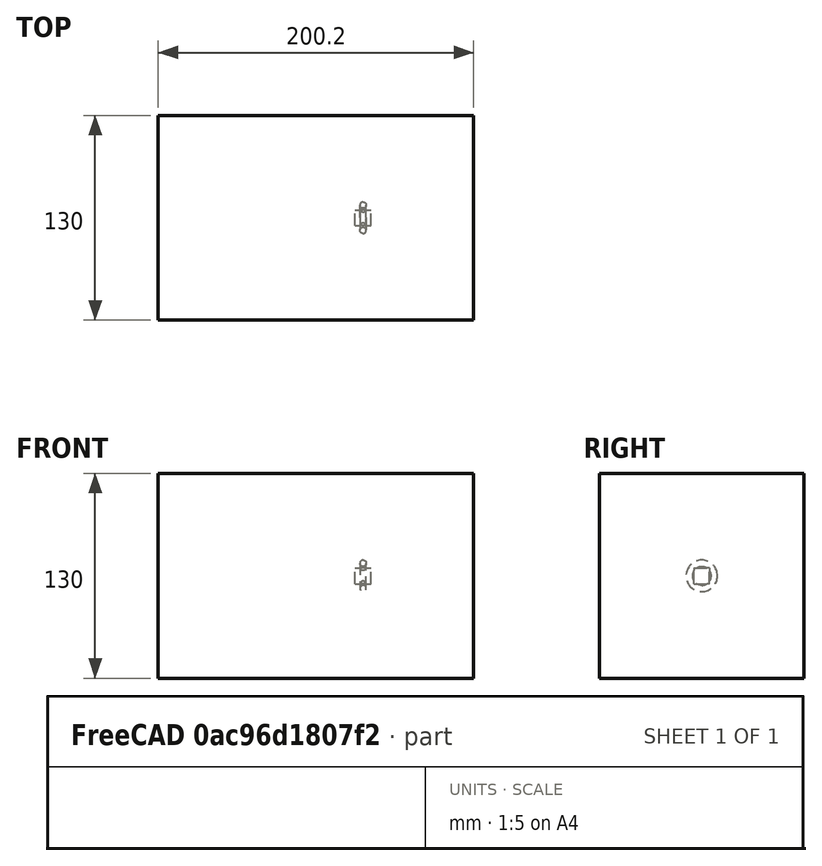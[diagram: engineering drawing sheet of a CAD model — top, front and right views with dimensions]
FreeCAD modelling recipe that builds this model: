
FCSTD DOCUMENT  (FreeCAD 1.0R39109 (Git))
Label: polarArray-7-array-translated
License: All rights reserved
objects: App::DocumentObjectGroupPython×1251, Part::FeaturePython×4, App::Part×2, Part::MultiFuse×1
note: 4 computed .brp shape members not serialized (recipe doc carries the construction recipe); baked Part::Feature solids carry a one-line shape summary decoded from their .brp

FEATURE [App::DocumentObjectGroupPython] HALFPI  # scripted group (container) (typed FeaturePython)
  name = HALFPI
  value = pi/2.
FEATURE [App::DocumentObjectGroupPython] PI  # scripted group (container) (typed FeaturePython)
  name = PI
  value = 1.*pi
FEATURE [App::DocumentObjectGroupPython] TWOPI  # scripted group (container) (typed FeaturePython)
  name = TWOPI
  value = 2.*pi
FEATURE [App::DocumentObjectGroupPython] Constants  # scripted group (container) (typed FeaturePython)
  Group = -> [HALFPI,PI,TWOPI]
FEATURE [App::DocumentObjectGroupPython] Variables  # scripted group (container) (typed FeaturePython)
FEATURE [App::DocumentObjectGroupPython] Quantities  # scripted group (container) (typed FeaturePython)
FEATURE [App::DocumentObjectGroupPython] Isotopes  # scripted group (container) (typed FeaturePython)
FEATURE [App::DocumentObjectGroupPython] Elements  # scripted group (container) (typed FeaturePython)
FEATURE [App::DocumentObjectGroupPython] Matrix  # scripted group (container) (typed FeaturePython)
FEATURE [App::DocumentObjectGroupPython] Surfaces  # scripted group (container) (typed FeaturePython)
FEATURE [App::DocumentObjectGroupPython] Opticals  # scripted group (container) (typed FeaturePython)
  Group = -> [Matrix,Surfaces]
FEATURE [App::DocumentObjectGroupPython] G4Isotopes  # scripted group (container) (typed FeaturePython)
FEATURE [App::DocumentObjectGroupPython] H_element  # scripted group (container) (typed FeaturePython)
  Z = 1
  atom_value = 1.008
  formula = H
  name = H_element
FEATURE [App::DocumentObjectGroupPython] He_element  # scripted group (container) (typed FeaturePython)
  Z = 2
  atom_value = 4.0026
  formula = He
  name = He_element
FEATURE [App::DocumentObjectGroupPython] Li_element  # scripted group (container) (typed FeaturePython)
  Z = 3
  atom_value = 6.94
  formula = Li
  name = Li_element
FEATURE [App::DocumentObjectGroupPython] Be_element  # scripted group (container) (typed FeaturePython)
  Z = 4
  atom_value = 9.01218
  formula = Be
  name = Be_element
FEATURE [App::DocumentObjectGroupPython] B_element  # scripted group (container) (typed FeaturePython)
  Z = 5
  atom_value = 10.81
  formula = B
  name = B_element
FEATURE [App::DocumentObjectGroupPython] C_element  # scripted group (container) (typed FeaturePython)
  Z = 6
  atom_value = 12.011
  formula = C
  name = C_element
FEATURE [App::DocumentObjectGroupPython] N_element  # scripted group (container) (typed FeaturePython)
  Z = 7
  atom_value = 14.007
  formula = N
  name = N_element
FEATURE [App::DocumentObjectGroupPython] O_element  # scripted group (container) (typed FeaturePython)
  Z = 8
  atom_value = 15.999
  formula = O
  name = O_element
FEATURE [App::DocumentObjectGroupPython] F_element  # scripted group (container) (typed FeaturePython)
  Z = 9
  atom_value = 18.9984
  formula = F
  name = F_element
FEATURE [App::DocumentObjectGroupPython] Ne_element  # scripted group (container) (typed FeaturePython)
  Z = 10
  atom_value = 20.1797
  formula = Ne
  name = Ne_element
FEATURE [App::DocumentObjectGroupPython] Na_element  # scripted group (container) (typed FeaturePython)
  Z = 11
  atom_value = 22.9898
  formula = Na
  name = Na_element
FEATURE [App::DocumentObjectGroupPython] Mg_element  # scripted group (container) (typed FeaturePython)
  Z = 12
  atom_value = 24.305
  formula = Mg
  name = Mg_element
FEATURE [App::DocumentObjectGroupPython] Al_element  # scripted group (container) (typed FeaturePython)
  Z = 13
  atom_value = 26.9815
  formula = Al
  name = Al_element
FEATURE [App::DocumentObjectGroupPython] Si_element  # scripted group (container) (typed FeaturePython)
  Z = 14
  atom_value = 28.085
  formula = Si
  name = Si_element
FEATURE [App::DocumentObjectGroupPython] P_element  # scripted group (container) (typed FeaturePython)
  Z = 15
  atom_value = 30.9738
  formula = P
  name = P_element
FEATURE [App::DocumentObjectGroupPython] S_element  # scripted group (container) (typed FeaturePython)
  Z = 16
  atom_value = 32.06
  formula = S
  name = S_element
FEATURE [App::DocumentObjectGroupPython] Cl_element  # scripted group (container) (typed FeaturePython)
  Z = 17
  atom_value = 35.45
  formula = Cl
  name = Cl_element
FEATURE [App::DocumentObjectGroupPython] Ar_element  # scripted group (container) (typed FeaturePython)
  Z = 18
  atom_value = 39.95
  formula = Ar
  name = Ar_element
FEATURE [App::DocumentObjectGroupPython] K_element  # scripted group (container) (typed FeaturePython)
  Z = 19
  atom_value = 39.0983
  formula = K
  name = K_element
FEATURE [App::DocumentObjectGroupPython] Ca_element  # scripted group (container) (typed FeaturePython)
  Z = 20
  atom_value = 40.078
  formula = Ca
  name = Ca_element
FEATURE [App::DocumentObjectGroupPython] Sc_element  # scripted group (container) (typed FeaturePython)
  Z = 21
  atom_value = 44.9559
  formula = Sc
  name = Sc_element
FEATURE [App::DocumentObjectGroupPython] Ti_element  # scripted group (container) (typed FeaturePython)
  Z = 22
  atom_value = 47.867
  formula = Ti
  name = Ti_element
FEATURE [App::DocumentObjectGroupPython] V_element  # scripted group (container) (typed FeaturePython)
  Z = 23
  atom_value = 50.9415
  formula = V
  name = V_element
FEATURE [App::DocumentObjectGroupPython] Cr_element  # scripted group (container) (typed FeaturePython)
  Z = 24
  atom_value = 51.9961
  formula = Cr
  name = Cr_element
FEATURE [App::DocumentObjectGroupPython] Mn_element  # scripted group (container) (typed FeaturePython)
  Z = 25
  atom_value = 54.938
  formula = Mn
  name = Mn_element
FEATURE [App::DocumentObjectGroupPython] Fe_element  # scripted group (container) (typed FeaturePython)
  Z = 26
  atom_value = 55.845
  formula = Fe
  name = Fe_element
FEATURE [App::DocumentObjectGroupPython] Co_element  # scripted group (container) (typed FeaturePython)
  Z = 27
  atom_value = 58.9332
  formula = Co
  name = Co_element
FEATURE [App::DocumentObjectGroupPython] Ni_element  # scripted group (container) (typed FeaturePython)
  Z = 28
  atom_value = 58.6934
  formula = Ni
  name = Ni_element
FEATURE [App::DocumentObjectGroupPython] Cu_element  # scripted group (container) (typed FeaturePython)
  Z = 29
  atom_value = 63.546
  formula = Cu
  name = Cu_element
FEATURE [App::DocumentObjectGroupPython] Zn_element  # scripted group (container) (typed FeaturePython)
  Z = 30
  atom_value = 65.38
  formula = Zn
  name = Zn_element
FEATURE [App::DocumentObjectGroupPython] Ga_element  # scripted group (container) (typed FeaturePython)
  Z = 31
  atom_value = 69.723
  formula = Ga
  name = Ga_element
FEATURE [App::DocumentObjectGroupPython] Ge_element  # scripted group (container) (typed FeaturePython)
  Z = 32
  atom_value = 72.63
  formula = Ge
  name = Ge_element
FEATURE [App::DocumentObjectGroupPython] As_element  # scripted group (container) (typed FeaturePython)
  Z = 33
  atom_value = 74.9216
  formula = As
  name = As_element
FEATURE [App::DocumentObjectGroupPython] Se_element  # scripted group (container) (typed FeaturePython)
  Z = 34
  atom_value = 78.971
  formula = Se
  name = Se_element
FEATURE [App::DocumentObjectGroupPython] Br_element  # scripted group (container) (typed FeaturePython)
  Z = 35
  atom_value = 79.904
  formula = Br
  name = Br_element
FEATURE [App::DocumentObjectGroupPython] Kr_element  # scripted group (container) (typed FeaturePython)
  Z = 36
  atom_value = 83.798
  formula = Kr
  name = Kr_element
FEATURE [App::DocumentObjectGroupPython] Rb_element  # scripted group (container) (typed FeaturePython)
  Z = 37
  atom_value = 85.4678
  formula = Rb
  name = Rb_element
FEATURE [App::DocumentObjectGroupPython] Sr_element  # scripted group (container) (typed FeaturePython)
  Z = 38
  atom_value = 87.62
  formula = Sr
  name = Sr_element
FEATURE [App::DocumentObjectGroupPython] Y_element  # scripted group (container) (typed FeaturePython)
  Z = 39
  atom_value = 88.9058
  formula = Y
  name = Y_element
FEATURE [App::DocumentObjectGroupPython] Zr_element  # scripted group (container) (typed FeaturePython)
  Z = 40
  atom_value = 91.224
  formula = Zr
  name = Zr_element
FEATURE [App::DocumentObjectGroupPython] Nb_element  # scripted group (container) (typed FeaturePython)
  Z = 41
  atom_value = 92.9064
  formula = Nb
  name = Nb_element
FEATURE [App::DocumentObjectGroupPython] Mo_element  # scripted group (container) (typed FeaturePython)
  Z = 42
  atom_value = 95.95
  formula = Mo
  name = Mo_element
FEATURE [App::DocumentObjectGroupPython] Tc_element  # scripted group (container) (typed FeaturePython)
  Z = 43
  atom_value = 97
  formula = Tc
  name = Tc_element
FEATURE [App::DocumentObjectGroupPython] Ru_element  # scripted group (container) (typed FeaturePython)
  Z = 44
  atom_value = 101.07
  formula = Ru
  name = Ru_element
FEATURE [App::DocumentObjectGroupPython] Rh_element  # scripted group (container) (typed FeaturePython)
  Z = 45
  atom_value = 102.905
  formula = Rh
  name = Rh_element
FEATURE [App::DocumentObjectGroupPython] Pd_element  # scripted group (container) (typed FeaturePython)
  Z = 46
  atom_value = 106.42
  formula = Pd
  name = Pd_element
FEATURE [App::DocumentObjectGroupPython] Ag_element  # scripted group (container) (typed FeaturePython)
  Z = 47
  atom_value = 107.868
  formula = Ag
  name = Ag_element
FEATURE [App::DocumentObjectGroupPython] Cd_element  # scripted group (container) (typed FeaturePython)
  Z = 48
  atom_value = 112.414
  formula = Cd
  name = Cd_element
FEATURE [App::DocumentObjectGroupPython] In_element  # scripted group (container) (typed FeaturePython)
  Z = 49
  atom_value = 114.818
  formula = In
  name = In_element
FEATURE [App::DocumentObjectGroupPython] Sn_element  # scripted group (container) (typed FeaturePython)
  Z = 50
  atom_value = 118.71
  formula = Sn
  name = Sn_element
FEATURE [App::DocumentObjectGroupPython] Sb_element  # scripted group (container) (typed FeaturePython)
  Z = 51
  atom_value = 121.76
  formula = Sb
  name = Sb_element
FEATURE [App::DocumentObjectGroupPython] Te_element  # scripted group (container) (typed FeaturePython)
  Z = 52
  atom_value = 127.6
  formula = Te
  name = Te_element
FEATURE [App::DocumentObjectGroupPython] I_element  # scripted group (container) (typed FeaturePython)
  Z = 53
  atom_value = 126.904
  formula = I
  name = I_element
FEATURE [App::DocumentObjectGroupPython] Xe_element  # scripted group (container) (typed FeaturePython)
  Z = 54
  atom_value = 131.293
  formula = Xe
  name = Xe_element
FEATURE [App::DocumentObjectGroupPython] Cs_element  # scripted group (container) (typed FeaturePython)
  Z = 55
  atom_value = 132.905
  formula = Cs
  name = Cs_element
FEATURE [App::DocumentObjectGroupPython] Ba_element  # scripted group (container) (typed FeaturePython)
  Z = 56
  atom_value = 137.327
  formula = Ba
  name = Ba_element
FEATURE [App::DocumentObjectGroupPython] La_element  # scripted group (container) (typed FeaturePython)
  Z = 57
  atom_value = 138.905
  formula = La
  name = La_element
FEATURE [App::DocumentObjectGroupPython] Ce_element  # scripted group (container) (typed FeaturePython)
  Z = 58
  atom_value = 140.116
  formula = Ce
  name = Ce_element
FEATURE [App::DocumentObjectGroupPython] Pr_element  # scripted group (container) (typed FeaturePython)
  Z = 59
  atom_value = 140.908
  formula = Pr
  name = Pr_element
FEATURE [App::DocumentObjectGroupPython] Nd_element  # scripted group (container) (typed FeaturePython)
  Z = 60
  atom_value = 144.242
  formula = Nd
  name = Nd_element
FEATURE [App::DocumentObjectGroupPython] Pm_element  # scripted group (container) (typed FeaturePython)
  Z = 61
  atom_value = 145
  formula = Pm
  name = Pm_element
FEATURE [App::DocumentObjectGroupPython] Sm_element  # scripted group (container) (typed FeaturePython)
  Z = 62
  atom_value = 150.36
  formula = Sm
  name = Sm_element
FEATURE [App::DocumentObjectGroupPython] Eu_element  # scripted group (container) (typed FeaturePython)
  Z = 63
  atom_value = 151.964
  formula = Eu
  name = Eu_element
FEATURE [App::DocumentObjectGroupPython] Gd_element  # scripted group (container) (typed FeaturePython)
  Z = 64
  atom_value = 157.25
  formula = Gd
  name = Gd_element
FEATURE [App::DocumentObjectGroupPython] Tb_element  # scripted group (container) (typed FeaturePython)
  Z = 65
  atom_value = 158.925
  formula = Tb
  name = Tb_element
FEATURE [App::DocumentObjectGroupPython] Dy_element  # scripted group (container) (typed FeaturePython)
  Z = 66
  atom_value = 162.5
  formula = Dy
  name = Dy_element
FEATURE [App::DocumentObjectGroupPython] Ho_element  # scripted group (container) (typed FeaturePython)
  Z = 67
  atom_value = 164.93
  formula = Ho
  name = Ho_element
FEATURE [App::DocumentObjectGroupPython] Er_element  # scripted group (container) (typed FeaturePython)
  Z = 68
  atom_value = 167.259
  formula = Er
  name = Er_element
FEATURE [App::DocumentObjectGroupPython] Tm_element  # scripted group (container) (typed FeaturePython)
  Z = 69
  atom_value = 168.934
  formula = Tm
  name = Tm_element
FEATURE [App::DocumentObjectGroupPython] Yb_element  # scripted group (container) (typed FeaturePython)
  Z = 70
  atom_value = 173.045
  formula = Yb
  name = Yb_element
FEATURE [App::DocumentObjectGroupPython] Lu_element  # scripted group (container) (typed FeaturePython)
  Z = 71
  atom_value = 174.967
  formula = Lu
  name = Lu_element
FEATURE [App::DocumentObjectGroupPython] Hf_element  # scripted group (container) (typed FeaturePython)
  Z = 72
  atom_value = 178.49
  formula = Hf
  name = Hf_element
FEATURE [App::DocumentObjectGroupPython] Ta_element  # scripted group (container) (typed FeaturePython)
  Z = 73
  atom_value = 180.948
  formula = Ta
  name = Ta_element
FEATURE [App::DocumentObjectGroupPython] W_element  # scripted group (container) (typed FeaturePython)
  Z = 74
  atom_value = 183.84
  formula = W
  name = W_element
FEATURE [App::DocumentObjectGroupPython] Re_element  # scripted group (container) (typed FeaturePython)
  Z = 75
  atom_value = 186.207
  formula = Re
  name = Re_element
FEATURE [App::DocumentObjectGroupPython] Os_element  # scripted group (container) (typed FeaturePython)
  Z = 76
  atom_value = 190.23
  formula = Os
  name = Os_element
FEATURE [App::DocumentObjectGroupPython] Ir_element  # scripted group (container) (typed FeaturePython)
  Z = 77
  atom_value = 192.217
  formula = Ir
  name = Ir_element
FEATURE [App::DocumentObjectGroupPython] Pt_element  # scripted group (container) (typed FeaturePython)
  Z = 78
  atom_value = 195.084
  formula = Pt
  name = Pt_element
FEATURE [App::DocumentObjectGroupPython] Au_element  # scripted group (container) (typed FeaturePython)
  Z = 79
  atom_value = 196.967
  formula = Au
  name = Au_element
FEATURE [App::DocumentObjectGroupPython] Hg_element  # scripted group (container) (typed FeaturePython)
  Z = 80
  atom_value = 200.592
  formula = Hg
  name = Hg_element
FEATURE [App::DocumentObjectGroupPython] Tl_element  # scripted group (container) (typed FeaturePython)
  Z = 81
  atom_value = 204.38
  formula = Tl
  name = Tl_element
FEATURE [App::DocumentObjectGroupPython] Pb_element  # scripted group (container) (typed FeaturePython)
  Z = 82
  atom_value = 207.2
  formula = Pb
  name = Pb_element
FEATURE [App::DocumentObjectGroupPython] Bi_element  # scripted group (container) (typed FeaturePython)
  Z = 83
  atom_value = 208.98
  formula = Bi
  name = Bi_element
FEATURE [App::DocumentObjectGroupPython] Po_element  # scripted group (container) (typed FeaturePython)
  Z = 84
  atom_value = 209
  formula = Po
  name = Po_element
FEATURE [App::DocumentObjectGroupPython] At_element  # scripted group (container) (typed FeaturePython)
  Z = 85
  atom_value = 210
  formula = At
  name = At_element
FEATURE [App::DocumentObjectGroupPython] Rn_element  # scripted group (container) (typed FeaturePython)
  Z = 86
  atom_value = 222
  formula = Rn
  name = Rn_element
FEATURE [App::DocumentObjectGroupPython] Fr_element  # scripted group (container) (typed FeaturePython)
  Z = 87
  atom_value = 223
  formula = Fr
  name = Fr_element
FEATURE [App::DocumentObjectGroupPython] Ra_element  # scripted group (container) (typed FeaturePython)
  Z = 88
  atom_value = 226
  formula = Ra
  name = Ra_element
FEATURE [App::DocumentObjectGroupPython] Ac_element  # scripted group (container) (typed FeaturePython)
  Z = 89
  atom_value = 227
  formula = Ac
  name = Ac_element
FEATURE [App::DocumentObjectGroupPython] Th_element  # scripted group (container) (typed FeaturePython)
  Z = 90
  atom_value = 232.038
  formula = Th
  name = Th_element
FEATURE [App::DocumentObjectGroupPython] Pa_element  # scripted group (container) (typed FeaturePython)
  Z = 91
  atom_value = 231.036
  formula = Pa
  name = Pa_element
FEATURE [App::DocumentObjectGroupPython] U_element  # scripted group (container) (typed FeaturePython)
  Z = 92
  atom_value = 238.029
  formula = U
  name = U_element
FEATURE [App::DocumentObjectGroupPython] Np_element  # scripted group (container) (typed FeaturePython)
  Z = 93
  atom_value = 237
  formula = Np
  name = Np_element
FEATURE [App::DocumentObjectGroupPython] Pu_element  # scripted group (container) (typed FeaturePython)
  Z = 94
  atom_value = 244
  formula = Pu
  name = Pu_element
FEATURE [App::DocumentObjectGroupPython] Am_element  # scripted group (container) (typed FeaturePython)
  Z = 95
  atom_value = 243
  formula = Am
  name = Am_element
FEATURE [App::DocumentObjectGroupPython] Cm_element  # scripted group (container) (typed FeaturePython)
  Z = 96
  atom_value = 247
  formula = Cm
  name = Cm_element
FEATURE [App::DocumentObjectGroupPython] Bk_element  # scripted group (container) (typed FeaturePython)
  Z = 97
  atom_value = 247
  formula = Bk
  name = Bk_element
FEATURE [App::DocumentObjectGroupPython] Cf_element  # scripted group (container) (typed FeaturePython)
  Z = 98
  atom_value = 251
  formula = Cf
  name = Cf_element
FEATURE [App::DocumentObjectGroupPython] G4Elements  # scripted group (container) (typed FeaturePython)
  Group = -> [H_element,He_element,Li_element,Be_element,B_element,C_element,N_element,O_element,F_element,Ne_element,Na_element,Mg_element,Al_element,Si_element,P_element,S_element,Cl_element,Ar_element,K_element,Ca_element,Sc_element,Ti_element,V_element,Cr_element,Mn_element,Fe_element,Co_element,Ni_element,Cu_element,Zn_element,Ga_element,Ge_element,As_element,Se_element,Br_element,Kr_element,Rb_element,+61 more]
FEATURE [App::DocumentObjectGroupPython] H_element001  label="H_element : 0.101"  # scripted group (container) (typed FeaturePython)
  n = 0.101327
FEATURE [App::DocumentObjectGroupPython] C_element001  label="C_element : 0.775"  # scripted group (container) (typed FeaturePython)
  n = 0.7755
FEATURE [App::DocumentObjectGroupPython] N_element001  label="N_element : 0.035"  # scripted group (container) (typed FeaturePython)
  n = 0.035057
FEATURE [App::DocumentObjectGroupPython] O_element001  label="O_element : 0.052"  # scripted group (container) (typed FeaturePython)
  n = 0.0523159
FEATURE [App::DocumentObjectGroupPython] F_element001  label="F_element : 0.017"  # scripted group (container) (typed FeaturePython)
  n = 0.017422
FEATURE [App::DocumentObjectGroupPython] Ca_element001  label="Ca_element : 0.018"  # scripted group (container) (typed FeaturePython)
  n = 0.018378
FEATURE [App::DocumentObjectGroupPython] G4_A_150_TISSUE  label="G4_A-150_TISSUE"  # scripted group (container) (typed FeaturePython)
  Dunit = g/cm3
  Dvalue = 1.127
  Group = -> [H_element001,C_element001,N_element001,O_element001,F_element001,Ca_element001]
  conduct = 2
  density = 1
  expand = 3
  formula = G4_A-150_TISSUE
  name = G4_A-150_TISSUE
  specific = 4
FEATURE [App::DocumentObjectGroupPython] C_element002  label="C_element : 3"  # scripted group (container) (typed FeaturePython)
  n = 3
  ref = C_element
FEATURE [App::DocumentObjectGroupPython] H_element002  label="H_element : 6"  # scripted group (container) (typed FeaturePython)
  n = 6
  ref = H_element
FEATURE [App::DocumentObjectGroupPython] O_element002  label="O_element : 1"  # scripted group (container) (typed FeaturePython)
  n = 1
  ref = O_element
FEATURE [App::DocumentObjectGroupPython] G4_ACETONE  # scripted group (container) (typed FeaturePython)
  Dunit = g/cm3
  Dvalue = 0.7899
  Group = -> [C_element002,H_element002,O_element002]
  conduct = 2
  density = 1
  expand = 3
  formula = G4_ACETONE
  name = G4_ACETONE
  specific = 4
FEATURE [App::DocumentObjectGroupPython] C_element003  label="C_element : 2"  # scripted group (container) (typed FeaturePython)
  n = 2
  ref = C_element
FEATURE [App::DocumentObjectGroupPython] H_element003  label="H_element : 2"  # scripted group (container) (typed FeaturePython)
  n = 2
  ref = H_element
FEATURE [App::DocumentObjectGroupPython] G4_ACETYLENE  # scripted group (container) (typed FeaturePython)
  Dunit = g/cm3
  Dvalue = 0.0010967
  Group = -> [C_element003,H_element003]
  conduct = 2
  density = 1
  expand = 3
  formula = G4_ACETYLENE
  name = G4_ACETYLENE
  specific = 4
FEATURE [App::DocumentObjectGroupPython] C_element004  label="C_element : 5"  # scripted group (container) (typed FeaturePython)
  n = 5
  ref = C_element
FEATURE [App::DocumentObjectGroupPython] H_element004  label="H_element : 5"  # scripted group (container) (typed FeaturePython)
  n = 5
  ref = H_element
FEATURE [App::DocumentObjectGroupPython] N_element002  label="N_element : 5"  # scripted group (container) (typed FeaturePython)
  n = 5
  ref = N_element
FEATURE [App::DocumentObjectGroupPython] G4_ADENINE  # scripted group (container) (typed FeaturePython)
  Dunit = g/cm3
  Dvalue = 1.6
  Group = -> [C_element004,H_element004,N_element002]
  conduct = 2
  density = 1
  expand = 3
  formula = G4_ADENINE
  name = G4_ADENINE
  specific = 4
FEATURE [App::DocumentObjectGroupPython] H_element005  label="H_element : 0.114"  # scripted group (container) (typed FeaturePython)
  n = 0.114
FEATURE [App::DocumentObjectGroupPython] C_element005  label="C_element : 0.598"  # scripted group (container) (typed FeaturePython)
  n = 0.598
FEATURE [App::DocumentObjectGroupPython] N_element003  label="N_element : 0.007"  # scripted group (container) (typed FeaturePython)
  n = 0.007
FEATURE [App::DocumentObjectGroupPython] O_element003  label="O_element : 0.278"  # scripted group (container) (typed FeaturePython)
  n = 0.278
FEATURE [App::DocumentObjectGroupPython] Na_element001  label="Na_element : 0.001"  # scripted group (container) (typed FeaturePython)
  n = 0.001
FEATURE [App::DocumentObjectGroupPython] S_element001  label="S_element : 0.001"  # scripted group (container) (typed FeaturePython)
  n = 0.001
FEATURE [App::DocumentObjectGroupPython] Cl_element001  label="Cl_element : 0.001"  # scripted group (container) (typed FeaturePython)
  n = 0.001
FEATURE [App::DocumentObjectGroupPython] G4_ADIPOSE_TISSUE_ICRP  # scripted group (container) (typed FeaturePython)
  Dunit = g/cm3
  Dvalue = 0.95
  Group = -> [H_element005,C_element005,N_element003,O_element003,Na_element001,S_element001,Cl_element001]
  conduct = 2
  density = 1
  expand = 3
  formula = G4_ADIPOSE_TISSUE_ICRP
  name = G4_ADIPOSE_TISSUE_ICRP
  specific = 4
FEATURE [App::DocumentObjectGroupPython] C_element006  label="C_element : 0.000"  # scripted group (container) (typed FeaturePython)
  n = 0.000124
FEATURE [App::DocumentObjectGroupPython] N_element004  label="N_element : 0.755"  # scripted group (container) (typed FeaturePython)
  n = 0.755268
FEATURE [App::DocumentObjectGroupPython] O_element004  label="O_element : 0.232"  # scripted group (container) (typed FeaturePython)
  n = 0.231781
FEATURE [App::DocumentObjectGroupPython] Ar_element001  label="Ar_element : 0.013"  # scripted group (container) (typed FeaturePython)
  n = 0.012827
FEATURE [App::DocumentObjectGroupPython] G4_AIR  # scripted group (container) (typed FeaturePython)
  Dunit = g/cm3
  Dvalue = 0.00120479
  Group = -> [C_element006,N_element004,O_element004,Ar_element001]
  conduct = 2
  density = 1
  expand = 3
  formula = G4_AIR
  name = G4_AIR
  specific = 4
FEATURE [App::DocumentObjectGroupPython] C_element007  label="C_element : 006"  # scripted group (container) (typed FeaturePython)
  n = 3
  ref = C_element
FEATURE [App::DocumentObjectGroupPython] H_element006  label="H_element : 7"  # scripted group (container) (typed FeaturePython)
  n = 7
  ref = H_element
FEATURE [App::DocumentObjectGroupPython] N_element005  label="N_element : 1"  # scripted group (container) (typed FeaturePython)
  n = 1
  ref = N_element
FEATURE [App::DocumentObjectGroupPython] O_element005  label="O_element : 2"  # scripted group (container) (typed FeaturePython)
  n = 2
  ref = O_element
FEATURE [App::DocumentObjectGroupPython] G4_ALANINE  # scripted group (container) (typed FeaturePython)
  Dunit = g/cm3
  Dvalue = 1.42
  Group = -> [C_element007,H_element006,N_element005,O_element005]
  conduct = 2
  density = 1
  expand = 3
  formula = G4_ALANINE
  name = G4_ALANINE
  specific = 4
FEATURE [App::DocumentObjectGroupPython] Al_element001  label="Al_element : 2"  # scripted group (container) (typed FeaturePython)
  n = 2
  ref = Al_element
FEATURE [App::DocumentObjectGroupPython] O_element006  label="O_element : 3"  # scripted group (container) (typed FeaturePython)
  n = 3
  ref = O_element
FEATURE [App::DocumentObjectGroupPython] G4_ALUMINUM_OXIDE  # scripted group (container) (typed FeaturePython)
  Dunit = g/cm3
  Dvalue = 3.97
  Group = -> [Al_element001,O_element006]
  conduct = 2
  density = 1
  expand = 3
  formula = G4_ALUMINUM_OXIDE
  name = G4_ALUMINUM_OXIDE
  specific = 4
FEATURE [App::DocumentObjectGroupPython] H_element007  label="H_element : 0.106"  # scripted group (container) (typed FeaturePython)
  n = 0.10593
FEATURE [App::DocumentObjectGroupPython] C_element008  label="C_element : 0.789"  # scripted group (container) (typed FeaturePython)
  n = 0.788974
FEATURE [App::DocumentObjectGroupPython] O_element007  label="O_element : 0.105"  # scripted group (container) (typed FeaturePython)
  n = 0.105096
FEATURE [App::DocumentObjectGroupPython] G4_AMBER  # scripted group (container) (typed FeaturePython)
  Dunit = g/cm3
  Dvalue = 1.1
  Group = -> [H_element007,C_element008,O_element007]
  conduct = 2
  density = 1
  expand = 3
  formula = G4_AMBER
  name = G4_AMBER
  specific = 4
FEATURE [App::DocumentObjectGroupPython] N_element006  label="N_element : 006"  # scripted group (container) (typed FeaturePython)
  n = 1
  ref = N_element
FEATURE [App::DocumentObjectGroupPython] H_element008  label="H_element : 3"  # scripted group (container) (typed FeaturePython)
  n = 3
  ref = H_element
FEATURE [App::DocumentObjectGroupPython] G4_AMMONIA  # scripted group (container) (typed FeaturePython)
  Dunit = g/cm3
  Dvalue = 0.000826019
  Group = -> [N_element006,H_element008]
  conduct = 2
  density = 1
  expand = 3
  formula = G4_AMMONIA
  name = G4_AMMONIA
  specific = 4
FEATURE [App::DocumentObjectGroupPython] C_element009  label="C_element : 6"  # scripted group (container) (typed FeaturePython)
  n = 6
  ref = C_element
FEATURE [App::DocumentObjectGroupPython] H_element009  label="H_element : 008"  # scripted group (container) (typed FeaturePython)
  n = 7
  ref = H_element
FEATURE [App::DocumentObjectGroupPython] N_element007  label="N_element : 007"  # scripted group (container) (typed FeaturePython)
  n = 1
  ref = N_element
FEATURE [App::DocumentObjectGroupPython] G4_ANILINE  # scripted group (container) (typed FeaturePython)
  Dunit = g/cm3
  Dvalue = 1.0235
  Group = -> [C_element009,H_element009,N_element007]
  conduct = 2
  density = 1
  expand = 3
  formula = G4_ANILINE
  name = G4_ANILINE
  specific = 4
FEATURE [App::DocumentObjectGroupPython] C_element010  label="C_element : 14"  # scripted group (container) (typed FeaturePython)
  n = 14
  ref = C_element
FEATURE [App::DocumentObjectGroupPython] H_element010  label="H_element : 10"  # scripted group (container) (typed FeaturePython)
  n = 10
  ref = H_element
FEATURE [App::DocumentObjectGroupPython] G4_ANTHRACENE  # scripted group (container) (typed FeaturePython)
  Dunit = g/cm3
  Dvalue = 1.283
  Group = -> [C_element010,H_element010]
  conduct = 2
  density = 1
  expand = 3
  formula = G4_ANTHRACENE
  name = G4_ANTHRACENE
  specific = 4
FEATURE [App::DocumentObjectGroupPython] H_element011  label="H_element : 0.065"  # scripted group (container) (typed FeaturePython)
  n = 0.0654709
FEATURE [App::DocumentObjectGroupPython] C_element011  label="C_element : 0.537"  # scripted group (container) (typed FeaturePython)
  n = 0.536944
FEATURE [App::DocumentObjectGroupPython] N_element008  label="N_element : 0.021"  # scripted group (container) (typed FeaturePython)
  n = 0.0215
FEATURE [App::DocumentObjectGroupPython] O_element008  label="O_element : 0.032"  # scripted group (container) (typed FeaturePython)
  n = 0.032085
FEATURE [App::DocumentObjectGroupPython] F_element002  label="F_element : 0.167"  # scripted group (container) (typed FeaturePython)
  n = 0.167411
FEATURE [App::DocumentObjectGroupPython] Ca_element002  label="Ca_element : 0.177"  # scripted group (container) (typed FeaturePython)
  n = 0.176589
FEATURE [App::DocumentObjectGroupPython] G4_B_100_BONE  label="G4_B-100_BONE"  # scripted group (container) (typed FeaturePython)
  Dunit = g/cm3
  Dvalue = 1.45
  Group = -> [H_element011,C_element011,N_element008,O_element008,F_element002,Ca_element002]
  conduct = 2
  density = 1
  expand = 3
  formula = G4_B-100_BONE
  name = G4_B-100_BONE
  specific = 4
FEATURE [App::DocumentObjectGroupPython] H_element012  label="H_element : 0.057"  # scripted group (container) (typed FeaturePython)
  n = 0.057441
FEATURE [App::DocumentObjectGroupPython] C_element012  label="C_element : 0.790"  # scripted group (container) (typed FeaturePython)
  n = 0.774591
FEATURE [App::DocumentObjectGroupPython] O_element009  label="O_element : 0.168"  # scripted group (container) (typed FeaturePython)
  n = 0.167968
FEATURE [App::DocumentObjectGroupPython] G4_BAKELITE  # scripted group (container) (typed FeaturePython)
  Dunit = g/cm3
  Dvalue = 1.25
  Group = -> [H_element012,C_element012,O_element009]
  conduct = 2
  density = 1
  expand = 3
  formula = G4_BAKELITE
  name = G4_BAKELITE
  specific = 4
FEATURE [App::DocumentObjectGroupPython] Ba_element001  label="Ba_element : 1"  # scripted group (container) (typed FeaturePython)
  n = 1
  ref = Ba_element
FEATURE [App::DocumentObjectGroupPython] F_element003  label="F_element : 2"  # scripted group (container) (typed FeaturePython)
  n = 2
  ref = F_element
FEATURE [App::DocumentObjectGroupPython] G4_BARIUM_FLUORIDE  # scripted group (container) (typed FeaturePython)
  Dunit = g/cm3
  Dvalue = 4.89
  Group = -> [Ba_element001,F_element003]
  conduct = 2
  density = 1
  expand = 3
  formula = G4_BARIUM_FLUORIDE
  name = G4_BARIUM_FLUORIDE
  specific = 4
FEATURE [App::DocumentObjectGroupPython] Ba_element002  label="Ba_element : 002"  # scripted group (container) (typed FeaturePython)
  n = 1
  ref = Ba_element
FEATURE [App::DocumentObjectGroupPython] S_element002  label="S_element : 1"  # scripted group (container) (typed FeaturePython)
  n = 1
  ref = S_element
FEATURE [App::DocumentObjectGroupPython] O_element010  label="O_element : 4"  # scripted group (container) (typed FeaturePython)
  n = 4
  ref = O_element
FEATURE [App::DocumentObjectGroupPython] G4_BARIUM_SULFATE  # scripted group (container) (typed FeaturePython)
  Dunit = g/cm3
  Dvalue = 4.5
  Group = -> [Ba_element002,S_element002,O_element010]
  conduct = 2
  density = 1
  expand = 3
  formula = G4_BARIUM_SULFATE
  name = G4_BARIUM_SULFATE
  specific = 4
FEATURE [App::DocumentObjectGroupPython] C_element013  label="C_element : 007"  # scripted group (container) (typed FeaturePython)
  n = 6
  ref = C_element
FEATURE [App::DocumentObjectGroupPython] H_element013  label="H_element : 009"  # scripted group (container) (typed FeaturePython)
  n = 6
  ref = H_element
FEATURE [App::DocumentObjectGroupPython] G4_BENZENE  # scripted group (container) (typed FeaturePython)
  Dunit = g/cm3
  Dvalue = 0.87865
  Group = -> [C_element013,H_element013]
  conduct = 2
  density = 1
  expand = 3
  formula = G4_BENZENE
  name = G4_BENZENE
  specific = 4
FEATURE [App::DocumentObjectGroupPython] Be_element001  label="Be_element : 1"  # scripted group (container) (typed FeaturePython)
  n = 1
  ref = Be_element
FEATURE [App::DocumentObjectGroupPython] O_element011  label="O_element : 005"  # scripted group (container) (typed FeaturePython)
  n = 1
  ref = O_element
FEATURE [App::DocumentObjectGroupPython] G4_BERYLLIUM_OXIDE  # scripted group (container) (typed FeaturePython)
  Dunit = g/cm3
  Dvalue = 3.01
  Group = -> [Be_element001,O_element011]
  conduct = 2
  density = 1
  expand = 3
  formula = G4_BERYLLIUM_OXIDE
  name = G4_BERYLLIUM_OXIDE
  specific = 4
FEATURE [App::DocumentObjectGroupPython] Bi_element001  label="Bi_element : 4"  # scripted group (container) (typed FeaturePython)
  n = 4
  ref = Bi_element
FEATURE [App::DocumentObjectGroupPython] Ge_element001  label="Ge_element : 3"  # scripted group (container) (typed FeaturePython)
  n = 3
  ref = Ge_element
FEATURE [App::DocumentObjectGroupPython] O_element012  label="O_element : 12"  # scripted group (container) (typed FeaturePython)
  n = 12
  ref = O_element
FEATURE [App::DocumentObjectGroupPython] G4_BGO  # scripted group (container) (typed FeaturePython)
  Dunit = g/cm3
  Dvalue = 7.13
  Group = -> [Bi_element001,Ge_element001,O_element012]
  conduct = 2
  density = 1
  expand = 3
  formula = G4_BGO
  name = G4_BGO
  specific = 4
FEATURE [App::DocumentObjectGroupPython] H_element014  label="H_element : 0.102"  # scripted group (container) (typed FeaturePython)
  n = 0.102
FEATURE [App::DocumentObjectGroupPython] C_element014  label="C_element : 0.110"  # scripted group (container) (typed FeaturePython)
  n = 0.11
FEATURE [App::DocumentObjectGroupPython] N_element009  label="N_element : 0.033"  # scripted group (container) (typed FeaturePython)
  n = 0.033
FEATURE [App::DocumentObjectGroupPython] O_element013  label="O_element : 0.745"  # scripted group (container) (typed FeaturePython)
  n = 0.745
FEATURE [App::DocumentObjectGroupPython] Na_element002  label="Na_element : 0.002"  # scripted group (container) (typed FeaturePython)
  n = 0.001
FEATURE [App::DocumentObjectGroupPython] P_element001  label="P_element : 0.001"  # scripted group (container) (typed FeaturePython)
  n = 0.001
FEATURE [App::DocumentObjectGroupPython] S_element003  label="S_element : 0.002"  # scripted group (container) (typed FeaturePython)
  n = 0.002
FEATURE [App::DocumentObjectGroupPython] Cl_element002  label="Cl_element : 0.003"  # scripted group (container) (typed FeaturePython)
  n = 0.003
FEATURE [App::DocumentObjectGroupPython] K_element001  label="K_element : 0.002"  # scripted group (container) (typed FeaturePython)
  n = 0.002
FEATURE [App::DocumentObjectGroupPython] Fe_element001  label="Fe_element : 0.001"  # scripted group (container) (typed FeaturePython)
  n = 0.001
FEATURE [App::DocumentObjectGroupPython] G4_BLOOD_ICRP  # scripted group (container) (typed FeaturePython)
  Dunit = g/cm3
  Dvalue = 1.06
  Group = -> [H_element014,C_element014,N_element009,O_element013,Na_element002,P_element001,S_element003,Cl_element002,K_element001,Fe_element001]
  conduct = 2
  density = 1
  expand = 3
  formula = G4_BLOOD_ICRP
  name = G4_BLOOD_ICRP
  specific = 4
FEATURE [App::DocumentObjectGroupPython] H_element015  label="H_element : 0.064"  # scripted group (container) (typed FeaturePython)
  n = 0.064
FEATURE [App::DocumentObjectGroupPython] C_element015  label="C_element : 0.278"  # scripted group (container) (typed FeaturePython)
  n = 0.278
FEATURE [App::DocumentObjectGroupPython] N_element010  label="N_element : 0.027"  # scripted group (container) (typed FeaturePython)
  n = 0.027
FEATURE [App::DocumentObjectGroupPython] O_element014  label="O_element : 0.410"  # scripted group (container) (typed FeaturePython)
  n = 0.41
FEATURE [App::DocumentObjectGroupPython] Mg_element001  label="Mg_element : 0.002"  # scripted group (container) (typed FeaturePython)
  n = 0.002
FEATURE [App::DocumentObjectGroupPython] P_element002  label="P_element : 0.070"  # scripted group (container) (typed FeaturePython)
  n = 0.07
FEATURE [App::DocumentObjectGroupPython] S_element004  label="S_element : 0.003"  # scripted group (container) (typed FeaturePython)
  n = 0.002
FEATURE [App::DocumentObjectGroupPython] Ca_element003  label="Ca_element : 0.147"  # scripted group (container) (typed FeaturePython)
  n = 0.147
FEATURE [App::DocumentObjectGroupPython] G4_BONE_COMPACT_ICRU  # scripted group (container) (typed FeaturePython)
  Dunit = g/cm3
  Dvalue = 1.85
  Group = -> [H_element015,C_element015,N_element010,O_element014,Mg_element001,P_element002,S_element004,Ca_element003]
  conduct = 2
  density = 1
  expand = 3
  formula = G4_BONE_COMPACT_ICRU
  name = G4_BONE_COMPACT_ICRU
  specific = 4
FEATURE [App::DocumentObjectGroupPython] H_element016  label="H_element : 0.034"  # scripted group (container) (typed FeaturePython)
  n = 0.034
FEATURE [App::DocumentObjectGroupPython] C_element016  label="C_element : 0.155"  # scripted group (container) (typed FeaturePython)
  n = 0.155
FEATURE [App::DocumentObjectGroupPython] N_element011  label="N_element : 0.042"  # scripted group (container) (typed FeaturePython)
  n = 0.042
FEATURE [App::DocumentObjectGroupPython] O_element015  label="O_element : 0.435"  # scripted group (container) (typed FeaturePython)
  n = 0.435
FEATURE [App::DocumentObjectGroupPython] Na_element003  label="Na_element : 0.003"  # scripted group (container) (typed FeaturePython)
  n = 0.001
FEATURE [App::DocumentObjectGroupPython] Mg_element002  label="Mg_element : 0.003"  # scripted group (container) (typed FeaturePython)
  n = 0.002
FEATURE [App::DocumentObjectGroupPython] P_element003  label="P_element : 0.103"  # scripted group (container) (typed FeaturePython)
  n = 0.103
FEATURE [App::DocumentObjectGroupPython] S_element005  label="S_element : 0.004"  # scripted group (container) (typed FeaturePython)
  n = 0.003
FEATURE [App::DocumentObjectGroupPython] Ca_element004  label="Ca_element : 0.225"  # scripted group (container) (typed FeaturePython)
  n = 0.225
FEATURE [App::DocumentObjectGroupPython] G4_BONE_CORTICAL_ICRP  # scripted group (container) (typed FeaturePython)
  Dunit = g/cm3
  Dvalue = 1.92
  Group = -> [H_element016,C_element016,N_element011,O_element015,Na_element003,Mg_element002,P_element003,S_element005,Ca_element004]
  conduct = 2
  density = 1
  expand = 3
  formula = G4_BONE_CORTICAL_ICRP
  name = G4_BONE_CORTICAL_ICRP
  specific = 4
FEATURE [App::DocumentObjectGroupPython] B_element001  label="B_element : 4"  # scripted group (container) (typed FeaturePython)
  n = 4
  ref = B_element
FEATURE [App::DocumentObjectGroupPython] C_element017  label="C_element : 1"  # scripted group (container) (typed FeaturePython)
  n = 1
  ref = C_element
FEATURE [App::DocumentObjectGroupPython] G4_BORON_CARBIDE  # scripted group (container) (typed FeaturePython)
  Dunit = g/cm3
  Dvalue = 2.52
  Group = -> [B_element001,C_element017]
  conduct = 2
  density = 1
  expand = 3
  formula = G4_BORON_CARBIDE
  name = G4_BORON_CARBIDE
  specific = 4
FEATURE [App::DocumentObjectGroupPython] B_element002  label="B_element : 2"  # scripted group (container) (typed FeaturePython)
  n = 2
  ref = B_element
FEATURE [App::DocumentObjectGroupPython] O_element016  label="O_element : 006"  # scripted group (container) (typed FeaturePython)
  n = 3
  ref = O_element
FEATURE [App::DocumentObjectGroupPython] G4_BORON_OXIDE  # scripted group (container) (typed FeaturePython)
  Dunit = g/cm3
  Dvalue = 1.812
  Group = -> [B_element002,O_element016]
  conduct = 2
  density = 1
  expand = 3
  formula = G4_BORON_OXIDE
  name = G4_BORON_OXIDE
  specific = 4
FEATURE [App::DocumentObjectGroupPython] H_element017  label="H_element : 0.107"  # scripted group (container) (typed FeaturePython)
  n = 0.107
FEATURE [App::DocumentObjectGroupPython] C_element018  label="C_element : 0.145"  # scripted group (container) (typed FeaturePython)
  n = 0.145
FEATURE [App::DocumentObjectGroupPython] N_element012  label="N_element : 0.022"  # scripted group (container) (typed FeaturePython)
  n = 0.022
FEATURE [App::DocumentObjectGroupPython] O_element017  label="O_element : 0.712"  # scripted group (container) (typed FeaturePython)
  n = 0.712
FEATURE [App::DocumentObjectGroupPython] Na_element004  label="Na_element : 0.004"  # scripted group (container) (typed FeaturePython)
  n = 0.002
FEATURE [App::DocumentObjectGroupPython] P_element004  label="P_element : 0.004"  # scripted group (container) (typed FeaturePython)
  n = 0.004
FEATURE [App::DocumentObjectGroupPython] S_element006  label="S_element : 0.005"  # scripted group (container) (typed FeaturePython)
  n = 0.002
FEATURE [App::DocumentObjectGroupPython] Cl_element003  label="Cl_element : 0.004"  # scripted group (container) (typed FeaturePython)
  n = 0.003
FEATURE [App::DocumentObjectGroupPython] K_element002  label="K_element : 0.003"  # scripted group (container) (typed FeaturePython)
  n = 0.003
FEATURE [App::DocumentObjectGroupPython] G4_BRAIN_ICRP  # scripted group (container) (typed FeaturePython)
  Dunit = g/cm3
  Dvalue = 1.04
  Group = -> [H_element017,C_element018,N_element012,O_element017,Na_element004,P_element004,S_element006,Cl_element003,K_element002]
  conduct = 2
  density = 1
  expand = 3
  formula = G4_BRAIN_ICRP
  name = G4_BRAIN_ICRP
  specific = 4
FEATURE [App::DocumentObjectGroupPython] C_element019  label="C_element : 4"  # scripted group (container) (typed FeaturePython)
  n = 4
  ref = C_element
FEATURE [App::DocumentObjectGroupPython] H_element018  label="H_element : 010"  # scripted group (container) (typed FeaturePython)
  n = 10
  ref = H_element
FEATURE [App::DocumentObjectGroupPython] G4_BUTANE  # scripted group (container) (typed FeaturePython)
  Dunit = g/cm3
  Dvalue = 0.00249343
  Group = -> [C_element019,H_element018]
  conduct = 2
  density = 1
  expand = 3
  formula = G4_BUTANE
  name = G4_BUTANE
  specific = 4
FEATURE [App::DocumentObjectGroupPython] C_element020  label="C_element : 008"  # scripted group (container) (typed FeaturePython)
  n = 4
  ref = C_element
FEATURE [App::DocumentObjectGroupPython] H_element019  label="H_element : 011"  # scripted group (container) (typed FeaturePython)
  n = 10
  ref = H_element
FEATURE [App::DocumentObjectGroupPython] O_element018  label="O_element : 007"  # scripted group (container) (typed FeaturePython)
  n = 1
  ref = O_element
FEATURE [App::DocumentObjectGroupPython] G4_N_BUTYL_ALCOHOL  label="G4_N-BUTYL_ALCOHOL"  # scripted group (container) (typed FeaturePython)
  Dunit = g/cm3
  Dvalue = 0.8098
  Group = -> [C_element020,H_element019,O_element018]
  conduct = 2
  density = 1
  expand = 3
  formula = G4_N-BUTYL_ALCOHOL
  name = G4_N-BUTYL_ALCOHOL
  specific = 4
FEATURE [App::DocumentObjectGroupPython] H_element020  label="H_element : 0.025"  # scripted group (container) (typed FeaturePython)
  n = 0.02468
FEATURE [App::DocumentObjectGroupPython] C_element021  label="C_element : 0.502"  # scripted group (container) (typed FeaturePython)
  n = 0.501611
FEATURE [App::DocumentObjectGroupPython] O_element019  label="O_element : 0.005"  # scripted group (container) (typed FeaturePython)
  n = 0.004527
FEATURE [App::DocumentObjectGroupPython] F_element004  label="F_element : 0.465"  # scripted group (container) (typed FeaturePython)
  n = 0.465209
FEATURE [App::DocumentObjectGroupPython] Si_element001  label="Si_element : 0.004"  # scripted group (container) (typed FeaturePython)
  n = 0.003973
FEATURE [App::DocumentObjectGroupPython] G4_C_552  label="G4_C-552"  # scripted group (container) (typed FeaturePython)
  Dunit = g/cm3
  Dvalue = 1.76
  Group = -> [H_element020,C_element021,O_element019,F_element004,Si_element001]
  conduct = 2
  density = 1
  expand = 3
  formula = G4_C-552
  name = G4_C-552
  specific = 4
FEATURE [App::DocumentObjectGroupPython] Cd_element001  label="Cd_element : 1"  # scripted group (container) (typed FeaturePython)
  n = 1
  ref = Cd_element
FEATURE [App::DocumentObjectGroupPython] Te_element001  label="Te_element : 1"  # scripted group (container) (typed FeaturePython)
  n = 1
  ref = Te_element
FEATURE [App::DocumentObjectGroupPython] G4_CADMIUM_TELLURIDE  # scripted group (container) (typed FeaturePython)
  Dunit = g/cm3
  Dvalue = 6.2
  Group = -> [Cd_element001,Te_element001]
  conduct = 2
  density = 1
  expand = 3
  formula = G4_CADMIUM_TELLURIDE
  name = G4_CADMIUM_TELLURIDE
  specific = 4
FEATURE [App::DocumentObjectGroupPython] Cd_element002  label="Cd_element : 002"  # scripted group (container) (typed FeaturePython)
  n = 1
  ref = Cd_element
FEATURE [App::DocumentObjectGroupPython] W_element001  label="W_element : 1"  # scripted group (container) (typed FeaturePython)
  n = 1
  ref = W_element
FEATURE [App::DocumentObjectGroupPython] O_element020  label="O_element : 008"  # scripted group (container) (typed FeaturePython)
  n = 4
  ref = O_element
FEATURE [App::DocumentObjectGroupPython] G4_CADMIUM_TUNGSTATE  # scripted group (container) (typed FeaturePython)
  Dunit = g/cm3
  Dvalue = 7.9
  Group = -> [Cd_element002,W_element001,O_element020]
  conduct = 2
  density = 1
  expand = 3
  formula = G4_CADMIUM_TUNGSTATE
  name = G4_CADMIUM_TUNGSTATE
  specific = 4
FEATURE [App::DocumentObjectGroupPython] Ca_element005  label="Ca_element : 1"  # scripted group (container) (typed FeaturePython)
  n = 1
  ref = Ca_element
FEATURE [App::DocumentObjectGroupPython] C_element022  label="C_element : 009"  # scripted group (container) (typed FeaturePython)
  n = 1
  ref = C_element
FEATURE [App::DocumentObjectGroupPython] O_element021  label="O_element : 009"  # scripted group (container) (typed FeaturePython)
  n = 3
  ref = O_element
FEATURE [App::DocumentObjectGroupPython] G4_CALCIUM_CARBONATE  # scripted group (container) (typed FeaturePython)
  Dunit = g/cm3
  Dvalue = 2.8
  Group = -> [Ca_element005,C_element022,O_element021]
  conduct = 2
  density = 1
  expand = 3
  formula = G4_CALCIUM_CARBONATE
  name = G4_CALCIUM_CARBONATE
  specific = 4
FEATURE [App::DocumentObjectGroupPython] Ca_element006  label="Ca_element : 002"  # scripted group (container) (typed FeaturePython)
  n = 1
  ref = Ca_element
FEATURE [App::DocumentObjectGroupPython] F_element005  label="F_element : 003"  # scripted group (container) (typed FeaturePython)
  n = 2
  ref = F_element
FEATURE [App::DocumentObjectGroupPython] G4_CALCIUM_FLUORIDE  # scripted group (container) (typed FeaturePython)
  Dunit = g/cm3
  Dvalue = 3.18
  Group = -> [Ca_element006,F_element005]
  conduct = 2
  density = 1
  expand = 3
  formula = G4_CALCIUM_FLUORIDE
  name = G4_CALCIUM_FLUORIDE
  specific = 4
FEATURE [App::DocumentObjectGroupPython] Ca_element007  label="Ca_element : 003"  # scripted group (container) (typed FeaturePython)
  n = 1
  ref = Ca_element
FEATURE [App::DocumentObjectGroupPython] O_element022  label="O_element : 010"  # scripted group (container) (typed FeaturePython)
  n = 1
  ref = O_element
FEATURE [App::DocumentObjectGroupPython] G4_CALCIUM_OXIDE  # scripted group (container) (typed FeaturePython)
  Dunit = g/cm3
  Dvalue = 3.3
  Group = -> [Ca_element007,O_element022]
  conduct = 2
  density = 1
  expand = 3
  formula = G4_CALCIUM_OXIDE
  name = G4_CALCIUM_OXIDE
  specific = 4
FEATURE [App::DocumentObjectGroupPython] Ca_element008  label="Ca_element : 004"  # scripted group (container) (typed FeaturePython)
  n = 1
  ref = Ca_element
FEATURE [App::DocumentObjectGroupPython] S_element007  label="S_element : 002"  # scripted group (container) (typed FeaturePython)
  n = 1
  ref = S_element
FEATURE [App::DocumentObjectGroupPython] O_element023  label="O_element : 011"  # scripted group (container) (typed FeaturePython)
  n = 4
  ref = O_element
FEATURE [App::DocumentObjectGroupPython] G4_CALCIUM_SULFATE  # scripted group (container) (typed FeaturePython)
  Dunit = g/cm3
  Dvalue = 2.96
  Group = -> [Ca_element008,S_element007,O_element023]
  conduct = 2
  density = 1
  expand = 3
  formula = G4_CALCIUM_SULFATE
  name = G4_CALCIUM_SULFATE
  specific = 4
FEATURE [App::DocumentObjectGroupPython] Ca_element009  label="Ca_element : 005"  # scripted group (container) (typed FeaturePython)
  n = 1
  ref = Ca_element
FEATURE [App::DocumentObjectGroupPython] W_element002  label="W_element : 002"  # scripted group (container) (typed FeaturePython)
  n = 1
  ref = W_element
FEATURE [App::DocumentObjectGroupPython] O_element024  label="O_element : 012"  # scripted group (container) (typed FeaturePython)
  n = 4
  ref = O_element
FEATURE [App::DocumentObjectGroupPython] G4_CALCIUM_TUNGSTATE  # scripted group (container) (typed FeaturePython)
  Dunit = g/cm3
  Dvalue = 6.062
  Group = -> [Ca_element009,W_element002,O_element024]
  conduct = 2
  density = 1
  expand = 3
  formula = G4_CALCIUM_TUNGSTATE
  name = G4_CALCIUM_TUNGSTATE
  specific = 4
FEATURE [App::DocumentObjectGroupPython] C_element023  label="C_element : 010"  # scripted group (container) (typed FeaturePython)
  n = 1
  ref = C_element
FEATURE [App::DocumentObjectGroupPython] O_element025  label="O_element : 013"  # scripted group (container) (typed FeaturePython)
  n = 2
  ref = O_element
FEATURE [App::DocumentObjectGroupPython] G4_CARBON_DIOXIDE  # scripted group (container) (typed FeaturePython)
  Dunit = g/cm3
  Dvalue = 0.00184212
  Group = -> [C_element023,O_element025]
  conduct = 2
  density = 1
  expand = 3
  formula = G4_CARBON_DIOXIDE
  name = G4_CARBON_DIOXIDE
  specific = 4
FEATURE [App::DocumentObjectGroupPython] C_element024  label="C_element : 011"  # scripted group (container) (typed FeaturePython)
  n = 1
  ref = C_element
FEATURE [App::DocumentObjectGroupPython] Cl_element004  label="Cl_element : 4"  # scripted group (container) (typed FeaturePython)
  n = 4
  ref = Cl_element
FEATURE [App::DocumentObjectGroupPython] G4_CARBON_TETRACHLORIDE  # scripted group (container) (typed FeaturePython)
  Dunit = g/cm3
  Dvalue = 1.594
  Group = -> [C_element024,Cl_element004]
  conduct = 2
  density = 1
  expand = 3
  formula = G4_CARBON_TETRACHLORIDE
  name = G4_CARBON_TETRACHLORIDE
  specific = 4
FEATURE [App::DocumentObjectGroupPython] C_element025  label="C_element : 012"  # scripted group (container) (typed FeaturePython)
  n = 6
  ref = C_element
FEATURE [App::DocumentObjectGroupPython] H_element021  label="H_element : 012"  # scripted group (container) (typed FeaturePython)
  n = 10
  ref = H_element
FEATURE [App::DocumentObjectGroupPython] O_element026  label="O_element : 5"  # scripted group (container) (typed FeaturePython)
  n = 5
  ref = O_element
FEATURE [App::DocumentObjectGroupPython] G4_CELLULOSE_CELLOPHANE  # scripted group (container) (typed FeaturePython)
  Dunit = g/cm3
  Dvalue = 1.42
  Group = -> [C_element025,H_element021,O_element026]
  conduct = 2
  density = 1
  expand = 3
  formula = G4_CELLULOSE_CELLOPHANE
  name = G4_CELLULOSE_CELLOPHANE
  specific = 4
FEATURE [App::DocumentObjectGroupPython] H_element022  label="H_element : 0.067"  # scripted group (container) (typed FeaturePython)
  n = 0.067125
FEATURE [App::DocumentObjectGroupPython] C_element026  label="C_element : 0.545"  # scripted group (container) (typed FeaturePython)
  n = 0.545403
FEATURE [App::DocumentObjectGroupPython] O_element027  label="O_element : 0.387"  # scripted group (container) (typed FeaturePython)
  n = 0.387472
FEATURE [App::DocumentObjectGroupPython] G4_CELLULOSE_BUTYRATE  # scripted group (container) (typed FeaturePython)
  Dunit = g/cm3
  Dvalue = 1.2
  Group = -> [H_element022,C_element026,O_element027]
  conduct = 2
  density = 1
  expand = 3
  formula = G4_CELLULOSE_BUTYRATE
  name = G4_CELLULOSE_BUTYRATE
  specific = 4
FEATURE [App::DocumentObjectGroupPython] H_element023  label="H_element : 0.029"  # scripted group (container) (typed FeaturePython)
  n = 0.029216
FEATURE [App::DocumentObjectGroupPython] C_element027  label="C_element : 0.271"  # scripted group (container) (typed FeaturePython)
  n = 0.271296
FEATURE [App::DocumentObjectGroupPython] N_element013  label="N_element : 0.121"  # scripted group (container) (typed FeaturePython)
  n = 0.121276
FEATURE [App::DocumentObjectGroupPython] O_element028  label="O_element : 0.578"  # scripted group (container) (typed FeaturePython)
  n = 0.578212
FEATURE [App::DocumentObjectGroupPython] G4_CELLULOSE_NITRATE  # scripted group (container) (typed FeaturePython)
  Dunit = g/cm3
  Dvalue = 1.49
  Group = -> [H_element023,C_element027,N_element013,O_element028]
  conduct = 2
  density = 1
  expand = 3
  formula = G4_CELLULOSE_NITRATE
  name = G4_CELLULOSE_NITRATE
  specific = 4
FEATURE [App::DocumentObjectGroupPython] H_element024  label="H_element : 0.108"  # scripted group (container) (typed FeaturePython)
  n = 0.107596
FEATURE [App::DocumentObjectGroupPython] N_element014  label="N_element : 0.001"  # scripted group (container) (typed FeaturePython)
  n = 0.0008
FEATURE [App::DocumentObjectGroupPython] O_element029  label="O_element : 0.875"  # scripted group (container) (typed FeaturePython)
  n = 0.874976
FEATURE [App::DocumentObjectGroupPython] S_element008  label="S_element : 0.015"  # scripted group (container) (typed FeaturePython)
  n = 0.014627
FEATURE [App::DocumentObjectGroupPython] Ce_element001  label="Ce_element : 0.002"  # scripted group (container) (typed FeaturePython)
  n = 0.002001
FEATURE [App::DocumentObjectGroupPython] G4_CERIC_SULFATE  # scripted group (container) (typed FeaturePython)
  Dunit = g/cm3
  Dvalue = 1.03
  Group = -> [H_element024,N_element014,O_element029,S_element008,Ce_element001]
  conduct = 2
  density = 1
  expand = 3
  formula = G4_CERIC_SULFATE
  name = G4_CERIC_SULFATE
  specific = 4
FEATURE [App::DocumentObjectGroupPython] Cs_element001  label="Cs_element : 1"  # scripted group (container) (typed FeaturePython)
  n = 1
  ref = Cs_element
FEATURE [App::DocumentObjectGroupPython] F_element006  label="F_element : 1"  # scripted group (container) (typed FeaturePython)
  n = 1
  ref = F_element
FEATURE [App::DocumentObjectGroupPython] G4_CESIUM_FLUORIDE  # scripted group (container) (typed FeaturePython)
  Dunit = g/cm3
  Dvalue = 4.115
  Group = -> [Cs_element001,F_element006]
  conduct = 2
  density = 1
  expand = 3
  formula = G4_CESIUM_FLUORIDE
  name = G4_CESIUM_FLUORIDE
  specific = 4
FEATURE [App::DocumentObjectGroupPython] Cs_element002  label="Cs_element : 002"  # scripted group (container) (typed FeaturePython)
  n = 1
  ref = Cs_element
FEATURE [App::DocumentObjectGroupPython] I_element001  label="I_element : 1"  # scripted group (container) (typed FeaturePython)
  n = 1
  ref = I_element
FEATURE [App::DocumentObjectGroupPython] G4_CESIUM_IODIDE  # scripted group (container) (typed FeaturePython)
  Dunit = g/cm3
  Dvalue = 4.51
  Group = -> [Cs_element002,I_element001]
  conduct = 2
  density = 1
  expand = 3
  formula = G4_CESIUM_IODIDE
  name = G4_CESIUM_IODIDE
  specific = 4
FEATURE [App::DocumentObjectGroupPython] C_element028  label="C_element : 013"  # scripted group (container) (typed FeaturePython)
  n = 6
  ref = C_element
FEATURE [App::DocumentObjectGroupPython] H_element025  label="H_element : 013"  # scripted group (container) (typed FeaturePython)
  n = 5
  ref = H_element
FEATURE [App::DocumentObjectGroupPython] Cl_element005  label="Cl_element : 1"  # scripted group (container) (typed FeaturePython)
  n = 1
  ref = Cl_element
FEATURE [App::DocumentObjectGroupPython] G4_CHLOROBENZENE  # scripted group (container) (typed FeaturePython)
  Dunit = g/cm3
  Dvalue = 1.1058
  Group = -> [C_element028,H_element025,Cl_element005]
  conduct = 2
  density = 1
  expand = 3
  formula = G4_CHLOROBENZENE
  name = G4_CHLOROBENZENE
  specific = 4
FEATURE [App::DocumentObjectGroupPython] C_element029  label="C_element : 014"  # scripted group (container) (typed FeaturePython)
  n = 1
  ref = C_element
FEATURE [App::DocumentObjectGroupPython] H_element026  label="H_element : 1"  # scripted group (container) (typed FeaturePython)
  n = 1
  ref = H_element
FEATURE [App::DocumentObjectGroupPython] Cl_element006  label="Cl_element : 3"  # scripted group (container) (typed FeaturePython)
  n = 3
  ref = Cl_element
FEATURE [App::DocumentObjectGroupPython] G4_CHLOROFORM  # scripted group (container) (typed FeaturePython)
  Dunit = g/cm3
  Dvalue = 1.4832
  Group = -> [C_element029,H_element026,Cl_element006]
  conduct = 2
  density = 1
  expand = 3
  formula = G4_CHLOROFORM
  name = G4_CHLOROFORM
  specific = 4
FEATURE [App::DocumentObjectGroupPython] H_element027  label="H_element : 0.010"  # scripted group (container) (typed FeaturePython)
  n = 0.01
FEATURE [App::DocumentObjectGroupPython] C_element030  label="C_element : 0.001"  # scripted group (container) (typed FeaturePython)
  n = 0.001
FEATURE [App::DocumentObjectGroupPython] O_element030  label="O_element : 0.529"  # scripted group (container) (typed FeaturePython)
  n = 0.529107
FEATURE [App::DocumentObjectGroupPython] Na_element005  label="Na_element : 0.016"  # scripted group (container) (typed FeaturePython)
  n = 0.016
FEATURE [App::DocumentObjectGroupPython] Mg_element003  label="Mg_element : 0.004"  # scripted group (container) (typed FeaturePython)
  n = 0.002
FEATURE [App::DocumentObjectGroupPython] Al_element002  label="Al_element : 0.034"  # scripted group (container) (typed FeaturePython)
  n = 0.033872
FEATURE [App::DocumentObjectGroupPython] Si_element002  label="Si_element : 0.337"  # scripted group (container) (typed FeaturePython)
  n = 0.337021
FEATURE [App::DocumentObjectGroupPython] K_element003  label="K_element : 0.013"  # scripted group (container) (typed FeaturePython)
  n = 0.013
FEATURE [App::DocumentObjectGroupPython] Ca_element010  label="Ca_element : 0.044"  # scripted group (container) (typed FeaturePython)
  n = 0.044
FEATURE [App::DocumentObjectGroupPython] Fe_element002  label="Fe_element : 0.014"  # scripted group (container) (typed FeaturePython)
  n = 0.014
FEATURE [App::DocumentObjectGroupPython] G4_CONCRETE  # scripted group (container) (typed FeaturePython)
  Dunit = g/cm3
  Dvalue = 2.3
  Group = -> [H_element027,C_element030,O_element030,Na_element005,Mg_element003,Al_element002,Si_element002,K_element003,Ca_element010,Fe_element002]
  conduct = 2
  density = 1
  expand = 3
  formula = G4_CONCRETE
  name = G4_CONCRETE
  specific = 4
FEATURE [App::DocumentObjectGroupPython] C_element031  label="C_element : 015"  # scripted group (container) (typed FeaturePython)
  n = 6
  ref = C_element
FEATURE [App::DocumentObjectGroupPython] H_element028  label="H_element : 12"  # scripted group (container) (typed FeaturePython)
  n = 12
  ref = H_element
FEATURE [App::DocumentObjectGroupPython] G4_CYCLOHEXANE  # scripted group (container) (typed FeaturePython)
  Dunit = g/cm3
  Dvalue = 0.779
  Group = -> [C_element031,H_element028]
  conduct = 2
  density = 1
  expand = 3
  formula = G4_CYCLOHEXANE
  name = G4_CYCLOHEXANE
  specific = 4
FEATURE [App::DocumentObjectGroupPython] C_element032  label="C_element : 016"  # scripted group (container) (typed FeaturePython)
  n = 6
  ref = C_element
FEATURE [App::DocumentObjectGroupPython] H_element029  label="H_element : 4"  # scripted group (container) (typed FeaturePython)
  n = 4
  ref = H_element
FEATURE [App::DocumentObjectGroupPython] Cl_element007  label="Cl_element : 2"  # scripted group (container) (typed FeaturePython)
  n = 2
  ref = Cl_element
FEATURE [App::DocumentObjectGroupPython] G4_1_2_DICHLOROBENZENE  label="G4_1.2-DICHLOROBENZENE"  # scripted group (container) (typed FeaturePython)
  Dunit = g/cm3
  Dvalue = 1.3048
  Group = -> [C_element032,H_element029,Cl_element007]
  conduct = 2
  density = 1
  expand = 3
  formula = G4_1.2-DICHLOROBENZENE
  name = G4_1.2-DICHLOROBENZENE
  specific = 4
FEATURE [App::DocumentObjectGroupPython] C_element033  label="C_element : 017"  # scripted group (container) (typed FeaturePython)
  n = 4
  ref = C_element
FEATURE [App::DocumentObjectGroupPython] H_element030  label="H_element : 8"  # scripted group (container) (typed FeaturePython)
  n = 8
  ref = H_element
FEATURE [App::DocumentObjectGroupPython] O_element031  label="O_element : 014"  # scripted group (container) (typed FeaturePython)
  n = 1
  ref = O_element
FEATURE [App::DocumentObjectGroupPython] Cl_element008  label="Cl_element : 005"  # scripted group (container) (typed FeaturePython)
  n = 2
  ref = Cl_element
FEATURE [App::DocumentObjectGroupPython] G4_DICHLORODIETHYL_ETHER  # scripted group (container) (typed FeaturePython)
  Dunit = g/cm3
  Dvalue = 1.2199
  Group = -> [C_element033,H_element030,O_element031,Cl_element008]
  conduct = 2
  density = 1
  expand = 3
  formula = G4_DICHLORODIETHYL_ETHER
  name = G4_DICHLORODIETHYL_ETHER
  specific = 4
FEATURE [App::DocumentObjectGroupPython] C_element034  label="C_element : 018"  # scripted group (container) (typed FeaturePython)
  n = 2
  ref = C_element
FEATURE [App::DocumentObjectGroupPython] H_element031  label="H_element : 014"  # scripted group (container) (typed FeaturePython)
  n = 4
  ref = H_element
FEATURE [App::DocumentObjectGroupPython] Cl_element009  label="Cl_element : 006"  # scripted group (container) (typed FeaturePython)
  n = 2
  ref = Cl_element
FEATURE [App::DocumentObjectGroupPython] G4_1_2_DICHLOROETHANE  label="G4_1.2-DICHLOROETHANE"  # scripted group (container) (typed FeaturePython)
  Dunit = g/cm3
  Dvalue = 1.2351
  Group = -> [C_element034,H_element031,Cl_element009]
  conduct = 2
  density = 1
  expand = 3
  formula = G4_1.2-DICHLOROETHANE
  name = G4_1.2-DICHLOROETHANE
  specific = 4
FEATURE [App::DocumentObjectGroupPython] C_element035  label="C_element : 019"  # scripted group (container) (typed FeaturePython)
  n = 4
  ref = C_element
FEATURE [App::DocumentObjectGroupPython] H_element032  label="H_element : 015"  # scripted group (container) (typed FeaturePython)
  n = 10
  ref = H_element
FEATURE [App::DocumentObjectGroupPython] O_element032  label="O_element : 015"  # scripted group (container) (typed FeaturePython)
  n = 1
  ref = O_element
FEATURE [App::DocumentObjectGroupPython] G4_DIETHYL_ETHER  # scripted group (container) (typed FeaturePython)
  Dunit = g/cm3
  Dvalue = 0.71378
  Group = -> [C_element035,H_element032,O_element032]
  conduct = 2
  density = 1
  expand = 3
  formula = G4_DIETHYL_ETHER
  name = G4_DIETHYL_ETHER
  specific = 4
FEATURE [App::DocumentObjectGroupPython] C_element036  label="C_element : 020"  # scripted group (container) (typed FeaturePython)
  n = 3
  ref = C_element
FEATURE [App::DocumentObjectGroupPython] H_element033  label="H_element : 016"  # scripted group (container) (typed FeaturePython)
  n = 7
  ref = H_element
FEATURE [App::DocumentObjectGroupPython] N_element015  label="N_element : 008"  # scripted group (container) (typed FeaturePython)
  n = 1
  ref = N_element
FEATURE [App::DocumentObjectGroupPython] O_element033  label="O_element : 016"  # scripted group (container) (typed FeaturePython)
  n = 1
  ref = O_element
FEATURE [App::DocumentObjectGroupPython] G4_N_N_DIMETHYL_FORMAMIDE  label="G4_N.N-DIMETHYL_FORMAMIDE"  # scripted group (container) (typed FeaturePython)
  Dunit = g/cm3
  Dvalue = 0.9487
  Group = -> [C_element036,H_element033,N_element015,O_element033]
  conduct = 2
  density = 1
  expand = 3
  formula = G4_N.N-DIMETHYL_FORMAMIDE
  name = G4_N.N-DIMETHYL_FORMAMIDE
  specific = 4
FEATURE [App::DocumentObjectGroupPython] C_element037  label="C_element : 021"  # scripted group (container) (typed FeaturePython)
  n = 2
  ref = C_element
FEATURE [App::DocumentObjectGroupPython] H_element034  label="H_element : 017"  # scripted group (container) (typed FeaturePython)
  n = 6
  ref = H_element
FEATURE [App::DocumentObjectGroupPython] O_element034  label="O_element : 017"  # scripted group (container) (typed FeaturePython)
  n = 1
  ref = O_element
FEATURE [App::DocumentObjectGroupPython] S_element009  label="S_element : 003"  # scripted group (container) (typed FeaturePython)
  n = 1
  ref = S_element
FEATURE [App::DocumentObjectGroupPython] G4_DIMETHYL_SULFOXIDE  # scripted group (container) (typed FeaturePython)
  Dunit = g/cm3
  Dvalue = 1.1014
  Group = -> [C_element037,H_element034,O_element034,S_element009]
  conduct = 2
  density = 1
  expand = 3
  formula = G4_DIMETHYL_SULFOXIDE
  name = G4_DIMETHYL_SULFOXIDE
  specific = 4
FEATURE [App::DocumentObjectGroupPython] C_element038  label="C_element : 022"  # scripted group (container) (typed FeaturePython)
  n = 2
  ref = C_element
FEATURE [App::DocumentObjectGroupPython] H_element035  label="H_element : 018"  # scripted group (container) (typed FeaturePython)
  n = 6
  ref = H_element
FEATURE [App::DocumentObjectGroupPython] G4_ETHANE  # scripted group (container) (typed FeaturePython)
  Dunit = g/cm3
  Dvalue = 0.00125324
  Group = -> [C_element038,H_element035]
  conduct = 2
  density = 1
  expand = 3
  formula = G4_ETHANE
  name = G4_ETHANE
  specific = 4
FEATURE [App::DocumentObjectGroupPython] C_element039  label="C_element : 023"  # scripted group (container) (typed FeaturePython)
  n = 2
  ref = C_element
FEATURE [App::DocumentObjectGroupPython] H_element036  label="H_element : 019"  # scripted group (container) (typed FeaturePython)
  n = 6
  ref = H_element
FEATURE [App::DocumentObjectGroupPython] O_element035  label="O_element : 018"  # scripted group (container) (typed FeaturePython)
  n = 1
  ref = O_element
FEATURE [App::DocumentObjectGroupPython] G4_ETHYL_ALCOHOL  # scripted group (container) (typed FeaturePython)
  Dunit = g/cm3
  Dvalue = 0.7893
  Group = -> [C_element039,H_element036,O_element035]
  conduct = 2
  density = 1
  expand = 3
  formula = G4_ETHYL_ALCOHOL
  name = G4_ETHYL_ALCOHOL
  specific = 4
FEATURE [App::DocumentObjectGroupPython] H_element037  label="H_element : 0.090"  # scripted group (container) (typed FeaturePython)
  n = 0.090027
FEATURE [App::DocumentObjectGroupPython] C_element040  label="C_element : 0.585"  # scripted group (container) (typed FeaturePython)
  n = 0.585182
FEATURE [App::DocumentObjectGroupPython] O_element036  label="O_element : 0.325"  # scripted group (container) (typed FeaturePython)
  n = 0.324791
FEATURE [App::DocumentObjectGroupPython] G4_ETHYL_CELLULOSE  # scripted group (container) (typed FeaturePython)
  Dunit = g/cm3
  Dvalue = 1.13
  Group = -> [H_element037,C_element040,O_element036]
  conduct = 2
  density = 1
  expand = 3
  formula = G4_ETHYL_CELLULOSE
  name = G4_ETHYL_CELLULOSE
  specific = 4
FEATURE [App::DocumentObjectGroupPython] C_element041  label="C_element : 024"  # scripted group (container) (typed FeaturePython)
  n = 2
  ref = C_element
FEATURE [App::DocumentObjectGroupPython] H_element038  label="H_element : 020"  # scripted group (container) (typed FeaturePython)
  n = 4
  ref = H_element
FEATURE [App::DocumentObjectGroupPython] G4_ETHYLENE  # scripted group (container) (typed FeaturePython)
  Dunit = g/cm3
  Dvalue = 0.00117497
  Group = -> [C_element041,H_element038]
  conduct = 2
  density = 1
  expand = 3
  formula = G4_ETHYLENE
  name = G4_ETHYLENE
  specific = 4
FEATURE [App::DocumentObjectGroupPython] H_element039  label="H_element : 0.096"  # scripted group (container) (typed FeaturePython)
  n = 0.096
FEATURE [App::DocumentObjectGroupPython] C_element042  label="C_element : 0.195"  # scripted group (container) (typed FeaturePython)
  n = 0.195
FEATURE [App::DocumentObjectGroupPython] N_element016  label="N_element : 0.057"  # scripted group (container) (typed FeaturePython)
  n = 0.057
FEATURE [App::DocumentObjectGroupPython] O_element037  label="O_element : 0.646"  # scripted group (container) (typed FeaturePython)
  n = 0.646
FEATURE [App::DocumentObjectGroupPython] Na_element006  label="Na_element : 0.017"  # scripted group (container) (typed FeaturePython)
  n = 0.001
FEATURE [App::DocumentObjectGroupPython] P_element005  label="P_element : 0.104"  # scripted group (container) (typed FeaturePython)
  n = 0.001
FEATURE [App::DocumentObjectGroupPython] S_element010  label="S_element : 0.016"  # scripted group (container) (typed FeaturePython)
  n = 0.003
FEATURE [App::DocumentObjectGroupPython] Cl_element010  label="Cl_element : 0.005"  # scripted group (container) (typed FeaturePython)
  n = 0.001
FEATURE [App::DocumentObjectGroupPython] G4_EYE_LENS_ICRP  # scripted group (container) (typed FeaturePython)
  Dunit = g/cm3
  Dvalue = 1.07
  Group = -> [H_element039,C_element042,N_element016,O_element037,Na_element006,P_element005,S_element010,Cl_element010]
  conduct = 2
  density = 1
  expand = 3
  formula = G4_EYE_LENS_ICRP
  name = G4_EYE_LENS_ICRP
  specific = 4
FEATURE [App::DocumentObjectGroupPython] Fe_element003  label="Fe_element : 2"  # scripted group (container) (typed FeaturePython)
  n = 2
  ref = Fe_element
FEATURE [App::DocumentObjectGroupPython] O_element038  label="O_element : 019"  # scripted group (container) (typed FeaturePython)
  n = 3
  ref = O_element
FEATURE [App::DocumentObjectGroupPython] G4_FERRIC_OXIDE  # scripted group (container) (typed FeaturePython)
  Dunit = g/cm3
  Dvalue = 5.2
  Group = -> [Fe_element003,O_element038]
  conduct = 2
  density = 1
  expand = 3
  formula = G4_FERRIC_OXIDE
  name = G4_FERRIC_OXIDE
  specific = 4
FEATURE [App::DocumentObjectGroupPython] Fe_element004  label="Fe_element : 1"  # scripted group (container) (typed FeaturePython)
  n = 1
  ref = Fe_element
FEATURE [App::DocumentObjectGroupPython] B_element003  label="B_element : 1"  # scripted group (container) (typed FeaturePython)
  n = 1
  ref = B_element
FEATURE [App::DocumentObjectGroupPython] G4_FERROBORIDE  # scripted group (container) (typed FeaturePython)
  Dunit = g/cm3
  Dvalue = 7.15
  Group = -> [Fe_element004,B_element003]
  conduct = 2
  density = 1
  expand = 3
  formula = G4_FERROBORIDE
  name = G4_FERROBORIDE
  specific = 4
FEATURE [App::DocumentObjectGroupPython] Fe_element005  label="Fe_element : 003"  # scripted group (container) (typed FeaturePython)
  n = 1
  ref = Fe_element
FEATURE [App::DocumentObjectGroupPython] O_element039  label="O_element : 020"  # scripted group (container) (typed FeaturePython)
  n = 1
  ref = O_element
FEATURE [App::DocumentObjectGroupPython] G4_FERROUS_OXIDE  # scripted group (container) (typed FeaturePython)
  Dunit = g/cm3
  Dvalue = 5.7
  Group = -> [Fe_element005,O_element039]
  conduct = 2
  density = 1
  expand = 3
  formula = G4_FERROUS_OXIDE
  name = G4_FERROUS_OXIDE
  specific = 4
FEATURE [App::DocumentObjectGroupPython] H_element040  label="H_element : 0.115"  # scripted group (container) (typed FeaturePython)
  n = 0.108259
FEATURE [App::DocumentObjectGroupPython] N_element017  label="N_element : 0.000"  # scripted group (container) (typed FeaturePython)
  n = 2.7e-05
FEATURE [App::DocumentObjectGroupPython] O_element040  label="O_element : 0.879"  # scripted group (container) (typed FeaturePython)
  n = 0.878636
FEATURE [App::DocumentObjectGroupPython] Na_element007  label="Na_element : 0.000"  # scripted group (container) (typed FeaturePython)
  n = 2.2e-05
FEATURE [App::DocumentObjectGroupPython] S_element011  label="S_element : 0.013"  # scripted group (container) (typed FeaturePython)
  n = 0.012968
FEATURE [App::DocumentObjectGroupPython] Cl_element011  label="Cl_element : 0.000"  # scripted group (container) (typed FeaturePython)
  n = 3.4e-05
FEATURE [App::DocumentObjectGroupPython] Fe_element006  label="Fe_element : 0.000"  # scripted group (container) (typed FeaturePython)
  n = 5.4e-05
FEATURE [App::DocumentObjectGroupPython] G4_FERROUS_SULFATE  # scripted group (container) (typed FeaturePython)
  Dunit = g/cm3
  Dvalue = 1.024
  Group = -> [H_element040,N_element017,O_element040,Na_element007,S_element011,Cl_element011,Fe_element006]
  conduct = 2
  density = 1
  expand = 3
  formula = G4_FERROUS_SULFATE
  name = G4_FERROUS_SULFATE
  specific = 4
FEATURE [App::DocumentObjectGroupPython] C_element043  label="C_element : 0.099"  # scripted group (container) (typed FeaturePython)
  n = 0.099335
FEATURE [App::DocumentObjectGroupPython] F_element007  label="F_element : 0.314"  # scripted group (container) (typed FeaturePython)
  n = 0.314247
FEATURE [App::DocumentObjectGroupPython] Cl_element012  label="Cl_element : 0.586"  # scripted group (container) (typed FeaturePython)
  n = 0.586418
FEATURE [App::DocumentObjectGroupPython] G4_FREON_12  label="G4_FREON-12"  # scripted group (container) (typed FeaturePython)
  Dunit = g/cm3
  Dvalue = 1.12
  Group = -> [C_element043,F_element007,Cl_element012]
  conduct = 2
  density = 1
  expand = 3
  formula = G4_FREON-12
  name = G4_FREON-12
  specific = 4
FEATURE [App::DocumentObjectGroupPython] C_element044  label="C_element : 0.057"  # scripted group (container) (typed FeaturePython)
  n = 0.057245
FEATURE [App::DocumentObjectGroupPython] F_element008  label="F_element : 0.181"  # scripted group (container) (typed FeaturePython)
  n = 0.181096
FEATURE [App::DocumentObjectGroupPython] Br_element001  label="Br_element : 0.762"  # scripted group (container) (typed FeaturePython)
  n = 0.761659
FEATURE [App::DocumentObjectGroupPython] G4_FREON_12B2  label="G4_FREON-12B2"  # scripted group (container) (typed FeaturePython)
  Dunit = g/cm3
  Dvalue = 1.8
  Group = -> [C_element044,F_element008,Br_element001]
  conduct = 2
  density = 1
  expand = 3
  formula = G4_FREON-12B2
  name = G4_FREON-12B2
  specific = 4
FEATURE [App::DocumentObjectGroupPython] C_element045  label="C_element : 0.115"  # scripted group (container) (typed FeaturePython)
  n = 0.114983
FEATURE [App::DocumentObjectGroupPython] F_element009  label="F_element : 0.546"  # scripted group (container) (typed FeaturePython)
  n = 0.545621
FEATURE [App::DocumentObjectGroupPython] Cl_element013  label="Cl_element : 0.339"  # scripted group (container) (typed FeaturePython)
  n = 0.339396
FEATURE [App::DocumentObjectGroupPython] G4_FREON_13  label="G4_FREON-13"  # scripted group (container) (typed FeaturePython)
  Dunit = g/cm3
  Dvalue = 0.95
  Group = -> [C_element045,F_element009,Cl_element013]
  conduct = 2
  density = 1
  expand = 3
  formula = G4_FREON-13
  name = G4_FREON-13
  specific = 4
FEATURE [App::DocumentObjectGroupPython] C_element046  label="C_element : 025"  # scripted group (container) (typed FeaturePython)
  n = 1
  ref = C_element
FEATURE [App::DocumentObjectGroupPython] F_element010  label="F_element : 3"  # scripted group (container) (typed FeaturePython)
  n = 3
  ref = F_element
FEATURE [App::DocumentObjectGroupPython] Br_element002  label="Br_element : 1"  # scripted group (container) (typed FeaturePython)
  n = 1
  ref = Br_element
FEATURE [App::DocumentObjectGroupPython] G4_FREON_13B1  label="G4_FREON-13B1"  # scripted group (container) (typed FeaturePython)
  Dunit = g/cm3
  Dvalue = 1.5
  Group = -> [C_element046,F_element010,Br_element002]
  conduct = 2
  density = 1
  expand = 3
  formula = G4_FREON-13B1
  name = G4_FREON-13B1
  specific = 4
FEATURE [App::DocumentObjectGroupPython] C_element047  label="C_element : 0.061"  # scripted group (container) (typed FeaturePython)
  n = 0.061309
FEATURE [App::DocumentObjectGroupPython] F_element011  label="F_element : 0.291"  # scripted group (container) (typed FeaturePython)
  n = 0.290924
FEATURE [App::DocumentObjectGroupPython] I_element002  label="I_element : 0.648"  # scripted group (container) (typed FeaturePython)
  n = 0.647767
FEATURE [App::DocumentObjectGroupPython] G4_FREON_13I1  label="G4_FREON-13I1"  # scripted group (container) (typed FeaturePython)
  Dunit = g/cm3
  Dvalue = 1.8
  Group = -> [C_element047,F_element011,I_element002]
  conduct = 2
  density = 1
  expand = 3
  formula = G4_FREON-13I1
  name = G4_FREON-13I1
  specific = 4
FEATURE [App::DocumentObjectGroupPython] Gd_element001  label="Gd_element : 2"  # scripted group (container) (typed FeaturePython)
  n = 2
  ref = Gd_element
FEATURE [App::DocumentObjectGroupPython] O_element041  label="O_element : 021"  # scripted group (container) (typed FeaturePython)
  n = 2
  ref = O_element
FEATURE [App::DocumentObjectGroupPython] S_element012  label="S_element : 004"  # scripted group (container) (typed FeaturePython)
  n = 1
  ref = S_element
FEATURE [App::DocumentObjectGroupPython] G4_GADOLINIUM_OXYSULFIDE  # scripted group (container) (typed FeaturePython)
  Dunit = g/cm3
  Dvalue = 7.44
  Group = -> [Gd_element001,O_element041,S_element012]
  conduct = 2
  density = 1
  expand = 3
  formula = G4_GADOLINIUM_OXYSULFIDE
  name = G4_GADOLINIUM_OXYSULFIDE
  specific = 4
FEATURE [App::DocumentObjectGroupPython] Ga_element001  label="Ga_element : 1"  # scripted group (container) (typed FeaturePython)
  n = 1
  ref = Ga_element
FEATURE [App::DocumentObjectGroupPython] As_element001  label="As_element : 1"  # scripted group (container) (typed FeaturePython)
  n = 1
  ref = As_element
FEATURE [App::DocumentObjectGroupPython] G4_GALLIUM_ARSENIDE  # scripted group (container) (typed FeaturePython)
  Dunit = g/cm3
  Dvalue = 5.31
  Group = -> [Ga_element001,As_element001]
  conduct = 2
  density = 1
  expand = 3
  formula = G4_GALLIUM_ARSENIDE
  name = G4_GALLIUM_ARSENIDE
  specific = 4
FEATURE [App::DocumentObjectGroupPython] H_element041  label="H_element : 0.081"  # scripted group (container) (typed FeaturePython)
  n = 0.08118
FEATURE [App::DocumentObjectGroupPython] C_element048  label="C_element : 0.416"  # scripted group (container) (typed FeaturePython)
  n = 0.41606
FEATURE [App::DocumentObjectGroupPython] N_element018  label="N_element : 0.111"  # scripted group (container) (typed FeaturePython)
  n = 0.11124
FEATURE [App::DocumentObjectGroupPython] O_element042  label="O_element : 0.381"  # scripted group (container) (typed FeaturePython)
  n = 0.38064
FEATURE [App::DocumentObjectGroupPython] S_element013  label="S_element : 0.011"  # scripted group (container) (typed FeaturePython)
  n = 0.01088
FEATURE [App::DocumentObjectGroupPython] G4_GEL_PHOTO_EMULSION  # scripted group (container) (typed FeaturePython)
  Dunit = g/cm3
  Dvalue = 1.2914
  Group = -> [H_element041,C_element048,N_element018,O_element042,S_element013]
  conduct = 2
  density = 1
  expand = 3
  formula = G4_GEL_PHOTO_EMULSION
  name = G4_GEL_PHOTO_EMULSION
  specific = 4
FEATURE [App::DocumentObjectGroupPython] B_element004  label="B_element : 0.040"  # scripted group (container) (typed FeaturePython)
  n = 0.0400639
FEATURE [App::DocumentObjectGroupPython] O_element043  label="O_element : 0.540"  # scripted group (container) (typed FeaturePython)
  n = 0.539561
FEATURE [App::DocumentObjectGroupPython] Na_element008  label="Na_element : 0.028"  # scripted group (container) (typed FeaturePython)
  n = 0.0281909
FEATURE [App::DocumentObjectGroupPython] Al_element003  label="Al_element : 0.012"  # scripted group (container) (typed FeaturePython)
  n = 0.011644
FEATURE [App::DocumentObjectGroupPython] Si_element003  label="Si_element : 0.377"  # scripted group (container) (typed FeaturePython)
  n = 0.377219
FEATURE [App::DocumentObjectGroupPython] K_element004  label="K_element : 0.014"  # scripted group (container) (typed FeaturePython)
  n = 0.00332099
FEATURE [App::DocumentObjectGroupPython] G4_Pyrex_Glass  # scripted group (container) (typed FeaturePython)
  Dunit = g/cm3
  Dvalue = 2.23
  Group = -> [B_element004,O_element043,Na_element008,Al_element003,Si_element003,K_element004]
  conduct = 2
  density = 1
  expand = 3
  formula = G4_Pyrex_Glass
  name = G4_Pyrex_Glass
  specific = 4
FEATURE [App::DocumentObjectGroupPython] O_element044  label="O_element : 0.156"  # scripted group (container) (typed FeaturePython)
  n = 0.156453
FEATURE [App::DocumentObjectGroupPython] Si_element004  label="Si_element : 0.081"  # scripted group (container) (typed FeaturePython)
  n = 0.080866
FEATURE [App::DocumentObjectGroupPython] Ti_element001  label="Ti_element : 0.008"  # scripted group (container) (typed FeaturePython)
  n = 0.008092
FEATURE [App::DocumentObjectGroupPython] As_element002  label="As_element : 0.003"  # scripted group (container) (typed FeaturePython)
  n = 0.002651
FEATURE [App::DocumentObjectGroupPython] Pb_element001  label="Pb_element : 0.752"  # scripted group (container) (typed FeaturePython)
  n = 0.751938
FEATURE [App::DocumentObjectGroupPython] G4_GLASS_LEAD  # scripted group (container) (typed FeaturePython)
  Dunit = g/cm3
  Dvalue = 6.22
  Group = -> [O_element044,Si_element004,Ti_element001,As_element002,Pb_element001]
  conduct = 2
  density = 1
  expand = 3
  formula = G4_GLASS_LEAD
  name = G4_GLASS_LEAD
  specific = 4
FEATURE [App::DocumentObjectGroupPython] O_element045  label="O_element : 0.460"  # scripted group (container) (typed FeaturePython)
  n = 0.4598
FEATURE [App::DocumentObjectGroupPython] Na_element009  label="Na_element : 0.096"  # scripted group (container) (typed FeaturePython)
  n = 0.0964411
FEATURE [App::DocumentObjectGroupPython] Si_element005  label="Si_element : 0.378"  # scripted group (container) (typed FeaturePython)
  n = 0.336553
FEATURE [App::DocumentObjectGroupPython] Ca_element011  label="Ca_element : 0.107"  # scripted group (container) (typed FeaturePython)
  n = 0.107205
FEATURE [App::DocumentObjectGroupPython] G4_GLASS_PLATE  # scripted group (container) (typed FeaturePython)
  Dunit = g/cm3
  Dvalue = 2.4
  Group = -> [O_element045,Na_element009,Si_element005,Ca_element011]
  conduct = 2
  density = 1
  expand = 3
  formula = G4_GLASS_PLATE
  name = G4_GLASS_PLATE
  specific = 4
FEATURE [App::DocumentObjectGroupPython] C_element049  label="C_element : 026"  # scripted group (container) (typed FeaturePython)
  n = 5
  ref = C_element
FEATURE [App::DocumentObjectGroupPython] H_element042  label="H_element : 021"  # scripted group (container) (typed FeaturePython)
  n = 10
  ref = H_element
FEATURE [App::DocumentObjectGroupPython] N_element019  label="N_element : 2"  # scripted group (container) (typed FeaturePython)
  n = 2
  ref = N_element
FEATURE [App::DocumentObjectGroupPython] O_element046  label="O_element : 022"  # scripted group (container) (typed FeaturePython)
  n = 3
  ref = O_element
FEATURE [App::DocumentObjectGroupPython] G4_GLUTAMINE  # scripted group (container) (typed FeaturePython)
  Dunit = g/cm3
  Dvalue = 1.46
  Group = -> [C_element049,H_element042,N_element019,O_element046]
  conduct = 2
  density = 1
  expand = 3
  formula = G4_GLUTAMINE
  name = G4_GLUTAMINE
  specific = 4
FEATURE [App::DocumentObjectGroupPython] C_element050  label="C_element : 027"  # scripted group (container) (typed FeaturePython)
  n = 3
  ref = C_element
FEATURE [App::DocumentObjectGroupPython] H_element043  label="H_element : 022"  # scripted group (container) (typed FeaturePython)
  n = 8
  ref = H_element
FEATURE [App::DocumentObjectGroupPython] O_element047  label="O_element : 023"  # scripted group (container) (typed FeaturePython)
  n = 3
  ref = O_element
FEATURE [App::DocumentObjectGroupPython] G4_GLYCEROL  # scripted group (container) (typed FeaturePython)
  Dunit = g/cm3
  Dvalue = 1.2613
  Group = -> [C_element050,H_element043,O_element047]
  conduct = 2
  density = 1
  expand = 3
  formula = G4_GLYCEROL
  name = G4_GLYCEROL
  specific = 4
FEATURE [App::DocumentObjectGroupPython] C_element051  label="C_element : 028"  # scripted group (container) (typed FeaturePython)
  n = 5
  ref = C_element
FEATURE [App::DocumentObjectGroupPython] H_element044  label="H_element : 023"  # scripted group (container) (typed FeaturePython)
  n = 5
  ref = H_element
FEATURE [App::DocumentObjectGroupPython] N_element020  label="N_element : 009"  # scripted group (container) (typed FeaturePython)
  n = 5
  ref = N_element
FEATURE [App::DocumentObjectGroupPython] O_element048  label="O_element : 024"  # scripted group (container) (typed FeaturePython)
  n = 1
  ref = O_element
FEATURE [App::DocumentObjectGroupPython] G4_GUANINE  # scripted group (container) (typed FeaturePython)
  Dunit = g/cm3
  Dvalue = 2.2
  Group = -> [C_element051,H_element044,N_element020,O_element048]
  conduct = 2
  density = 1
  expand = 3
  formula = G4_GUANINE
  name = G4_GUANINE
  specific = 4
FEATURE [App::DocumentObjectGroupPython] Ca_element012  label="Ca_element : 006"  # scripted group (container) (typed FeaturePython)
  n = 1
  ref = Ca_element
FEATURE [App::DocumentObjectGroupPython] S_element014  label="S_element : 005"  # scripted group (container) (typed FeaturePython)
  n = 1
  ref = S_element
FEATURE [App::DocumentObjectGroupPython] O_element049  label="O_element : 6"  # scripted group (container) (typed FeaturePython)
  n = 6
  ref = O_element
FEATURE [App::DocumentObjectGroupPython] H_element045  label="H_element : 024"  # scripted group (container) (typed FeaturePython)
  n = 4
  ref = H_element
FEATURE [App::DocumentObjectGroupPython] G4_GYPSUM  # scripted group (container) (typed FeaturePython)
  Dunit = g/cm3
  Dvalue = 2.32
  Group = -> [Ca_element012,S_element014,O_element049,H_element045]
  conduct = 2
  density = 1
  expand = 3
  formula = G4_GYPSUM
  name = G4_GYPSUM
  specific = 4
FEATURE [App::DocumentObjectGroupPython] C_element052  label="C_element : 7"  # scripted group (container) (typed FeaturePython)
  n = 7
  ref = C_element
FEATURE [App::DocumentObjectGroupPython] H_element046  label="H_element : 16"  # scripted group (container) (typed FeaturePython)
  n = 16
  ref = H_element
FEATURE [App::DocumentObjectGroupPython] G4_N_HEPTANE  label="G4_N-HEPTANE"  # scripted group (container) (typed FeaturePython)
  Dunit = g/cm3
  Dvalue = 0.68376
  Group = -> [C_element052,H_element046]
  conduct = 2
  density = 1
  expand = 3
  formula = G4_N-HEPTANE
  name = G4_N-HEPTANE
  specific = 4
FEATURE [App::DocumentObjectGroupPython] C_element053  label="C_element : 029"  # scripted group (container) (typed FeaturePython)
  n = 6
  ref = C_element
FEATURE [App::DocumentObjectGroupPython] H_element047  label="H_element : 14"  # scripted group (container) (typed FeaturePython)
  n = 14
  ref = H_element
FEATURE [App::DocumentObjectGroupPython] G4_N_HEXANE  label="G4_N-HEXANE"  # scripted group (container) (typed FeaturePython)
  Dunit = g/cm3
  Dvalue = 0.6603
  Group = -> [C_element053,H_element047]
  conduct = 2
  density = 1
  expand = 3
  formula = G4_N-HEXANE
  name = G4_N-HEXANE
  specific = 4
FEATURE [App::DocumentObjectGroupPython] C_element054  label="C_element : 22"  # scripted group (container) (typed FeaturePython)
  n = 22
  ref = C_element
FEATURE [App::DocumentObjectGroupPython] H_element048  label="H_element : 025"  # scripted group (container) (typed FeaturePython)
  n = 10
  ref = H_element
FEATURE [App::DocumentObjectGroupPython] N_element021  label="N_element : 010"  # scripted group (container) (typed FeaturePython)
  n = 2
  ref = N_element
FEATURE [App::DocumentObjectGroupPython] O_element050  label="O_element : 025"  # scripted group (container) (typed FeaturePython)
  n = 5
  ref = O_element
FEATURE [App::DocumentObjectGroupPython] G4_KAPTON  # scripted group (container) (typed FeaturePython)
  Dunit = g/cm3
  Dvalue = 1.42
  Group = -> [C_element054,H_element048,N_element021,O_element050]
  conduct = 2
  density = 1
  expand = 3
  formula = G4_KAPTON
  name = G4_KAPTON
  specific = 4
FEATURE [App::DocumentObjectGroupPython] La_element001  label="La_element : 1"  # scripted group (container) (typed FeaturePython)
  n = 1
  ref = La_element
FEATURE [App::DocumentObjectGroupPython] Br_element003  label="Br_element : 002"  # scripted group (container) (typed FeaturePython)
  n = 1
  ref = Br_element
FEATURE [App::DocumentObjectGroupPython] O_element051  label="O_element : 026"  # scripted group (container) (typed FeaturePython)
  n = 1
  ref = O_element
FEATURE [App::DocumentObjectGroupPython] G4_LANTHANUM_OXYBROMIDE  # scripted group (container) (typed FeaturePython)
  Dunit = g/cm3
  Dvalue = 6.28
  Group = -> [La_element001,Br_element003,O_element051]
  conduct = 2
  density = 1
  expand = 3
  formula = G4_LANTHANUM_OXYBROMIDE
  name = G4_LANTHANUM_OXYBROMIDE
  specific = 4
FEATURE [App::DocumentObjectGroupPython] La_element002  label="La_element : 2"  # scripted group (container) (typed FeaturePython)
  n = 2
  ref = La_element
FEATURE [App::DocumentObjectGroupPython] O_element052  label="O_element : 027"  # scripted group (container) (typed FeaturePython)
  n = 2
  ref = O_element
FEATURE [App::DocumentObjectGroupPython] S_element015  label="S_element : 006"  # scripted group (container) (typed FeaturePython)
  n = 1
  ref = S_element
FEATURE [App::DocumentObjectGroupPython] G4_LANTHANUM_OXYSULFIDE  # scripted group (container) (typed FeaturePython)
  Dunit = g/cm3
  Dvalue = 5.86
  Group = -> [La_element002,O_element052,S_element015]
  conduct = 2
  density = 1
  expand = 3
  formula = G4_LANTHANUM_OXYSULFIDE
  name = G4_LANTHANUM_OXYSULFIDE
  specific = 4
FEATURE [App::DocumentObjectGroupPython] O_element053  label="O_element : 0.072"  # scripted group (container) (typed FeaturePython)
  n = 0.071682
FEATURE [App::DocumentObjectGroupPython] Pb_element002  label="Pb_element : 0.928"  # scripted group (container) (typed FeaturePython)
  n = 0.928318
FEATURE [App::DocumentObjectGroupPython] G4_LEAD_OXIDE  # scripted group (container) (typed FeaturePython)
  Dunit = g/cm3
  Dvalue = 9.53
  Group = -> [O_element053,Pb_element002]
  conduct = 2
  density = 1
  expand = 3
  formula = G4_LEAD_OXIDE
  name = G4_LEAD_OXIDE
  specific = 4
FEATURE [App::DocumentObjectGroupPython] Li_element001  label="Li_element : 1"  # scripted group (container) (typed FeaturePython)
  n = 1
  ref = Li_element
FEATURE [App::DocumentObjectGroupPython] N_element022  label="N_element : 011"  # scripted group (container) (typed FeaturePython)
  n = 1
  ref = N_element
FEATURE [App::DocumentObjectGroupPython] H_element049  label="H_element : 026"  # scripted group (container) (typed FeaturePython)
  n = 2
  ref = H_element
FEATURE [App::DocumentObjectGroupPython] G4_LITHIUM_AMIDE  # scripted group (container) (typed FeaturePython)
  Dunit = g/cm3
  Dvalue = 1.178
  Group = -> [Li_element001,N_element022,H_element049]
  conduct = 2
  density = 1
  expand = 3
  formula = G4_LITHIUM_AMIDE
  name = G4_LITHIUM_AMIDE
  specific = 4
FEATURE [App::DocumentObjectGroupPython] Li_element002  label="Li_element : 2"  # scripted group (container) (typed FeaturePython)
  n = 2
  ref = Li_element
FEATURE [App::DocumentObjectGroupPython] C_element055  label="C_element : 030"  # scripted group (container) (typed FeaturePython)
  n = 1
  ref = C_element
FEATURE [App::DocumentObjectGroupPython] O_element054  label="O_element : 028"  # scripted group (container) (typed FeaturePython)
  n = 3
  ref = O_element
FEATURE [App::DocumentObjectGroupPython] G4_LITHIUM_CARBONATE  # scripted group (container) (typed FeaturePython)
  Dunit = g/cm3
  Dvalue = 2.11
  Group = -> [Li_element002,C_element055,O_element054]
  conduct = 2
  density = 1
  expand = 3
  formula = G4_LITHIUM_CARBONATE
  name = G4_LITHIUM_CARBONATE
  specific = 4
FEATURE [App::DocumentObjectGroupPython] Li_element003  label="Li_element : 003"  # scripted group (container) (typed FeaturePython)
  n = 1
  ref = Li_element
FEATURE [App::DocumentObjectGroupPython] F_element012  label="F_element : 004"  # scripted group (container) (typed FeaturePython)
  n = 1
  ref = F_element
FEATURE [App::DocumentObjectGroupPython] G4_LITHIUM_FLUORIDE  # scripted group (container) (typed FeaturePython)
  Dunit = g/cm3
  Dvalue = 2.635
  Group = -> [Li_element003,F_element012]
  conduct = 2
  density = 1
  expand = 3
  formula = G4_LITHIUM_FLUORIDE
  name = G4_LITHIUM_FLUORIDE
  specific = 4
FEATURE [App::DocumentObjectGroupPython] Li_element004  label="Li_element : 004"  # scripted group (container) (typed FeaturePython)
  n = 1
  ref = Li_element
FEATURE [App::DocumentObjectGroupPython] H_element050  label="H_element : 027"  # scripted group (container) (typed FeaturePython)
  n = 1
  ref = H_element
FEATURE [App::DocumentObjectGroupPython] G4_LITHIUM_HYDRIDE  # scripted group (container) (typed FeaturePython)
  Dunit = g/cm3
  Dvalue = 0.82
  Group = -> [Li_element004,H_element050]
  conduct = 2
  density = 1
  expand = 3
  formula = G4_LITHIUM_HYDRIDE
  name = G4_LITHIUM_HYDRIDE
  specific = 4
FEATURE [App::DocumentObjectGroupPython] Li_element005  label="Li_element : 005"  # scripted group (container) (typed FeaturePython)
  n = 1
  ref = Li_element
FEATURE [App::DocumentObjectGroupPython] I_element003  label="I_element : 002"  # scripted group (container) (typed FeaturePython)
  n = 1
  ref = I_element
FEATURE [App::DocumentObjectGroupPython] G4_LITHIUM_IODIDE  # scripted group (container) (typed FeaturePython)
  Dunit = g/cm3
  Dvalue = 3.494
  Group = -> [Li_element005,I_element003]
  conduct = 2
  density = 1
  expand = 3
  formula = G4_LITHIUM_IODIDE
  name = G4_LITHIUM_IODIDE
  specific = 4
FEATURE [App::DocumentObjectGroupPython] Li_element006  label="Li_element : 006"  # scripted group (container) (typed FeaturePython)
  n = 2
  ref = Li_element
FEATURE [App::DocumentObjectGroupPython] O_element055  label="O_element : 029"  # scripted group (container) (typed FeaturePython)
  n = 1
  ref = O_element
FEATURE [App::DocumentObjectGroupPython] G4_LITHIUM_OXIDE  # scripted group (container) (typed FeaturePython)
  Dunit = g/cm3
  Dvalue = 2.013
  Group = -> [Li_element006,O_element055]
  conduct = 2
  density = 1
  expand = 3
  formula = G4_LITHIUM_OXIDE
  name = G4_LITHIUM_OXIDE
  specific = 4
FEATURE [App::DocumentObjectGroupPython] Li_element007  label="Li_element : 007"  # scripted group (container) (typed FeaturePython)
  n = 2
  ref = Li_element
FEATURE [App::DocumentObjectGroupPython] B_element005  label="B_element : 005"  # scripted group (container) (typed FeaturePython)
  n = 4
  ref = B_element
FEATURE [App::DocumentObjectGroupPython] O_element056  label="O_element : 7"  # scripted group (container) (typed FeaturePython)
  n = 7
  ref = O_element
FEATURE [App::DocumentObjectGroupPython] G4_LITHIUM_TETRABORATE  # scripted group (container) (typed FeaturePython)
  Dunit = g/cm3
  Dvalue = 2.44
  Group = -> [Li_element007,B_element005,O_element056]
  conduct = 2
  density = 1
  expand = 3
  formula = G4_LITHIUM_TETRABORATE
  name = G4_LITHIUM_TETRABORATE
  specific = 4
FEATURE [App::DocumentObjectGroupPython] H_element051  label="H_element : 0.105"  # scripted group (container) (typed FeaturePython)
  n = 0.105
FEATURE [App::DocumentObjectGroupPython] C_element056  label="C_element : 0.083"  # scripted group (container) (typed FeaturePython)
  n = 0.083
FEATURE [App::DocumentObjectGroupPython] N_element023  label="N_element : 0.023"  # scripted group (container) (typed FeaturePython)
  n = 0.023
FEATURE [App::DocumentObjectGroupPython] O_element057  label="O_element : 0.779"  # scripted group (container) (typed FeaturePython)
  n = 0.779
FEATURE [App::DocumentObjectGroupPython] Na_element010  label="Na_element : 0.097"  # scripted group (container) (typed FeaturePython)
  n = 0.002
FEATURE [App::DocumentObjectGroupPython] P_element006  label="P_element : 0.105"  # scripted group (container) (typed FeaturePython)
  n = 0.001
FEATURE [App::DocumentObjectGroupPython] S_element016  label="S_element : 0.017"  # scripted group (container) (typed FeaturePython)
  n = 0.002
FEATURE [App::DocumentObjectGroupPython] Cl_element014  label="Cl_element : 0.587"  # scripted group (container) (typed FeaturePython)
  n = 0.003
FEATURE [App::DocumentObjectGroupPython] K_element005  label="K_element : 0.015"  # scripted group (container) (typed FeaturePython)
  n = 0.002
FEATURE [App::DocumentObjectGroupPython] G4_LUNG_ICRP  # scripted group (container) (typed FeaturePython)
  Dunit = g/cm3
  Dvalue = 1.04
  Group = -> [H_element051,C_element056,N_element023,O_element057,Na_element010,P_element006,S_element016,Cl_element014,K_element005]
  conduct = 2
  density = 1
  expand = 3
  formula = G4_LUNG_ICRP
  name = G4_LUNG_ICRP
  specific = 4
FEATURE [App::DocumentObjectGroupPython] H_element052  label="H_element : 0.116"  # scripted group (container) (typed FeaturePython)
  n = 0.114318
FEATURE [App::DocumentObjectGroupPython] C_element057  label="C_element : 0.656"  # scripted group (container) (typed FeaturePython)
  n = 0.655824
FEATURE [App::DocumentObjectGroupPython] O_element058  label="O_element : 0.092"  # scripted group (container) (typed FeaturePython)
  n = 0.0921831
FEATURE [App::DocumentObjectGroupPython] Mg_element004  label="Mg_element : 0.135"  # scripted group (container) (typed FeaturePython)
  n = 0.134792
FEATURE [App::DocumentObjectGroupPython] Ca_element013  label="Ca_element : 0.003"  # scripted group (container) (typed FeaturePython)
  n = 0.002883
FEATURE [App::DocumentObjectGroupPython] G4_M3_WAX  # scripted group (container) (typed FeaturePython)
  Dunit = g/cm3
  Dvalue = 1.05
  Group = -> [H_element052,C_element057,O_element058,Mg_element004,Ca_element013]
  conduct = 2
  density = 1
  expand = 3
  formula = G4_M3_WAX
  name = G4_M3_WAX
  specific = 4
FEATURE [App::DocumentObjectGroupPython] Mg_element005  label="Mg_element : 1"  # scripted group (container) (typed FeaturePython)
  n = 1
  ref = Mg_element
FEATURE [App::DocumentObjectGroupPython] C_element058  label="C_element : 031"  # scripted group (container) (typed FeaturePython)
  n = 1
  ref = C_element
FEATURE [App::DocumentObjectGroupPython] O_element059  label="O_element : 030"  # scripted group (container) (typed FeaturePython)
  n = 3
  ref = O_element
FEATURE [App::DocumentObjectGroupPython] G4_MAGNESIUM_CARBONATE  # scripted group (container) (typed FeaturePython)
  Dunit = g/cm3
  Dvalue = 2.958
  Group = -> [Mg_element005,C_element058,O_element059]
  conduct = 2
  density = 1
  expand = 3
  formula = G4_MAGNESIUM_CARBONATE
  name = G4_MAGNESIUM_CARBONATE
  specific = 4
FEATURE [App::DocumentObjectGroupPython] Mg_element006  label="Mg_element : 002"  # scripted group (container) (typed FeaturePython)
  n = 1
  ref = Mg_element
FEATURE [App::DocumentObjectGroupPython] F_element013  label="F_element : 005"  # scripted group (container) (typed FeaturePython)
  n = 2
  ref = F_element
FEATURE [App::DocumentObjectGroupPython] G4_MAGNESIUM_FLUORIDE  # scripted group (container) (typed FeaturePython)
  Dunit = g/cm3
  Dvalue = 3
  Group = -> [Mg_element006,F_element013]
  conduct = 2
  density = 1
  expand = 3
  formula = G4_MAGNESIUM_FLUORIDE
  name = G4_MAGNESIUM_FLUORIDE
  specific = 4
FEATURE [App::DocumentObjectGroupPython] Mg_element007  label="Mg_element : 003"  # scripted group (container) (typed FeaturePython)
  n = 1
  ref = Mg_element
FEATURE [App::DocumentObjectGroupPython] O_element060  label="O_element : 031"  # scripted group (container) (typed FeaturePython)
  n = 1
  ref = O_element
FEATURE [App::DocumentObjectGroupPython] G4_MAGNESIUM_OXIDE  # scripted group (container) (typed FeaturePython)
  Dunit = g/cm3
  Dvalue = 3.58
  Group = -> [Mg_element007,O_element060]
  conduct = 2
  density = 1
  expand = 3
  formula = G4_MAGNESIUM_OXIDE
  name = G4_MAGNESIUM_OXIDE
  specific = 4
FEATURE [App::DocumentObjectGroupPython] Mg_element008  label="Mg_element : 004"  # scripted group (container) (typed FeaturePython)
  n = 1
  ref = Mg_element
FEATURE [App::DocumentObjectGroupPython] B_element006  label="B_element : 006"  # scripted group (container) (typed FeaturePython)
  n = 4
  ref = B_element
FEATURE [App::DocumentObjectGroupPython] O_element061  label="O_element : 032"  # scripted group (container) (typed FeaturePython)
  n = 7
  ref = O_element
FEATURE [App::DocumentObjectGroupPython] G4_MAGNESIUM_TETRABORATE  # scripted group (container) (typed FeaturePython)
  Dunit = g/cm3
  Dvalue = 2.53
  Group = -> [Mg_element008,B_element006,O_element061]
  conduct = 2
  density = 1
  expand = 3
  formula = G4_MAGNESIUM_TETRABORATE
  name = G4_MAGNESIUM_TETRABORATE
  specific = 4
FEATURE [App::DocumentObjectGroupPython] Hg_element001  label="Hg_element : 1"  # scripted group (container) (typed FeaturePython)
  n = 1
  ref = Hg_element
FEATURE [App::DocumentObjectGroupPython] I_element004  label="I_element : 2"  # scripted group (container) (typed FeaturePython)
  n = 2
  ref = I_element
FEATURE [App::DocumentObjectGroupPython] G4_MERCURIC_IODIDE  # scripted group (container) (typed FeaturePython)
  Dunit = g/cm3
  Dvalue = 6.36
  Group = -> [Hg_element001,I_element004]
  conduct = 2
  density = 1
  expand = 3
  formula = G4_MERCURIC_IODIDE
  name = G4_MERCURIC_IODIDE
  specific = 4
FEATURE [App::DocumentObjectGroupPython] C_element059  label="C_element : 032"  # scripted group (container) (typed FeaturePython)
  n = 1
  ref = C_element
FEATURE [App::DocumentObjectGroupPython] H_element053  label="H_element : 028"  # scripted group (container) (typed FeaturePython)
  n = 4
  ref = H_element
FEATURE [App::DocumentObjectGroupPython] G4_METHANE  # scripted group (container) (typed FeaturePython)
  Dunit = g/cm3
  Dvalue = 0.000667151
  Group = -> [C_element059,H_element053]
  conduct = 2
  density = 1
  expand = 3
  formula = G4_METHANE
  name = G4_METHANE
  specific = 4
FEATURE [App::DocumentObjectGroupPython] C_element060  label="C_element : 033"  # scripted group (container) (typed FeaturePython)
  n = 1
  ref = C_element
FEATURE [App::DocumentObjectGroupPython] H_element054  label="H_element : 029"  # scripted group (container) (typed FeaturePython)
  n = 4
  ref = H_element
FEATURE [App::DocumentObjectGroupPython] O_element062  label="O_element : 033"  # scripted group (container) (typed FeaturePython)
  n = 1
  ref = O_element
FEATURE [App::DocumentObjectGroupPython] G4_METHANOL  # scripted group (container) (typed FeaturePython)
  Dunit = g/cm3
  Dvalue = 0.7914
  Group = -> [C_element060,H_element054,O_element062]
  conduct = 2
  density = 1
  expand = 3
  formula = G4_METHANOL
  name = G4_METHANOL
  specific = 4
FEATURE [App::DocumentObjectGroupPython] H_element055  label="H_element : 0.134"  # scripted group (container) (typed FeaturePython)
  n = 0.13404
FEATURE [App::DocumentObjectGroupPython] C_element061  label="C_element : 0.778"  # scripted group (container) (typed FeaturePython)
  n = 0.77796
FEATURE [App::DocumentObjectGroupPython] O_element063  label="O_element : 0.035"  # scripted group (container) (typed FeaturePython)
  n = 0.03502
FEATURE [App::DocumentObjectGroupPython] Mg_element009  label="Mg_element : 0.039"  # scripted group (container) (typed FeaturePython)
  n = 0.038594
FEATURE [App::DocumentObjectGroupPython] Ti_element002  label="Ti_element : 0.014"  # scripted group (container) (typed FeaturePython)
  n = 0.014386
FEATURE [App::DocumentObjectGroupPython] G4_MIX_D_WAX  # scripted group (container) (typed FeaturePython)
  Dunit = g/cm3
  Dvalue = 0.99
  Group = -> [H_element055,C_element061,O_element063,Mg_element009,Ti_element002]
  conduct = 2
  density = 1
  expand = 3
  formula = G4_MIX_D_WAX
  name = G4_MIX_D_WAX
  specific = 4
FEATURE [App::DocumentObjectGroupPython] H_element056  label="H_element : 0.135"  # scripted group (container) (typed FeaturePython)
  n = 0.081192
FEATURE [App::DocumentObjectGroupPython] C_element062  label="C_element : 0.583"  # scripted group (container) (typed FeaturePython)
  n = 0.583442
FEATURE [App::DocumentObjectGroupPython] N_element024  label="N_element : 0.018"  # scripted group (container) (typed FeaturePython)
  n = 0.017798
FEATURE [App::DocumentObjectGroupPython] O_element064  label="O_element : 0.186"  # scripted group (container) (typed FeaturePython)
  n = 0.186381
FEATURE [App::DocumentObjectGroupPython] Mg_element010  label="Mg_element : 0.130"  # scripted group (container) (typed FeaturePython)
  n = 0.130287
FEATURE [App::DocumentObjectGroupPython] Cl_element015  label="Cl_element : 0.588"  # scripted group (container) (typed FeaturePython)
  n = 0.0009
FEATURE [App::DocumentObjectGroupPython] G4_MS20_TISSUE  # scripted group (container) (typed FeaturePython)
  Dunit = g/cm3
  Dvalue = 1
  Group = -> [H_element056,C_element062,N_element024,O_element064,Mg_element010,Cl_element015]
  conduct = 2
  density = 1
  expand = 3
  formula = G4_MS20_TISSUE
  name = G4_MS20_TISSUE
  specific = 4
FEATURE [App::DocumentObjectGroupPython] H_element057  label="H_element : 0.136"  # scripted group (container) (typed FeaturePython)
  n = 0.102
FEATURE [App::DocumentObjectGroupPython] C_element063  label="C_element : 0.143"  # scripted group (container) (typed FeaturePython)
  n = 0.143
FEATURE [App::DocumentObjectGroupPython] N_element025  label="N_element : 0.034"  # scripted group (container) (typed FeaturePython)
  n = 0.034
FEATURE [App::DocumentObjectGroupPython] O_element065  label="O_element : 0.710"  # scripted group (container) (typed FeaturePython)
  n = 0.71
FEATURE [App::DocumentObjectGroupPython] Na_element011  label="Na_element : 0.098"  # scripted group (container) (typed FeaturePython)
  n = 0.001
FEATURE [App::DocumentObjectGroupPython] P_element007  label="P_element : 0.002"  # scripted group (container) (typed FeaturePython)
  n = 0.002
FEATURE [App::DocumentObjectGroupPython] S_element017  label="S_element : 0.018"  # scripted group (container) (typed FeaturePython)
  n = 0.003
FEATURE [App::DocumentObjectGroupPython] Cl_element016  label="Cl_element : 0.589"  # scripted group (container) (typed FeaturePython)
  n = 0.001
FEATURE [App::DocumentObjectGroupPython] K_element006  label="K_element : 0.004"  # scripted group (container) (typed FeaturePython)
  n = 0.004
FEATURE [App::DocumentObjectGroupPython] G4_MUSCLE_SKELETAL_ICRP  # scripted group (container) (typed FeaturePython)
  Dunit = g/cm3
  Dvalue = 1.05
  Group = -> [H_element057,C_element063,N_element025,O_element065,Na_element011,P_element007,S_element017,Cl_element016,K_element006]
  conduct = 2
  density = 1
  expand = 3
  formula = G4_MUSCLE_SKELETAL_ICRP
  name = G4_MUSCLE_SKELETAL_ICRP
  specific = 4
FEATURE [App::DocumentObjectGroupPython] H_element058  label="H_element : 0.137"  # scripted group (container) (typed FeaturePython)
  n = 0.102102
FEATURE [App::DocumentObjectGroupPython] C_element064  label="C_element : 0.123"  # scripted group (container) (typed FeaturePython)
  n = 0.123123
FEATURE [App::DocumentObjectGroupPython] N_element026  label="N_element : 0.756"  # scripted group (container) (typed FeaturePython)
  n = 0.035035
FEATURE [App::DocumentObjectGroupPython] O_element066  label="O_element : 0.730"  # scripted group (container) (typed FeaturePython)
  n = 0.72973
FEATURE [App::DocumentObjectGroupPython] Na_element012  label="Na_element : 0.099"  # scripted group (container) (typed FeaturePython)
  n = 0.001001
FEATURE [App::DocumentObjectGroupPython] P_element008  label="P_element : 0.106"  # scripted group (container) (typed FeaturePython)
  n = 0.002002
FEATURE [App::DocumentObjectGroupPython] S_element018  label="S_element : 0.019"  # scripted group (container) (typed FeaturePython)
  n = 0.004004
FEATURE [App::DocumentObjectGroupPython] K_element007  label="K_element : 0.016"  # scripted group (container) (typed FeaturePython)
  n = 0.003003
FEATURE [App::DocumentObjectGroupPython] G4_MUSCLE_STRIATED_ICRU  # scripted group (container) (typed FeaturePython)
  Dunit = g/cm3
  Dvalue = 1.04
  Group = -> [H_element058,C_element064,N_element026,O_element066,Na_element012,P_element008,S_element018,K_element007]
  conduct = 2
  density = 1
  expand = 3
  formula = G4_MUSCLE_STRIATED_ICRU
  name = G4_MUSCLE_STRIATED_ICRU
  specific = 4
FEATURE [App::DocumentObjectGroupPython] H_element059  label="H_element : 0.098"  # scripted group (container) (typed FeaturePython)
  n = 0.0982341
FEATURE [App::DocumentObjectGroupPython] C_element065  label="C_element : 0.156"  # scripted group (container) (typed FeaturePython)
  n = 0.156214
FEATURE [App::DocumentObjectGroupPython] N_element027  label="N_element : 0.757"  # scripted group (container) (typed FeaturePython)
  n = 0.035451
FEATURE [App::DocumentObjectGroupPython] O_element067  label="O_element : 0.880"  # scripted group (container) (typed FeaturePython)
  n = 0.710101
FEATURE [App::DocumentObjectGroupPython] G4_MUSCLE_WITH_SUCROSE  # scripted group (container) (typed FeaturePython)
  Dunit = g/cm3
  Dvalue = 1.11
  Group = -> [H_element059,C_element065,N_element027,O_element067]
  conduct = 2
  density = 1
  expand = 3
  formula = G4_MUSCLE_WITH_SUCROSE
  name = G4_MUSCLE_WITH_SUCROSE
  specific = 4
FEATURE [App::DocumentObjectGroupPython] H_element060  label="H_element : 0.138"  # scripted group (container) (typed FeaturePython)
  n = 0.101969
FEATURE [App::DocumentObjectGroupPython] C_element066  label="C_element : 0.120"  # scripted group (container) (typed FeaturePython)
  n = 0.120058
FEATURE [App::DocumentObjectGroupPython] N_element028  label="N_element : 0.758"  # scripted group (container) (typed FeaturePython)
  n = 0.035451
FEATURE [App::DocumentObjectGroupPython] O_element068  label="O_element : 0.743"  # scripted group (container) (typed FeaturePython)
  n = 0.742522
FEATURE [App::DocumentObjectGroupPython] G4_MUSCLE_WITHOUT_SUCROSE  # scripted group (container) (typed FeaturePython)
  Dunit = g/cm3
  Dvalue = 1.07
  Group = -> [H_element060,C_element066,N_element028,O_element068]
  conduct = 2
  density = 1
  expand = 3
  formula = G4_MUSCLE_WITHOUT_SUCROSE
  name = G4_MUSCLE_WITHOUT_SUCROSE
  specific = 4
FEATURE [App::DocumentObjectGroupPython] C_element067  label="C_element : 10"  # scripted group (container) (typed FeaturePython)
  n = 10
  ref = C_element
FEATURE [App::DocumentObjectGroupPython] H_element061  label="H_element : 030"  # scripted group (container) (typed FeaturePython)
  n = 8
  ref = H_element
FEATURE [App::DocumentObjectGroupPython] G4_NAPHTHALENE  # scripted group (container) (typed FeaturePython)
  Dunit = g/cm3
  Dvalue = 1.145
  Group = -> [C_element067,H_element061]
  conduct = 2
  density = 1
  expand = 3
  formula = G4_NAPHTHALENE
  name = G4_NAPHTHALENE
  specific = 4
FEATURE [App::DocumentObjectGroupPython] C_element068  label="C_element : 034"  # scripted group (container) (typed FeaturePython)
  n = 6
  ref = C_element
FEATURE [App::DocumentObjectGroupPython] H_element062  label="H_element : 031"  # scripted group (container) (typed FeaturePython)
  n = 5
  ref = H_element
FEATURE [App::DocumentObjectGroupPython] N_element029  label="N_element : 012"  # scripted group (container) (typed FeaturePython)
  n = 1
  ref = N_element
FEATURE [App::DocumentObjectGroupPython] O_element069  label="O_element : 034"  # scripted group (container) (typed FeaturePython)
  n = 2
  ref = O_element
FEATURE [App::DocumentObjectGroupPython] G4_NITROBENZENE  # scripted group (container) (typed FeaturePython)
  Dunit = g/cm3
  Dvalue = 1.19867
  Group = -> [C_element068,H_element062,N_element029,O_element069]
  conduct = 2
  density = 1
  expand = 3
  formula = G4_NITROBENZENE
  name = G4_NITROBENZENE
  specific = 4
FEATURE [App::DocumentObjectGroupPython] N_element030  label="N_element : 013"  # scripted group (container) (typed FeaturePython)
  n = 2
  ref = N_element
FEATURE [App::DocumentObjectGroupPython] O_element070  label="O_element : 035"  # scripted group (container) (typed FeaturePython)
  n = 1
  ref = O_element
FEATURE [App::DocumentObjectGroupPython] G4_NITROUS_OXIDE  # scripted group (container) (typed FeaturePython)
  Dunit = g/cm3
  Dvalue = 0.00183094
  Group = -> [N_element030,O_element070]
  conduct = 2
  density = 1
  expand = 3
  formula = G4_NITROUS_OXIDE
  name = G4_NITROUS_OXIDE
  specific = 4
FEATURE [App::DocumentObjectGroupPython] H_element063  label="H_element : 0.104"  # scripted group (container) (typed FeaturePython)
  n = 0.103509
FEATURE [App::DocumentObjectGroupPython] C_element069  label="C_element : 0.648"  # scripted group (container) (typed FeaturePython)
  n = 0.648416
FEATURE [App::DocumentObjectGroupPython] N_element031  label="N_element : 0.100"  # scripted group (container) (typed FeaturePython)
  n = 0.0995361
FEATURE [App::DocumentObjectGroupPython] O_element071  label="O_element : 0.149"  # scripted group (container) (typed FeaturePython)
  n = 0.148539
FEATURE [App::DocumentObjectGroupPython] G4_NYLON_8062  label="G4_NYLON-8062"  # scripted group (container) (typed FeaturePython)
  Dunit = g/cm3
  Dvalue = 1.08
  Group = -> [H_element063,C_element069,N_element031,O_element071]
  conduct = 2
  density = 1
  expand = 3
  formula = G4_NYLON-8062
  name = G4_NYLON-8062
  specific = 4
FEATURE [App::DocumentObjectGroupPython] C_element070  label="C_element : 035"  # scripted group (container) (typed FeaturePython)
  n = 6
  ref = C_element
FEATURE [App::DocumentObjectGroupPython] H_element064  label="H_element : 11"  # scripted group (container) (typed FeaturePython)
  n = 11
  ref = H_element
FEATURE [App::DocumentObjectGroupPython] N_element032  label="N_element : 014"  # scripted group (container) (typed FeaturePython)
  n = 1
  ref = N_element
FEATURE [App::DocumentObjectGroupPython] O_element072  label="O_element : 036"  # scripted group (container) (typed FeaturePython)
  n = 1
  ref = O_element
FEATURE [App::DocumentObjectGroupPython] G4_NYLON_6_6  label="G4_NYLON-6-6"  # scripted group (container) (typed FeaturePython)
  Dunit = g/cm3
  Dvalue = 1.14
  Group = -> [C_element070,H_element064,N_element032,O_element072]
  conduct = 2
  density = 1
  expand = 3
  formula = G4_NYLON-6-6
  name = G4_NYLON-6-6
  specific = 4
FEATURE [App::DocumentObjectGroupPython] H_element065  label="H_element : 0.139"  # scripted group (container) (typed FeaturePython)
  n = 0.107062
FEATURE [App::DocumentObjectGroupPython] C_element071  label="C_element : 0.680"  # scripted group (container) (typed FeaturePython)
  n = 0.680449
FEATURE [App::DocumentObjectGroupPython] N_element033  label="N_element : 0.099"  # scripted group (container) (typed FeaturePython)
  n = 0.099189
FEATURE [App::DocumentObjectGroupPython] O_element073  label="O_element : 0.113"  # scripted group (container) (typed FeaturePython)
  n = 0.1133
FEATURE [App::DocumentObjectGroupPython] G4_NYLON_6_10  label="G4_NYLON-6-10"  # scripted group (container) (typed FeaturePython)
  Dunit = g/cm3
  Dvalue = 1.14
  Group = -> [H_element065,C_element071,N_element033,O_element073]
  conduct = 2
  density = 1
  expand = 3
  formula = G4_NYLON-6-10
  name = G4_NYLON-6-10
  specific = 4
FEATURE [App::DocumentObjectGroupPython] H_element066  label="H_element : 0.140"  # scripted group (container) (typed FeaturePython)
  n = 0.115476
FEATURE [App::DocumentObjectGroupPython] C_element072  label="C_element : 0.721"  # scripted group (container) (typed FeaturePython)
  n = 0.720818
FEATURE [App::DocumentObjectGroupPython] N_element034  label="N_element : 0.076"  # scripted group (container) (typed FeaturePython)
  n = 0.0764169
FEATURE [App::DocumentObjectGroupPython] O_element074  label="O_element : 0.087"  # scripted group (container) (typed FeaturePython)
  n = 0.0872889
FEATURE [App::DocumentObjectGroupPython] G4_NYLON_11_RILSAN  label="G4_NYLON-11_RILSAN"  # scripted group (container) (typed FeaturePython)
  Dunit = g/cm3
  Dvalue = 1.425
  Group = -> [H_element066,C_element072,N_element034,O_element074]
  conduct = 2
  density = 1
  expand = 3
  formula = G4_NYLON-11_RILSAN
  name = G4_NYLON-11_RILSAN
  specific = 4
FEATURE [App::DocumentObjectGroupPython] C_element073  label="C_element : 8"  # scripted group (container) (typed FeaturePython)
  n = 8
  ref = C_element
FEATURE [App::DocumentObjectGroupPython] H_element067  label="H_element : 18"  # scripted group (container) (typed FeaturePython)
  n = 18
  ref = H_element
FEATURE [App::DocumentObjectGroupPython] G4_OCTANE  # scripted group (container) (typed FeaturePython)
  Dunit = g/cm3
  Dvalue = 0.7026
  Group = -> [C_element073,H_element067]
  conduct = 2
  density = 1
  expand = 3
  formula = G4_OCTANE
  name = G4_OCTANE
  specific = 4
FEATURE [App::DocumentObjectGroupPython] C_element074  label="C_element : 25"  # scripted group (container) (typed FeaturePython)
  n = 25
  ref = C_element
FEATURE [App::DocumentObjectGroupPython] H_element068  label="H_element : 52"  # scripted group (container) (typed FeaturePython)
  n = 52
  ref = H_element
FEATURE [App::DocumentObjectGroupPython] G4_PARAFFIN  # scripted group (container) (typed FeaturePython)
  Dunit = g/cm3
  Dvalue = 0.93
  Group = -> [C_element074,H_element068]
  conduct = 2
  density = 1
  expand = 3
  formula = G4_PARAFFIN
  name = G4_PARAFFIN
  specific = 4
FEATURE [App::DocumentObjectGroupPython] C_element075  label="C_element : 036"  # scripted group (container) (typed FeaturePython)
  n = 5
  ref = C_element
FEATURE [App::DocumentObjectGroupPython] H_element069  label="H_element : 032"  # scripted group (container) (typed FeaturePython)
  n = 12
  ref = H_element
FEATURE [App::DocumentObjectGroupPython] G4_N_PENTANE  label="G4_N-PENTANE"  # scripted group (container) (typed FeaturePython)
  Dunit = g/cm3
  Dvalue = 0.6262
  Group = -> [C_element075,H_element069]
  conduct = 2
  density = 1
  expand = 3
  formula = G4_N-PENTANE
  name = G4_N-PENTANE
  specific = 4
FEATURE [App::DocumentObjectGroupPython] H_element070  label="H_element : 0.014"  # scripted group (container) (typed FeaturePython)
  n = 0.0141
FEATURE [App::DocumentObjectGroupPython] C_element076  label="C_element : 0.072"  # scripted group (container) (typed FeaturePython)
  n = 0.072261
FEATURE [App::DocumentObjectGroupPython] N_element035  label="N_element : 0.019"  # scripted group (container) (typed FeaturePython)
  n = 0.01932
FEATURE [App::DocumentObjectGroupPython] O_element075  label="O_element : 0.066"  # scripted group (container) (typed FeaturePython)
  n = 0.066101
FEATURE [App::DocumentObjectGroupPython] S_element019  label="S_element : 0.020"  # scripted group (container) (typed FeaturePython)
  n = 0.00189
FEATURE [App::DocumentObjectGroupPython] Br_element004  label="Br_element : 0.349"  # scripted group (container) (typed FeaturePython)
  n = 0.349103
FEATURE [App::DocumentObjectGroupPython] Ag_element001  label="Ag_element : 0.474"  # scripted group (container) (typed FeaturePython)
  n = 0.474105
FEATURE [App::DocumentObjectGroupPython] I_element005  label="I_element : 0.003"  # scripted group (container) (typed FeaturePython)
  n = 0.00312
FEATURE [App::DocumentObjectGroupPython] G4_PHOTO_EMULSION  # scripted group (container) (typed FeaturePython)
  Dunit = g/cm3
  Dvalue = 3.815
  Group = -> [H_element070,C_element076,N_element035,O_element075,S_element019,Br_element004,Ag_element001,I_element005]
  conduct = 2
  density = 1
  expand = 3
  formula = G4_PHOTO_EMULSION
  name = G4_PHOTO_EMULSION
  specific = 4
FEATURE [App::DocumentObjectGroupPython] C_element077  label="C_element : 9"  # scripted group (container) (typed FeaturePython)
  n = 9
  ref = C_element
FEATURE [App::DocumentObjectGroupPython] H_element071  label="H_element : 033"  # scripted group (container) (typed FeaturePython)
  n = 10
  ref = H_element
FEATURE [App::DocumentObjectGroupPython] G4_PLASTIC_SC_VINYLTOLUENE  # scripted group (container) (typed FeaturePython)
  Dunit = g/cm3
  Dvalue = 1.032
  Group = -> [C_element077,H_element071]
  conduct = 2
  density = 1
  expand = 3
  formula = G4_PLASTIC_SC_VINYLTOLUENE
  name = G4_PLASTIC_SC_VINYLTOLUENE
  specific = 4
FEATURE [App::DocumentObjectGroupPython] Pu_element001  label="Pu_element : 1"  # scripted group (container) (typed FeaturePython)
  n = 1
  ref = Pu_element
FEATURE [App::DocumentObjectGroupPython] O_element076  label="O_element : 037"  # scripted group (container) (typed FeaturePython)
  n = 2
  ref = O_element
FEATURE [App::DocumentObjectGroupPython] G4_PLUTONIUM_DIOXIDE  # scripted group (container) (typed FeaturePython)
  Dunit = g/cm3
  Dvalue = 11.46
  Group = -> [Pu_element001,O_element076]
  conduct = 2
  density = 1
  expand = 3
  formula = G4_PLUTONIUM_DIOXIDE
  name = G4_PLUTONIUM_DIOXIDE
  specific = 4
FEATURE [App::DocumentObjectGroupPython] C_element078  label="C_element : 037"  # scripted group (container) (typed FeaturePython)
  n = 3
  ref = C_element
FEATURE [App::DocumentObjectGroupPython] H_element072  label="H_element : 034"  # scripted group (container) (typed FeaturePython)
  n = 3
  ref = H_element
FEATURE [App::DocumentObjectGroupPython] N_element036  label="N_element : 015"  # scripted group (container) (typed FeaturePython)
  n = 1
  ref = N_element
FEATURE [App::DocumentObjectGroupPython] G4_POLYACRYLONITRILE  # scripted group (container) (typed FeaturePython)
  Dunit = g/cm3
  Dvalue = 1.17
  Group = -> [C_element078,H_element072,N_element036]
  conduct = 2
  density = 1
  expand = 3
  formula = G4_POLYACRYLONITRILE
  name = G4_POLYACRYLONITRILE
  specific = 4
FEATURE [App::DocumentObjectGroupPython] C_element079  label="C_element : 16"  # scripted group (container) (typed FeaturePython)
  n = 16
  ref = C_element
FEATURE [App::DocumentObjectGroupPython] H_element073  label="H_element : 035"  # scripted group (container) (typed FeaturePython)
  n = 14
  ref = H_element
FEATURE [App::DocumentObjectGroupPython] O_element077  label="O_element : 038"  # scripted group (container) (typed FeaturePython)
  n = 3
  ref = O_element
FEATURE [App::DocumentObjectGroupPython] G4_POLYCARBONATE  # scripted group (container) (typed FeaturePython)
  Dunit = g/cm3
  Dvalue = 1.2
  Group = -> [C_element079,H_element073,O_element077]
  conduct = 2
  density = 1
  expand = 3
  formula = G4_POLYCARBONATE
  name = G4_POLYCARBONATE
  specific = 4
FEATURE [App::DocumentObjectGroupPython] C_element080  label="C_element : 038"  # scripted group (container) (typed FeaturePython)
  n = 8
  ref = C_element
FEATURE [App::DocumentObjectGroupPython] H_element074  label="H_element : 036"  # scripted group (container) (typed FeaturePython)
  n = 7
  ref = H_element
FEATURE [App::DocumentObjectGroupPython] Cl_element017  label="Cl_element : 007"  # scripted group (container) (typed FeaturePython)
  n = 1
  ref = Cl_element
FEATURE [App::DocumentObjectGroupPython] G4_POLYCHLOROSTYRENE  # scripted group (container) (typed FeaturePython)
  Dunit = g/cm3
  Dvalue = 1.3
  Group = -> [C_element080,H_element074,Cl_element017]
  conduct = 2
  density = 1
  expand = 3
  formula = G4_POLYCHLOROSTYRENE
  name = G4_POLYCHLOROSTYRENE
  specific = 4
FEATURE [App::DocumentObjectGroupPython] C_element081  label="C_element : 039"  # scripted group (container) (typed FeaturePython)
  n = 1
  ref = C_element
FEATURE [App::DocumentObjectGroupPython] H_element075  label="H_element : 037"  # scripted group (container) (typed FeaturePython)
  n = 2
  ref = H_element
FEATURE [App::DocumentObjectGroupPython] G4_POLYETHYLENE  # scripted group (container) (typed FeaturePython)
  Dunit = g/cm3
  Dvalue = 0.94
  Group = -> [C_element081,H_element075]
  conduct = 2
  density = 1
  expand = 3
  formula = G4_POLYETHYLENE
  name = G4_POLYETHYLENE
  specific = 4
FEATURE [App::DocumentObjectGroupPython] C_element082  label="C_element : 040"  # scripted group (container) (typed FeaturePython)
  n = 10
  ref = C_element
FEATURE [App::DocumentObjectGroupPython] H_element076  label="H_element : 038"  # scripted group (container) (typed FeaturePython)
  n = 8
  ref = H_element
FEATURE [App::DocumentObjectGroupPython] O_element078  label="O_element : 039"  # scripted group (container) (typed FeaturePython)
  n = 4
  ref = O_element
FEATURE [App::DocumentObjectGroupPython] G4_MYLAR  # scripted group (container) (typed FeaturePython)
  Dunit = g/cm3
  Dvalue = 1.4
  Group = -> [C_element082,H_element076,O_element078]
  conduct = 2
  density = 1
  expand = 3
  formula = G4_MYLAR
  name = G4_MYLAR
  specific = 4
FEATURE [App::DocumentObjectGroupPython] C_element083  label="C_element : 041"  # scripted group (container) (typed FeaturePython)
  n = 5
  ref = C_element
FEATURE [App::DocumentObjectGroupPython] H_element077  label="H_element : 039"  # scripted group (container) (typed FeaturePython)
  n = 8
  ref = H_element
FEATURE [App::DocumentObjectGroupPython] O_element079  label="O_element : 040"  # scripted group (container) (typed FeaturePython)
  n = 2
  ref = O_element
FEATURE [App::DocumentObjectGroupPython] G4_PLEXIGLASS  # scripted group (container) (typed FeaturePython)
  Dunit = g/cm3
  Dvalue = 1.19
  Group = -> [C_element083,H_element077,O_element079]
  conduct = 2
  density = 1
  expand = 3
  formula = G4_PLEXIGLASS
  name = G4_PLEXIGLASS
  specific = 4
FEATURE [App::DocumentObjectGroupPython] C_element084  label="C_element : 042"  # scripted group (container) (typed FeaturePython)
  n = 1
  ref = C_element
FEATURE [App::DocumentObjectGroupPython] H_element078  label="H_element : 040"  # scripted group (container) (typed FeaturePython)
  n = 2
  ref = H_element
FEATURE [App::DocumentObjectGroupPython] O_element080  label="O_element : 041"  # scripted group (container) (typed FeaturePython)
  n = 1
  ref = O_element
FEATURE [App::DocumentObjectGroupPython] G4_POLYOXYMETHYLENE  # scripted group (container) (typed FeaturePython)
  Dunit = g/cm3
  Dvalue = 1.425
  Group = -> [C_element084,H_element078,O_element080]
  conduct = 2
  density = 1
  expand = 3
  formula = G4_POLYOXYMETHYLENE
  name = G4_POLYOXYMETHYLENE
  specific = 4
FEATURE [App::DocumentObjectGroupPython] C_element085  label="C_element : 043"  # scripted group (container) (typed FeaturePython)
  n = 2
  ref = C_element
FEATURE [App::DocumentObjectGroupPython] H_element079  label="H_element : 041"  # scripted group (container) (typed FeaturePython)
  n = 4
  ref = H_element
FEATURE [App::DocumentObjectGroupPython] G4_POLYPROPYLENE  # scripted group (container) (typed FeaturePython)
  Dunit = g/cm3
  Dvalue = 0.9
  Group = -> [C_element085,H_element079]
  conduct = 2
  density = 1
  expand = 3
  formula = G4_POLYPROPYLENE
  name = G4_POLYPROPYLENE
  specific = 4
FEATURE [App::DocumentObjectGroupPython] C_element086  label="C_element : 044"  # scripted group (container) (typed FeaturePython)
  n = 8
  ref = C_element
FEATURE [App::DocumentObjectGroupPython] H_element080  label="H_element : 042"  # scripted group (container) (typed FeaturePython)
  n = 8
  ref = H_element
FEATURE [App::DocumentObjectGroupPython] G4_POLYSTYRENE  # scripted group (container) (typed FeaturePython)
  Dunit = g/cm3
  Dvalue = 1.06
  Group = -> [C_element086,H_element080]
  conduct = 2
  density = 1
  expand = 3
  formula = G4_POLYSTYRENE
  name = G4_POLYSTYRENE
  specific = 4
FEATURE [App::DocumentObjectGroupPython] C_element087  label="C_element : 045"  # scripted group (container) (typed FeaturePython)
  n = 2
  ref = C_element
FEATURE [App::DocumentObjectGroupPython] F_element014  label="F_element : 4"  # scripted group (container) (typed FeaturePython)
  n = 4
  ref = F_element
FEATURE [App::DocumentObjectGroupPython] G4_TEFLON  # scripted group (container) (typed FeaturePython)
  Dunit = g/cm3
  Dvalue = 2.2
  Group = -> [C_element087,F_element014]
  conduct = 2
  density = 1
  expand = 3
  formula = G4_TEFLON
  name = G4_TEFLON
  specific = 4
FEATURE [App::DocumentObjectGroupPython] C_element088  label="C_element : 046"  # scripted group (container) (typed FeaturePython)
  n = 2
  ref = C_element
FEATURE [App::DocumentObjectGroupPython] F_element015  label="F_element : 006"  # scripted group (container) (typed FeaturePython)
  n = 3
  ref = F_element
FEATURE [App::DocumentObjectGroupPython] Cl_element018  label="Cl_element : 008"  # scripted group (container) (typed FeaturePython)
  n = 1
  ref = Cl_element
FEATURE [App::DocumentObjectGroupPython] G4_POLYTRIFLUOROCHLOROETHYLENE  # scripted group (container) (typed FeaturePython)
  Dunit = g/cm3
  Dvalue = 2.1
  Group = -> [C_element088,F_element015,Cl_element018]
  conduct = 2
  density = 1
  expand = 3
  formula = G4_POLYTRIFLUOROCHLOROETHYLENE
  name = G4_POLYTRIFLUOROCHLOROETHYLENE
  specific = 4
FEATURE [App::DocumentObjectGroupPython] C_element089  label="C_element : 047"  # scripted group (container) (typed FeaturePython)
  n = 4
  ref = C_element
FEATURE [App::DocumentObjectGroupPython] H_element081  label="H_element : 043"  # scripted group (container) (typed FeaturePython)
  n = 6
  ref = H_element
FEATURE [App::DocumentObjectGroupPython] O_element081  label="O_element : 042"  # scripted group (container) (typed FeaturePython)
  n = 2
  ref = O_element
FEATURE [App::DocumentObjectGroupPython] G4_POLYVINYL_ACETATE  # scripted group (container) (typed FeaturePython)
  Dunit = g/cm3
  Dvalue = 1.19
  Group = -> [C_element089,H_element081,O_element081]
  conduct = 2
  density = 1
  expand = 3
  formula = G4_POLYVINYL_ACETATE
  name = G4_POLYVINYL_ACETATE
  specific = 4
FEATURE [App::DocumentObjectGroupPython] C_element090  label="C_element : 048"  # scripted group (container) (typed FeaturePython)
  n = 2
  ref = C_element
FEATURE [App::DocumentObjectGroupPython] H_element082  label="H_element : 044"  # scripted group (container) (typed FeaturePython)
  n = 4
  ref = H_element
FEATURE [App::DocumentObjectGroupPython] O_element082  label="O_element : 043"  # scripted group (container) (typed FeaturePython)
  n = 1
  ref = O_element
FEATURE [App::DocumentObjectGroupPython] G4_POLYVINYL_ALCOHOL  # scripted group (container) (typed FeaturePython)
  Dunit = g/cm3
  Dvalue = 1.3
  Group = -> [C_element090,H_element082,O_element082]
  conduct = 2
  density = 1
  expand = 3
  formula = G4_POLYVINYL_ALCOHOL
  name = G4_POLYVINYL_ALCOHOL
  specific = 4
FEATURE [App::DocumentObjectGroupPython] C_element091  label="C_element : 049"  # scripted group (container) (typed FeaturePython)
  n = 8
  ref = C_element
FEATURE [App::DocumentObjectGroupPython] H_element083  label="H_element : 045"  # scripted group (container) (typed FeaturePython)
  n = 14
  ref = H_element
FEATURE [App::DocumentObjectGroupPython] O_element083  label="O_element : 044"  # scripted group (container) (typed FeaturePython)
  n = 2
  ref = O_element
FEATURE [App::DocumentObjectGroupPython] G4_POLYVINYL_BUTYRAL  # scripted group (container) (typed FeaturePython)
  Dunit = g/cm3
  Dvalue = 1.12
  Group = -> [C_element091,H_element083,O_element083]
  conduct = 2
  density = 1
  expand = 3
  formula = G4_POLYVINYL_BUTYRAL
  name = G4_POLYVINYL_BUTYRAL
  specific = 4
FEATURE [App::DocumentObjectGroupPython] C_element092  label="C_element : 050"  # scripted group (container) (typed FeaturePython)
  n = 2
  ref = C_element
FEATURE [App::DocumentObjectGroupPython] H_element084  label="H_element : 046"  # scripted group (container) (typed FeaturePython)
  n = 3
  ref = H_element
FEATURE [App::DocumentObjectGroupPython] Cl_element019  label="Cl_element : 009"  # scripted group (container) (typed FeaturePython)
  n = 1
  ref = Cl_element
FEATURE [App::DocumentObjectGroupPython] G4_POLYVINYL_CHLORIDE  # scripted group (container) (typed FeaturePython)
  Dunit = g/cm3
  Dvalue = 1.3
  Group = -> [C_element092,H_element084,Cl_element019]
  conduct = 2
  density = 1
  expand = 3
  formula = G4_POLYVINYL_CHLORIDE
  name = G4_POLYVINYL_CHLORIDE
  specific = 4
FEATURE [App::DocumentObjectGroupPython] C_element093  label="C_element : 051"  # scripted group (container) (typed FeaturePython)
  n = 2
  ref = C_element
FEATURE [App::DocumentObjectGroupPython] H_element085  label="H_element : 047"  # scripted group (container) (typed FeaturePython)
  n = 2
  ref = H_element
FEATURE [App::DocumentObjectGroupPython] Cl_element020  label="Cl_element : 010"  # scripted group (container) (typed FeaturePython)
  n = 2
  ref = Cl_element
FEATURE [App::DocumentObjectGroupPython] G4_POLYVINYLIDENE_CHLORIDE  # scripted group (container) (typed FeaturePython)
  Dunit = g/cm3
  Dvalue = 1.7
  Group = -> [C_element093,H_element085,Cl_element020]
  conduct = 2
  density = 1
  expand = 3
  formula = G4_POLYVINYLIDENE_CHLORIDE
  name = G4_POLYVINYLIDENE_CHLORIDE
  specific = 4
FEATURE [App::DocumentObjectGroupPython] C_element094  label="C_element : 052"  # scripted group (container) (typed FeaturePython)
  n = 2
  ref = C_element
FEATURE [App::DocumentObjectGroupPython] H_element086  label="H_element : 048"  # scripted group (container) (typed FeaturePython)
  n = 2
  ref = H_element
FEATURE [App::DocumentObjectGroupPython] F_element016  label="F_element : 007"  # scripted group (container) (typed FeaturePython)
  n = 2
  ref = F_element
FEATURE [App::DocumentObjectGroupPython] G4_POLYVINYLIDENE_FLUORIDE  # scripted group (container) (typed FeaturePython)
  Dunit = g/cm3
  Dvalue = 1.76
  Group = -> [C_element094,H_element086,F_element016]
  conduct = 2
  density = 1
  expand = 3
  formula = G4_POLYVINYLIDENE_FLUORIDE
  name = G4_POLYVINYLIDENE_FLUORIDE
  specific = 4
FEATURE [App::DocumentObjectGroupPython] C_element095  label="C_element : 053"  # scripted group (container) (typed FeaturePython)
  n = 6
  ref = C_element
FEATURE [App::DocumentObjectGroupPython] H_element087  label="H_element : 9"  # scripted group (container) (typed FeaturePython)
  n = 9
  ref = H_element
FEATURE [App::DocumentObjectGroupPython] N_element037  label="N_element : 016"  # scripted group (container) (typed FeaturePython)
  n = 1
  ref = N_element
FEATURE [App::DocumentObjectGroupPython] O_element084  label="O_element : 045"  # scripted group (container) (typed FeaturePython)
  n = 1
  ref = O_element
FEATURE [App::DocumentObjectGroupPython] G4_POLYVINYL_PYRROLIDONE  # scripted group (container) (typed FeaturePython)
  Dunit = g/cm3
  Dvalue = 1.25
  Group = -> [C_element095,H_element087,N_element037,O_element084]
  conduct = 2
  density = 1
  expand = 3
  formula = G4_POLYVINYL_PYRROLIDONE
  name = G4_POLYVINYL_PYRROLIDONE
  specific = 4
FEATURE [App::DocumentObjectGroupPython] K_element008  label="K_element : 1"  # scripted group (container) (typed FeaturePython)
  n = 1
  ref = K_element
FEATURE [App::DocumentObjectGroupPython] I_element006  label="I_element : 003"  # scripted group (container) (typed FeaturePython)
  n = 1
  ref = I_element
FEATURE [App::DocumentObjectGroupPython] G4_POTASSIUM_IODIDE  # scripted group (container) (typed FeaturePython)
  Dunit = g/cm3
  Dvalue = 3.13
  Group = -> [K_element008,I_element006]
  conduct = 2
  density = 1
  expand = 3
  formula = G4_POTASSIUM_IODIDE
  name = G4_POTASSIUM_IODIDE
  specific = 4
FEATURE [App::DocumentObjectGroupPython] K_element009  label="K_element : 2"  # scripted group (container) (typed FeaturePython)
  n = 2
  ref = K_element
FEATURE [App::DocumentObjectGroupPython] O_element085  label="O_element : 046"  # scripted group (container) (typed FeaturePython)
  n = 1
  ref = O_element
FEATURE [App::DocumentObjectGroupPython] G4_POTASSIUM_OXIDE  # scripted group (container) (typed FeaturePython)
  Dunit = g/cm3
  Dvalue = 2.32
  Group = -> [K_element009,O_element085]
  conduct = 2
  density = 1
  expand = 3
  formula = G4_POTASSIUM_OXIDE
  name = G4_POTASSIUM_OXIDE
  specific = 4
FEATURE [App::DocumentObjectGroupPython] C_element096  label="C_element : 054"  # scripted group (container) (typed FeaturePython)
  n = 3
  ref = C_element
FEATURE [App::DocumentObjectGroupPython] H_element088  label="H_element : 049"  # scripted group (container) (typed FeaturePython)
  n = 8
  ref = H_element
FEATURE [App::DocumentObjectGroupPython] G4_PROPANE  # scripted group (container) (typed FeaturePython)
  Dunit = g/cm3
  Dvalue = 0.00187939
  Group = -> [C_element096,H_element088]
  conduct = 2
  density = 1
  expand = 3
  formula = G4_PROPANE
  name = G4_PROPANE
  specific = 4
FEATURE [App::DocumentObjectGroupPython] C_element097  label="C_element : 055"  # scripted group (container) (typed FeaturePython)
  n = 3
  ref = C_element
FEATURE [App::DocumentObjectGroupPython] H_element089  label="H_element : 050"  # scripted group (container) (typed FeaturePython)
  n = 8
  ref = H_element
FEATURE [App::DocumentObjectGroupPython] G4_lPROPANE  # scripted group (container) (typed FeaturePython)
  Dunit = g/cm3
  Dvalue = 0.43
  Group = -> [C_element097,H_element089]
  conduct = 2
  density = 1
  expand = 3
  formula = G4_lPROPANE
  name = G4_lPROPANE
  specific = 4
FEATURE [App::DocumentObjectGroupPython] C_element098  label="C_element : 056"  # scripted group (container) (typed FeaturePython)
  n = 3
  ref = C_element
FEATURE [App::DocumentObjectGroupPython] H_element090  label="H_element : 051"  # scripted group (container) (typed FeaturePython)
  n = 8
  ref = H_element
FEATURE [App::DocumentObjectGroupPython] O_element086  label="O_element : 047"  # scripted group (container) (typed FeaturePython)
  n = 1
  ref = O_element
FEATURE [App::DocumentObjectGroupPython] G4_N_PROPYL_ALCOHOL  label="G4_N-PROPYL_ALCOHOL"  # scripted group (container) (typed FeaturePython)
  Dunit = g/cm3
  Dvalue = 0.8035
  Group = -> [C_element098,H_element090,O_element086]
  conduct = 2
  density = 1
  expand = 3
  formula = G4_N-PROPYL_ALCOHOL
  name = G4_N-PROPYL_ALCOHOL
  specific = 4
FEATURE [App::DocumentObjectGroupPython] C_element099  label="C_element : 057"  # scripted group (container) (typed FeaturePython)
  n = 5
  ref = C_element
FEATURE [App::DocumentObjectGroupPython] H_element091  label="H_element : 052"  # scripted group (container) (typed FeaturePython)
  n = 5
  ref = H_element
FEATURE [App::DocumentObjectGroupPython] N_element038  label="N_element : 017"  # scripted group (container) (typed FeaturePython)
  n = 1
  ref = N_element
FEATURE [App::DocumentObjectGroupPython] G4_PYRIDINE  # scripted group (container) (typed FeaturePython)
  Dunit = g/cm3
  Dvalue = 0.9819
  Group = -> [C_element099,H_element091,N_element038]
  conduct = 2
  density = 1
  expand = 3
  formula = G4_PYRIDINE
  name = G4_PYRIDINE
  specific = 4
FEATURE [App::DocumentObjectGroupPython] H_element092  label="H_element : 0.144"  # scripted group (container) (typed FeaturePython)
  n = 0.143711
FEATURE [App::DocumentObjectGroupPython] C_element100  label="C_element : 0.856"  # scripted group (container) (typed FeaturePython)
  n = 0.856289
FEATURE [App::DocumentObjectGroupPython] G4_RUBBER_BUTYL  # scripted group (container) (typed FeaturePython)
  Dunit = g/cm3
  Dvalue = 0.92
  Group = -> [H_element092,C_element100]
  conduct = 2
  density = 1
  expand = 3
  formula = G4_RUBBER_BUTYL
  name = G4_RUBBER_BUTYL
  specific = 4
FEATURE [App::DocumentObjectGroupPython] H_element093  label="H_element : 0.118"  # scripted group (container) (typed FeaturePython)
  n = 0.118371
FEATURE [App::DocumentObjectGroupPython] C_element101  label="C_element : 0.882"  # scripted group (container) (typed FeaturePython)
  n = 0.881629
FEATURE [App::DocumentObjectGroupPython] G4_RUBBER_NATURAL  # scripted group (container) (typed FeaturePython)
  Dunit = g/cm3
  Dvalue = 0.92
  Group = -> [H_element093,C_element101]
  conduct = 2
  density = 1
  expand = 3
  formula = G4_RUBBER_NATURAL
  name = G4_RUBBER_NATURAL
  specific = 4
FEATURE [App::DocumentObjectGroupPython] H_element094  label="H_element : 0.145"  # scripted group (container) (typed FeaturePython)
  n = 0.05692
FEATURE [App::DocumentObjectGroupPython] C_element102  label="C_element : 0.543"  # scripted group (container) (typed FeaturePython)
  n = 0.542646
FEATURE [App::DocumentObjectGroupPython] Cl_element021  label="Cl_element : 0.400"  # scripted group (container) (typed FeaturePython)
  n = 0.400434
FEATURE [App::DocumentObjectGroupPython] G4_RUBBER_NEOPRENE  # scripted group (container) (typed FeaturePython)
  Dunit = g/cm3
  Dvalue = 1.23
  Group = -> [H_element094,C_element102,Cl_element021]
  conduct = 2
  density = 1
  expand = 3
  formula = G4_RUBBER_NEOPRENE
  name = G4_RUBBER_NEOPRENE
  specific = 4
FEATURE [App::DocumentObjectGroupPython] Si_element006  label="Si_element : 1"  # scripted group (container) (typed FeaturePython)
  n = 1
  ref = Si_element
FEATURE [App::DocumentObjectGroupPython] O_element087  label="O_element : 048"  # scripted group (container) (typed FeaturePython)
  n = 2
  ref = O_element
FEATURE [App::DocumentObjectGroupPython] G4_SILICON_DIOXIDE  # scripted group (container) (typed FeaturePython)
  Dunit = g/cm3
  Dvalue = 2.32
  Group = -> [Si_element006,O_element087]
  conduct = 2
  density = 1
  expand = 3
  formula = G4_SILICON_DIOXIDE
  name = G4_SILICON_DIOXIDE
  specific = 4
FEATURE [App::DocumentObjectGroupPython] Ag_element002  label="Ag_element : 1"  # scripted group (container) (typed FeaturePython)
  n = 1
  ref = Ag_element
FEATURE [App::DocumentObjectGroupPython] Br_element005  label="Br_element : 003"  # scripted group (container) (typed FeaturePython)
  n = 1
  ref = Br_element
FEATURE [App::DocumentObjectGroupPython] G4_SILVER_BROMIDE  # scripted group (container) (typed FeaturePython)
  Dunit = g/cm3
  Dvalue = 6.473
  Group = -> [Ag_element002,Br_element005]
  conduct = 2
  density = 1
  expand = 3
  formula = G4_SILVER_BROMIDE
  name = G4_SILVER_BROMIDE
  specific = 4
FEATURE [App::DocumentObjectGroupPython] Ag_element003  label="Ag_element : 002"  # scripted group (container) (typed FeaturePython)
  n = 1
  ref = Ag_element
FEATURE [App::DocumentObjectGroupPython] Cl_element022  label="Cl_element : 011"  # scripted group (container) (typed FeaturePython)
  n = 1
  ref = Cl_element
FEATURE [App::DocumentObjectGroupPython] G4_SILVER_CHLORIDE  # scripted group (container) (typed FeaturePython)
  Dunit = g/cm3
  Dvalue = 5.56
  Group = -> [Ag_element003,Cl_element022]
  conduct = 2
  density = 1
  expand = 3
  formula = G4_SILVER_CHLORIDE
  name = G4_SILVER_CHLORIDE
  specific = 4
FEATURE [App::DocumentObjectGroupPython] Br_element006  label="Br_element : 0.423"  # scripted group (container) (typed FeaturePython)
  n = 0.422895
FEATURE [App::DocumentObjectGroupPython] Ag_element004  label="Ag_element : 0.574"  # scripted group (container) (typed FeaturePython)
  n = 0.573748
FEATURE [App::DocumentObjectGroupPython] I_element007  label="I_element : 0.649"  # scripted group (container) (typed FeaturePython)
  n = 0.003357
FEATURE [App::DocumentObjectGroupPython] G4_SILVER_HALIDES  # scripted group (container) (typed FeaturePython)
  Dunit = g/cm3
  Dvalue = 6.47
  Group = -> [Br_element006,Ag_element004,I_element007]
  conduct = 2
  density = 1
  expand = 3
  formula = G4_SILVER_HALIDES
  name = G4_SILVER_HALIDES
  specific = 4
FEATURE [App::DocumentObjectGroupPython] Ag_element005  label="Ag_element : 003"  # scripted group (container) (typed FeaturePython)
  n = 1
  ref = Ag_element
FEATURE [App::DocumentObjectGroupPython] I_element008  label="I_element : 004"  # scripted group (container) (typed FeaturePython)
  n = 1
  ref = I_element
FEATURE [App::DocumentObjectGroupPython] G4_SILVER_IODIDE  # scripted group (container) (typed FeaturePython)
  Dunit = g/cm3
  Dvalue = 6.01
  Group = -> [Ag_element005,I_element008]
  conduct = 2
  density = 1
  expand = 3
  formula = G4_SILVER_IODIDE
  name = G4_SILVER_IODIDE
  specific = 4
FEATURE [App::DocumentObjectGroupPython] H_element095  label="H_element : 0.100"  # scripted group (container) (typed FeaturePython)
  n = 0.1
FEATURE [App::DocumentObjectGroupPython] C_element103  label="C_element : 0.204"  # scripted group (container) (typed FeaturePython)
  n = 0.204
FEATURE [App::DocumentObjectGroupPython] N_element039  label="N_element : 0.759"  # scripted group (container) (typed FeaturePython)
  n = 0.042
FEATURE [App::DocumentObjectGroupPython] O_element088  label="O_element : 0.645"  # scripted group (container) (typed FeaturePython)
  n = 0.645
FEATURE [App::DocumentObjectGroupPython] Na_element013  label="Na_element : 0.100"  # scripted group (container) (typed FeaturePython)
  n = 0.002
FEATURE [App::DocumentObjectGroupPython] P_element009  label="P_element : 0.107"  # scripted group (container) (typed FeaturePython)
  n = 0.001
FEATURE [App::DocumentObjectGroupPython] S_element020  label="S_element : 0.021"  # scripted group (container) (typed FeaturePython)
  n = 0.002
FEATURE [App::DocumentObjectGroupPython] Cl_element023  label="Cl_element : 0.590"  # scripted group (container) (typed FeaturePython)
  n = 0.003
FEATURE [App::DocumentObjectGroupPython] K_element010  label="K_element : 0.001"  # scripted group (container) (typed FeaturePython)
  n = 0.001
FEATURE [App::DocumentObjectGroupPython] G4_SKIN_ICRP  # scripted group (container) (typed FeaturePython)
  Dunit = g/cm3
  Dvalue = 1.09
  Group = -> [H_element095,C_element103,N_element039,O_element088,Na_element013,P_element009,S_element020,Cl_element023,K_element010]
  conduct = 2
  density = 1
  expand = 3
  formula = G4_SKIN_ICRP
  name = G4_SKIN_ICRP
  specific = 4
FEATURE [App::DocumentObjectGroupPython] Na_element014  label="Na_element : 2"  # scripted group (container) (typed FeaturePython)
  n = 2
  ref = Na_element
FEATURE [App::DocumentObjectGroupPython] C_element104  label="C_element : 058"  # scripted group (container) (typed FeaturePython)
  n = 1
  ref = C_element
FEATURE [App::DocumentObjectGroupPython] O_element089  label="O_element : 049"  # scripted group (container) (typed FeaturePython)
  n = 3
  ref = O_element
FEATURE [App::DocumentObjectGroupPython] G4_SODIUM_CARBONATE  # scripted group (container) (typed FeaturePython)
  Dunit = g/cm3
  Dvalue = 2.532
  Group = -> [Na_element014,C_element104,O_element089]
  conduct = 2
  density = 1
  expand = 3
  formula = G4_SODIUM_CARBONATE
  name = G4_SODIUM_CARBONATE
  specific = 4
FEATURE [App::DocumentObjectGroupPython] Na_element015  label="Na_element : 1"  # scripted group (container) (typed FeaturePython)
  n = 1
  ref = Na_element
FEATURE [App::DocumentObjectGroupPython] I_element009  label="I_element : 005"  # scripted group (container) (typed FeaturePython)
  n = 1
  ref = I_element
FEATURE [App::DocumentObjectGroupPython] G4_SODIUM_IODIDE  # scripted group (container) (typed FeaturePython)
  Dunit = g/cm3
  Dvalue = 3.667
  Group = -> [Na_element015,I_element009]
  conduct = 2
  density = 1
  expand = 3
  formula = G4_SODIUM_IODIDE
  name = G4_SODIUM_IODIDE
  specific = 4
FEATURE [App::DocumentObjectGroupPython] Na_element016  label="Na_element : 003"  # scripted group (container) (typed FeaturePython)
  n = 2
  ref = Na_element
FEATURE [App::DocumentObjectGroupPython] O_element090  label="O_element : 050"  # scripted group (container) (typed FeaturePython)
  n = 1
  ref = O_element
FEATURE [App::DocumentObjectGroupPython] G4_SODIUM_MONOXIDE  # scripted group (container) (typed FeaturePython)
  Dunit = g/cm3
  Dvalue = 2.27
  Group = -> [Na_element016,O_element090]
  conduct = 2
  density = 1
  expand = 3
  formula = G4_SODIUM_MONOXIDE
  name = G4_SODIUM_MONOXIDE
  specific = 4
FEATURE [App::DocumentObjectGroupPython] Na_element017  label="Na_element : 004"  # scripted group (container) (typed FeaturePython)
  n = 1
  ref = Na_element
FEATURE [App::DocumentObjectGroupPython] N_element040  label="N_element : 018"  # scripted group (container) (typed FeaturePython)
  n = 1
  ref = N_element
FEATURE [App::DocumentObjectGroupPython] O_element091  label="O_element : 051"  # scripted group (container) (typed FeaturePython)
  n = 3
  ref = O_element
FEATURE [App::DocumentObjectGroupPython] G4_SODIUM_NITRATE  # scripted group (container) (typed FeaturePython)
  Dunit = g/cm3
  Dvalue = 2.261
  Group = -> [Na_element017,N_element040,O_element091]
  conduct = 2
  density = 1
  expand = 3
  formula = G4_SODIUM_NITRATE
  name = G4_SODIUM_NITRATE
  specific = 4
FEATURE [App::DocumentObjectGroupPython] C_element105  label="C_element : 059"  # scripted group (container) (typed FeaturePython)
  n = 14
  ref = C_element
FEATURE [App::DocumentObjectGroupPython] H_element096  label="H_element : 053"  # scripted group (container) (typed FeaturePython)
  n = 12
  ref = H_element
FEATURE [App::DocumentObjectGroupPython] G4_STILBENE  # scripted group (container) (typed FeaturePython)
  Dunit = g/cm3
  Dvalue = 0.9707
  Group = -> [C_element105,H_element096]
  conduct = 2
  density = 1
  expand = 3
  formula = G4_STILBENE
  name = G4_STILBENE
  specific = 4
FEATURE [App::DocumentObjectGroupPython] C_element106  label="C_element : 12"  # scripted group (container) (typed FeaturePython)
  n = 12
  ref = C_element
FEATURE [App::DocumentObjectGroupPython] H_element097  label="H_element : 22"  # scripted group (container) (typed FeaturePython)
  n = 22
  ref = H_element
FEATURE [App::DocumentObjectGroupPython] O_element092  label="O_element : 11"  # scripted group (container) (typed FeaturePython)
  n = 11
  ref = O_element
FEATURE [App::DocumentObjectGroupPython] G4_SUCROSE  # scripted group (container) (typed FeaturePython)
  Dunit = g/cm3
  Dvalue = 1.5805
  Group = -> [C_element106,H_element097,O_element092]
  conduct = 2
  density = 1
  expand = 3
  formula = G4_SUCROSE
  name = G4_SUCROSE
  specific = 4
FEATURE [App::DocumentObjectGroupPython] C_element107  label="C_element : 18"  # scripted group (container) (typed FeaturePython)
  n = 18
  ref = C_element
FEATURE [App::DocumentObjectGroupPython] H_element098  label="H_element : 054"  # scripted group (container) (typed FeaturePython)
  n = 14
  ref = H_element
FEATURE [App::DocumentObjectGroupPython] G4_TERPHENYL  # scripted group (container) (typed FeaturePython)
  Dunit = g/cm3
  Dvalue = 1.24
  Group = -> [C_element107,H_element098]
  conduct = 2
  density = 1
  expand = 3
  formula = G4_TERPHENYL
  name = G4_TERPHENYL
  specific = 4
FEATURE [App::DocumentObjectGroupPython] H_element099  label="H_element : 0.146"  # scripted group (container) (typed FeaturePython)
  n = 0.106
FEATURE [App::DocumentObjectGroupPython] C_element108  label="C_element : 0.883"  # scripted group (container) (typed FeaturePython)
  n = 0.099
FEATURE [App::DocumentObjectGroupPython] N_element041  label="N_element : 0.020"  # scripted group (container) (typed FeaturePython)
  n = 0.02
FEATURE [App::DocumentObjectGroupPython] O_element093  label="O_element : 0.766"  # scripted group (container) (typed FeaturePython)
  n = 0.766
FEATURE [App::DocumentObjectGroupPython] Na_element018  label="Na_element : 0.101"  # scripted group (container) (typed FeaturePython)
  n = 0.002
FEATURE [App::DocumentObjectGroupPython] P_element010  label="P_element : 0.108"  # scripted group (container) (typed FeaturePython)
  n = 0.001
FEATURE [App::DocumentObjectGroupPython] S_element021  label="S_element : 0.022"  # scripted group (container) (typed FeaturePython)
  n = 0.002
FEATURE [App::DocumentObjectGroupPython] Cl_element024  label="Cl_element : 0.002"  # scripted group (container) (typed FeaturePython)
  n = 0.002
FEATURE [App::DocumentObjectGroupPython] K_element011  label="K_element : 0.017"  # scripted group (container) (typed FeaturePython)
  n = 0.002
FEATURE [App::DocumentObjectGroupPython] G4_TESTIS_ICRP  # scripted group (container) (typed FeaturePython)
  Dunit = g/cm3
  Dvalue = 1.04
  Group = -> [H_element099,C_element108,N_element041,O_element093,Na_element018,P_element010,S_element021,Cl_element024,K_element011]
  conduct = 2
  density = 1
  expand = 3
  formula = G4_TESTIS_ICRP
  name = G4_TESTIS_ICRP
  specific = 4
FEATURE [App::DocumentObjectGroupPython] C_element109  label="C_element : 060"  # scripted group (container) (typed FeaturePython)
  n = 2
  ref = C_element
FEATURE [App::DocumentObjectGroupPython] Cl_element025  label="Cl_element : 012"  # scripted group (container) (typed FeaturePython)
  n = 4
  ref = Cl_element
FEATURE [App::DocumentObjectGroupPython] G4_TETRACHLOROETHYLENE  # scripted group (container) (typed FeaturePython)
  Dunit = g/cm3
  Dvalue = 1.625
  Group = -> [C_element109,Cl_element025]
  conduct = 2
  density = 1
  expand = 3
  formula = G4_TETRACHLOROETHYLENE
  name = G4_TETRACHLOROETHYLENE
  specific = 4
FEATURE [App::DocumentObjectGroupPython] Tl_element001  label="Tl_element : 1"  # scripted group (container) (typed FeaturePython)
  n = 1
  ref = Tl_element
FEATURE [App::DocumentObjectGroupPython] Cl_element026  label="Cl_element : 013"  # scripted group (container) (typed FeaturePython)
  n = 1
  ref = Cl_element
FEATURE [App::DocumentObjectGroupPython] G4_THALLIUM_CHLORIDE  # scripted group (container) (typed FeaturePython)
  Dunit = g/cm3
  Dvalue = 7.004
  Group = -> [Tl_element001,Cl_element026]
  conduct = 2
  density = 1
  expand = 3
  formula = G4_THALLIUM_CHLORIDE
  name = G4_THALLIUM_CHLORIDE
  specific = 4
FEATURE [App::DocumentObjectGroupPython] H_element100  label="H_element : 0.147"  # scripted group (container) (typed FeaturePython)
  n = 0.105
FEATURE [App::DocumentObjectGroupPython] C_element110  label="C_element : 0.256"  # scripted group (container) (typed FeaturePython)
  n = 0.256
FEATURE [App::DocumentObjectGroupPython] N_element042  label="N_element : 0.760"  # scripted group (container) (typed FeaturePython)
  n = 0.027
FEATURE [App::DocumentObjectGroupPython] O_element094  label="O_element : 0.602"  # scripted group (container) (typed FeaturePython)
  n = 0.602
FEATURE [App::DocumentObjectGroupPython] Na_element019  label="Na_element : 0.102"  # scripted group (container) (typed FeaturePython)
  n = 0.001
FEATURE [App::DocumentObjectGroupPython] P_element011  label="P_element : 0.109"  # scripted group (container) (typed FeaturePython)
  n = 0.002
FEATURE [App::DocumentObjectGroupPython] S_element022  label="S_element : 0.023"  # scripted group (container) (typed FeaturePython)
  n = 0.003
FEATURE [App::DocumentObjectGroupPython] Cl_element027  label="Cl_element : 0.591"  # scripted group (container) (typed FeaturePython)
  n = 0.002
FEATURE [App::DocumentObjectGroupPython] K_element012  label="K_element : 0.018"  # scripted group (container) (typed FeaturePython)
  n = 0.002
FEATURE [App::DocumentObjectGroupPython] G4_TISSUE_SOFT_ICRP  # scripted group (container) (typed FeaturePython)
  Dunit = g/cm3
  Dvalue = 1.03
  Group = -> [H_element100,C_element110,N_element042,O_element094,Na_element019,P_element011,S_element022,Cl_element027,K_element012]
  conduct = 2
  density = 1
  expand = 3
  formula = G4_TISSUE_SOFT_ICRP
  name = G4_TISSUE_SOFT_ICRP
  specific = 4
FEATURE [App::DocumentObjectGroupPython] H_element101  label="H_element : 0.148"  # scripted group (container) (typed FeaturePython)
  n = 0.101
FEATURE [App::DocumentObjectGroupPython] C_element111  label="C_element : 0.111"  # scripted group (container) (typed FeaturePython)
  n = 0.111
FEATURE [App::DocumentObjectGroupPython] N_element043  label="N_element : 0.026"  # scripted group (container) (typed FeaturePython)
  n = 0.026
FEATURE [App::DocumentObjectGroupPython] O_element095  label="O_element : 0.762"  # scripted group (container) (typed FeaturePython)
  n = 0.762
FEATURE [App::DocumentObjectGroupPython] G4_TISSUE_SOFT_ICRU_4  label="G4_TISSUE_SOFT_ICRU-4"  # scripted group (container) (typed FeaturePython)
  Dunit = g/cm3
  Dvalue = 1
  Group = -> [H_element101,C_element111,N_element043,O_element095]
  conduct = 2
  density = 1
  expand = 3
  formula = G4_TISSUE_SOFT_ICRU-4
  name = G4_TISSUE_SOFT_ICRU-4
  specific = 4
FEATURE [App::DocumentObjectGroupPython] H_element102  label="H_element : 0.149"  # scripted group (container) (typed FeaturePython)
  n = 0.101869
FEATURE [App::DocumentObjectGroupPython] C_element112  label="C_element : 0.456"  # scripted group (container) (typed FeaturePython)
  n = 0.456179
FEATURE [App::DocumentObjectGroupPython] N_element044  label="N_element : 0.761"  # scripted group (container) (typed FeaturePython)
  n = 0.035172
FEATURE [App::DocumentObjectGroupPython] O_element096  label="O_element : 0.407"  # scripted group (container) (typed FeaturePython)
  n = 0.40678
FEATURE [App::DocumentObjectGroupPython] G4_TISSUE_METHANE  label="G4_TISSUE-METHANE"  # scripted group (container) (typed FeaturePython)
  Dunit = g/cm3
  Dvalue = 0.00106409
  Group = -> [H_element102,C_element112,N_element044,O_element096]
  conduct = 2
  density = 1
  expand = 3
  formula = G4_TISSUE-METHANE
  name = G4_TISSUE-METHANE
  specific = 4
FEATURE [App::DocumentObjectGroupPython] H_element103  label="H_element : 0.103"  # scripted group (container) (typed FeaturePython)
  n = 0.102672
FEATURE [App::DocumentObjectGroupPython] C_element113  label="C_element : 0.569"  # scripted group (container) (typed FeaturePython)
  n = 0.56894
FEATURE [App::DocumentObjectGroupPython] N_element045  label="N_element : 0.762"  # scripted group (container) (typed FeaturePython)
  n = 0.035022
FEATURE [App::DocumentObjectGroupPython] O_element097  label="O_element : 0.293"  # scripted group (container) (typed FeaturePython)
  n = 0.293366
FEATURE [App::DocumentObjectGroupPython] G4_TISSUE_PROPANE  label="G4_TISSUE-PROPANE"  # scripted group (container) (typed FeaturePython)
  Dunit = g/cm3
  Dvalue = 0.00182628
  Group = -> [H_element103,C_element113,N_element045,O_element097]
  conduct = 2
  density = 1
  expand = 3
  formula = G4_TISSUE-PROPANE
  name = G4_TISSUE-PROPANE
  specific = 4
FEATURE [App::DocumentObjectGroupPython] Ti_element003  label="Ti_element : 1"  # scripted group (container) (typed FeaturePython)
  n = 1
  ref = Ti_element
FEATURE [App::DocumentObjectGroupPython] O_element098  label="O_element : 052"  # scripted group (container) (typed FeaturePython)
  n = 2
  ref = O_element
FEATURE [App::DocumentObjectGroupPython] G4_TITANIUM_DIOXIDE  # scripted group (container) (typed FeaturePython)
  Dunit = g/cm3
  Dvalue = 4.26
  Group = -> [Ti_element003,O_element098]
  conduct = 2
  density = 1
  expand = 3
  formula = G4_TITANIUM_DIOXIDE
  name = G4_TITANIUM_DIOXIDE
  specific = 4
FEATURE [App::DocumentObjectGroupPython] C_element114  label="C_element : 061"  # scripted group (container) (typed FeaturePython)
  n = 7
  ref = C_element
FEATURE [App::DocumentObjectGroupPython] H_element104  label="H_element : 055"  # scripted group (container) (typed FeaturePython)
  n = 8
  ref = H_element
FEATURE [App::DocumentObjectGroupPython] G4_TOLUENE  # scripted group (container) (typed FeaturePython)
  Dunit = g/cm3
  Dvalue = 0.8669
  Group = -> [C_element114,H_element104]
  conduct = 2
  density = 1
  expand = 3
  formula = G4_TOLUENE
  name = G4_TOLUENE
  specific = 4
FEATURE [App::DocumentObjectGroupPython] C_element115  label="C_element : 062"  # scripted group (container) (typed FeaturePython)
  n = 2
  ref = C_element
FEATURE [App::DocumentObjectGroupPython] H_element105  label="H_element : 056"  # scripted group (container) (typed FeaturePython)
  n = 1
  ref = H_element
FEATURE [App::DocumentObjectGroupPython] Cl_element028  label="Cl_element : 014"  # scripted group (container) (typed FeaturePython)
  n = 3
  ref = Cl_element
FEATURE [App::DocumentObjectGroupPython] G4_TRICHLOROETHYLENE  # scripted group (container) (typed FeaturePython)
  Dunit = g/cm3
  Dvalue = 1.46
  Group = -> [C_element115,H_element105,Cl_element028]
  conduct = 2
  density = 1
  expand = 3
  formula = G4_TRICHLOROETHYLENE
  name = G4_TRICHLOROETHYLENE
  specific = 4
FEATURE [App::DocumentObjectGroupPython] C_element116  label="C_element : 063"  # scripted group (container) (typed FeaturePython)
  n = 6
  ref = C_element
FEATURE [App::DocumentObjectGroupPython] H_element106  label="H_element : 15"  # scripted group (container) (typed FeaturePython)
  n = 15
  ref = H_element
FEATURE [App::DocumentObjectGroupPython] O_element099  label="O_element : 053"  # scripted group (container) (typed FeaturePython)
  n = 4
  ref = O_element
FEATURE [App::DocumentObjectGroupPython] P_element012  label="P_element : 1"  # scripted group (container) (typed FeaturePython)
  n = 1
  ref = P_element
FEATURE [App::DocumentObjectGroupPython] G4_TRIETHYL_PHOSPHATE  # scripted group (container) (typed FeaturePython)
  Dunit = g/cm3
  Dvalue = 1.07
  Group = -> [C_element116,H_element106,O_element099,P_element012]
  conduct = 2
  density = 1
  expand = 3
  formula = G4_TRIETHYL_PHOSPHATE
  name = G4_TRIETHYL_PHOSPHATE
  specific = 4
FEATURE [App::DocumentObjectGroupPython] W_element003  label="W_element : 003"  # scripted group (container) (typed FeaturePython)
  n = 1
  ref = W_element
FEATURE [App::DocumentObjectGroupPython] F_element017  label="F_element : 6"  # scripted group (container) (typed FeaturePython)
  n = 6
  ref = F_element
FEATURE [App::DocumentObjectGroupPython] G4_TUNGSTEN_HEXAFLUORIDE  # scripted group (container) (typed FeaturePython)
  Dunit = g/cm3
  Dvalue = 2.4
  Group = -> [W_element003,F_element017]
  conduct = 2
  density = 1
  expand = 3
  formula = G4_TUNGSTEN_HEXAFLUORIDE
  name = G4_TUNGSTEN_HEXAFLUORIDE
  specific = 4
FEATURE [App::DocumentObjectGroupPython] U_element001  label="U_element : 1"  # scripted group (container) (typed FeaturePython)
  n = 1
  ref = U_element
FEATURE [App::DocumentObjectGroupPython] C_element117  label="C_element : 064"  # scripted group (container) (typed FeaturePython)
  n = 2
  ref = C_element
FEATURE [App::DocumentObjectGroupPython] G4_URANIUM_DICARBIDE  # scripted group (container) (typed FeaturePython)
  Dunit = g/cm3
  Dvalue = 11.28
  Group = -> [U_element001,C_element117]
  conduct = 2
  density = 1
  expand = 3
  formula = G4_URANIUM_DICARBIDE
  name = G4_URANIUM_DICARBIDE
  specific = 4
FEATURE [App::DocumentObjectGroupPython] U_element002  label="U_element : 002"  # scripted group (container) (typed FeaturePython)
  n = 1
  ref = U_element
FEATURE [App::DocumentObjectGroupPython] C_element118  label="C_element : 065"  # scripted group (container) (typed FeaturePython)
  n = 1
  ref = C_element
FEATURE [App::DocumentObjectGroupPython] G4_URANIUM_MONOCARBIDE  # scripted group (container) (typed FeaturePython)
  Dunit = g/cm3
  Dvalue = 13.63
  Group = -> [U_element002,C_element118]
  conduct = 2
  density = 1
  expand = 3
  formula = G4_URANIUM_MONOCARBIDE
  name = G4_URANIUM_MONOCARBIDE
  specific = 4
FEATURE [App::DocumentObjectGroupPython] U_element003  label="U_element : 003"  # scripted group (container) (typed FeaturePython)
  n = 1
  ref = U_element
FEATURE [App::DocumentObjectGroupPython] O_element100  label="O_element : 054"  # scripted group (container) (typed FeaturePython)
  n = 2
  ref = O_element
FEATURE [App::DocumentObjectGroupPython] G4_URANIUM_OXIDE  # scripted group (container) (typed FeaturePython)
  Dunit = g/cm3
  Dvalue = 10.96
  Group = -> [U_element003,O_element100]
  conduct = 2
  density = 1
  expand = 3
  formula = G4_URANIUM_OXIDE
  name = G4_URANIUM_OXIDE
  specific = 4
FEATURE [App::DocumentObjectGroupPython] C_element119  label="C_element : 066"  # scripted group (container) (typed FeaturePython)
  n = 1
  ref = C_element
FEATURE [App::DocumentObjectGroupPython] H_element107  label="H_element : 057"  # scripted group (container) (typed FeaturePython)
  n = 4
  ref = H_element
FEATURE [App::DocumentObjectGroupPython] N_element046  label="N_element : 019"  # scripted group (container) (typed FeaturePython)
  n = 2
  ref = N_element
FEATURE [App::DocumentObjectGroupPython] O_element101  label="O_element : 055"  # scripted group (container) (typed FeaturePython)
  n = 1
  ref = O_element
FEATURE [App::DocumentObjectGroupPython] G4_UREA  # scripted group (container) (typed FeaturePython)
  Dunit = g/cm3
  Dvalue = 1.323
  Group = -> [C_element119,H_element107,N_element046,O_element101]
  conduct = 2
  density = 1
  expand = 3
  formula = G4_UREA
  name = G4_UREA
  specific = 4
FEATURE [App::DocumentObjectGroupPython] C_element120  label="C_element : 067"  # scripted group (container) (typed FeaturePython)
  n = 5
  ref = C_element
FEATURE [App::DocumentObjectGroupPython] H_element108  label="H_element : 058"  # scripted group (container) (typed FeaturePython)
  n = 11
  ref = H_element
FEATURE [App::DocumentObjectGroupPython] N_element047  label="N_element : 020"  # scripted group (container) (typed FeaturePython)
  n = 1
  ref = N_element
FEATURE [App::DocumentObjectGroupPython] O_element102  label="O_element : 056"  # scripted group (container) (typed FeaturePython)
  n = 2
  ref = O_element
FEATURE [App::DocumentObjectGroupPython] G4_VALINE  # scripted group (container) (typed FeaturePython)
  Dunit = g/cm3
  Dvalue = 1.23
  Group = -> [C_element120,H_element108,N_element047,O_element102]
  conduct = 2
  density = 1
  expand = 3
  formula = G4_VALINE
  name = G4_VALINE
  specific = 4
FEATURE [App::DocumentObjectGroupPython] H_element109  label="H_element : 0.009"  # scripted group (container) (typed FeaturePython)
  n = 0.009417
FEATURE [App::DocumentObjectGroupPython] C_element121  label="C_element : 0.281"  # scripted group (container) (typed FeaturePython)
  n = 0.280555
FEATURE [App::DocumentObjectGroupPython] F_element018  label="F_element : 0.710"  # scripted group (container) (typed FeaturePython)
  n = 0.710028
FEATURE [App::DocumentObjectGroupPython] G4_VITON  # scripted group (container) (typed FeaturePython)
  Dunit = g/cm3
  Dvalue = 1.8
  Group = -> [H_element109,C_element121,F_element018]
  conduct = 2
  density = 1
  expand = 3
  formula = G4_VITON
  name = G4_VITON
  specific = 4
FEATURE [App::DocumentObjectGroupPython] H_element110  label="H_element : 059"  # scripted group (container) (typed FeaturePython)
  n = 2
  ref = H_element
FEATURE [App::DocumentObjectGroupPython] O_element103  label="O_element : 057"  # scripted group (container) (typed FeaturePython)
  n = 1
  ref = O_element
FEATURE [App::DocumentObjectGroupPython] G4_WATER  # scripted group (container) (typed FeaturePython)
  Dunit = g/cm3
  Dvalue = 1
  Group = -> [H_element110,O_element103]
  conduct = 2
  density = 1
  expand = 3
  formula = G4_WATER
  name = G4_WATER
  specific = 4
FEATURE [App::DocumentObjectGroupPython] H_element111  label="H_element : 060"  # scripted group (container) (typed FeaturePython)
  n = 2
  ref = H_element
FEATURE [App::DocumentObjectGroupPython] O_element104  label="O_element : 058"  # scripted group (container) (typed FeaturePython)
  n = 1
  ref = O_element
FEATURE [App::DocumentObjectGroupPython] G4_WATER_VAPOR  # scripted group (container) (typed FeaturePython)
  Dunit = g/cm3
  Dvalue = 0.000756182
  Group = -> [H_element111,O_element104]
  conduct = 2
  density = 1
  expand = 3
  formula = G4_WATER_VAPOR
  name = G4_WATER_VAPOR
  specific = 4
FEATURE [App::DocumentObjectGroupPython] C_element122  label="C_element : 068"  # scripted group (container) (typed FeaturePython)
  n = 8
  ref = C_element
FEATURE [App::DocumentObjectGroupPython] H_element112  label="H_element : 061"  # scripted group (container) (typed FeaturePython)
  n = 10
  ref = H_element
FEATURE [App::DocumentObjectGroupPython] G4_XYLENE  # scripted group (container) (typed FeaturePython)
  Dunit = g/cm3
  Dvalue = 0.87
  Group = -> [C_element122,H_element112]
  conduct = 2
  density = 1
  expand = 3
  formula = G4_XYLENE
  name = G4_XYLENE
  specific = 4
FEATURE [App::DocumentObjectGroupPython] C_element123  label="C_element : 069"  # scripted group (container) (typed FeaturePython)
  n = 1
  ref = C_element
FEATURE [App::DocumentObjectGroupPython] G4_GRAPHITE  # scripted group (container) (typed FeaturePython)
  Dunit = g/cm3
  Dvalue = 2.21
  Group = -> [C_element123]
  conduct = 2
  density = 1
  expand = 3
  formula = G4_GRAPHITE
  name = G4_GRAPHITE
  specific = 4
FEATURE [App::DocumentObjectGroupPython] NIST  # scripted group (container) (typed FeaturePython)
  Group = -> [G4_A_150_TISSUE,G4_ACETONE,G4_ACETYLENE,G4_ADENINE,G4_ADIPOSE_TISSUE_ICRP,G4_AIR,G4_ALANINE,G4_ALUMINUM_OXIDE,G4_AMBER,G4_AMMONIA,G4_ANILINE,G4_ANTHRACENE,G4_B_100_BONE,G4_BAKELITE,G4_BARIUM_FLUORIDE,G4_BARIUM_SULFATE,G4_BENZENE,G4_BERYLLIUM_OXIDE,G4_BGO,G4_BLOOD_ICRP,G4_BONE_COMPACT_ICRU,G4_BONE_CORTICAL_ICRP,G4_BORON_CARBIDE,G4_BORON_OXIDE,G4_BRAIN_ICRP,G4_BUTANE,G4_N_BUTYL_ALCOHOL,G4_C_552,+152 more]
FEATURE [App::DocumentObjectGroupPython] H_element113  label="H_element : 062"  # scripted group (container) (typed FeaturePython)
  n = 1
  ref = H_element
FEATURE [App::DocumentObjectGroupPython] G4_H  # scripted group (container) (typed FeaturePython)
  Dunit = g/cm3
  Dvalue = 8.3748e-05
  Group = -> [H_element113]
  conduct = 2
  density = 1
  expand = 3
  formula = H
  name = G4_H
  specific = 4
FEATURE [App::DocumentObjectGroupPython] He_element001  label="He_element : 1"  # scripted group (container) (typed FeaturePython)
  n = 1
  ref = He_element
FEATURE [App::DocumentObjectGroupPython] G4_He  # scripted group (container) (typed FeaturePython)
  Dunit = g/cm3
  Dvalue = 0.000166322
  Group = -> [He_element001]
  conduct = 2
  density = 1
  expand = 3
  formula = He
  name = G4_He
  specific = 4
FEATURE [App::DocumentObjectGroupPython] Li_element008  label="Li_element : 008"  # scripted group (container) (typed FeaturePython)
  n = 1
  ref = Li_element
FEATURE [App::DocumentObjectGroupPython] G4_Li  # scripted group (container) (typed FeaturePython)
  Dunit = g/cm3
  Dvalue = 0.534
  Group = -> [Li_element008]
  conduct = 2
  density = 1
  expand = 3
  formula = Li
  name = G4_Li
  specific = 4
FEATURE [App::DocumentObjectGroupPython] Be_element002  label="Be_element : 002"  # scripted group (container) (typed FeaturePython)
  n = 1
  ref = Be_element
FEATURE [App::DocumentObjectGroupPython] G4_Be  # scripted group (container) (typed FeaturePython)
  Dunit = g/cm3
  Dvalue = 1.848
  Group = -> [Be_element002]
  conduct = 2
  density = 1
  expand = 3
  formula = Be
  name = G4_Be
  specific = 4
FEATURE [App::DocumentObjectGroupPython] B_element007  label="B_element : 007"  # scripted group (container) (typed FeaturePython)
  n = 1
  ref = B_element
FEATURE [App::DocumentObjectGroupPython] G4_B  # scripted group (container) (typed FeaturePython)
  Dunit = g/cm3
  Dvalue = 2.37
  Group = -> [B_element007]
  conduct = 2
  density = 1
  expand = 3
  formula = B
  name = G4_B
  specific = 4
FEATURE [App::DocumentObjectGroupPython] C_element124  label="C_element : 070"  # scripted group (container) (typed FeaturePython)
  n = 1
  ref = C_element
FEATURE [App::DocumentObjectGroupPython] G4_C  # scripted group (container) (typed FeaturePython)
  Dunit = g/cm3
  Dvalue = 2
  Group = -> [C_element124]
  conduct = 2
  density = 1
  expand = 3
  formula = C
  name = G4_C
  specific = 4
FEATURE [App::DocumentObjectGroupPython] N_element048  label="N_element : 021"  # scripted group (container) (typed FeaturePython)
  n = 1
  ref = N_element
FEATURE [App::DocumentObjectGroupPython] G4_N  # scripted group (container) (typed FeaturePython)
  Dunit = g/cm3
  Dvalue = 0.0011652
  Group = -> [N_element048]
  conduct = 2
  density = 1
  expand = 3
  formula = N
  name = G4_N
  specific = 4
FEATURE [App::DocumentObjectGroupPython] O_element105  label="O_element : 059"  # scripted group (container) (typed FeaturePython)
  n = 1
  ref = O_element
FEATURE [App::DocumentObjectGroupPython] G4_O  # scripted group (container) (typed FeaturePython)
  Dunit = g/cm3
  Dvalue = 0.00133151
  Group = -> [O_element105]
  conduct = 2
  density = 1
  expand = 3
  formula = O
  name = G4_O
  specific = 4
FEATURE [App::DocumentObjectGroupPython] F_element019  label="F_element : 008"  # scripted group (container) (typed FeaturePython)
  n = 1
  ref = F_element
FEATURE [App::DocumentObjectGroupPython] G4_F  # scripted group (container) (typed FeaturePython)
  Dunit = g/cm3
  Dvalue = 0.00158029
  Group = -> [F_element019]
  conduct = 2
  density = 1
  expand = 3
  formula = F
  name = G4_F
  specific = 4
FEATURE [App::DocumentObjectGroupPython] Ne_element001  label="Ne_element : 1"  # scripted group (container) (typed FeaturePython)
  n = 1
  ref = Ne_element
FEATURE [App::DocumentObjectGroupPython] G4_Ne  # scripted group (container) (typed FeaturePython)
  Dunit = g/cm3
  Dvalue = 0.000838505
  Group = -> [Ne_element001]
  conduct = 2
  density = 1
  expand = 3
  formula = Ne
  name = G4_Ne
  specific = 4
FEATURE [App::DocumentObjectGroupPython] Na_element020  label="Na_element : 005"  # scripted group (container) (typed FeaturePython)
  n = 1
  ref = Na_element
FEATURE [App::DocumentObjectGroupPython] G4_Na  # scripted group (container) (typed FeaturePython)
  Dunit = g/cm3
  Dvalue = 0.971
  Group = -> [Na_element020]
  conduct = 2
  density = 1
  expand = 3
  formula = Na
  name = G4_Na
  specific = 4
FEATURE [App::DocumentObjectGroupPython] Mg_element011  label="Mg_element : 005"  # scripted group (container) (typed FeaturePython)
  n = 1
  ref = Mg_element
FEATURE [App::DocumentObjectGroupPython] G4_Mg  # scripted group (container) (typed FeaturePython)
  Dunit = g/cm3
  Dvalue = 1.74
  Group = -> [Mg_element011]
  conduct = 2
  density = 1
  expand = 3
  formula = Mg
  name = G4_Mg
  specific = 4
FEATURE [App::DocumentObjectGroupPython] Al_element004  label="Al_element : 1"  # scripted group (container) (typed FeaturePython)
  n = 1
  ref = Al_element
FEATURE [App::DocumentObjectGroupPython] G4_Al  # scripted group (container) (typed FeaturePython)
  Dunit = g/cm3
  Dvalue = 2.699
  Group = -> [Al_element004]
  conduct = 2
  density = 1
  expand = 3
  formula = Al
  name = G4_Al
  specific = 4
FEATURE [App::DocumentObjectGroupPython] Si_element007  label="Si_element : 002"  # scripted group (container) (typed FeaturePython)
  n = 1
  ref = Si_element
FEATURE [App::DocumentObjectGroupPython] G4_Si  # scripted group (container) (typed FeaturePython)
  Dunit = g/cm3
  Dvalue = 2.33
  Group = -> [Si_element007]
  conduct = 2
  density = 1
  expand = 3
  formula = Si
  name = G4_Si
  specific = 4
FEATURE [App::DocumentObjectGroupPython] P_element013  label="P_element : 002"  # scripted group (container) (typed FeaturePython)
  n = 1
  ref = P_element
FEATURE [App::DocumentObjectGroupPython] G4_P  # scripted group (container) (typed FeaturePython)
  Dunit = g/cm3
  Dvalue = 2.2
  Group = -> [P_element013]
  conduct = 2
  density = 1
  expand = 3
  formula = P
  name = G4_P
  specific = 4
FEATURE [App::DocumentObjectGroupPython] S_element023  label="S_element : 007"  # scripted group (container) (typed FeaturePython)
  n = 1
  ref = S_element
FEATURE [App::DocumentObjectGroupPython] G4_S  # scripted group (container) (typed FeaturePython)
  Dunit = g/cm3
  Dvalue = 2
  Group = -> [S_element023]
  conduct = 2
  density = 1
  expand = 3
  formula = S
  name = G4_S
  specific = 4
FEATURE [App::DocumentObjectGroupPython] Cl_element029  label="Cl_element : 015"  # scripted group (container) (typed FeaturePython)
  n = 1
  ref = Cl_element
FEATURE [App::DocumentObjectGroupPython] G4_Cl  # scripted group (container) (typed FeaturePython)
  Dunit = g/cm3
  Dvalue = 0.00299473
  Group = -> [Cl_element029]
  conduct = 2
  density = 1
  expand = 3
  formula = Cl
  name = G4_Cl
  specific = 4
FEATURE [App::DocumentObjectGroupPython] Ar_element002  label="Ar_element : 1"  # scripted group (container) (typed FeaturePython)
  n = 1
  ref = Ar_element
FEATURE [App::DocumentObjectGroupPython] G4_Ar  # scripted group (container) (typed FeaturePython)
  Dunit = g/cm3
  Dvalue = 0.00166201
  Group = -> [Ar_element002]
  conduct = 2
  density = 1
  expand = 3
  formula = Ar
  name = G4_Ar
  specific = 4
FEATURE [App::DocumentObjectGroupPython] K_element013  label="K_element : 003"  # scripted group (container) (typed FeaturePython)
  n = 1
  ref = K_element
FEATURE [App::DocumentObjectGroupPython] G4_K  # scripted group (container) (typed FeaturePython)
  Dunit = g/cm3
  Dvalue = 0.862
  Group = -> [K_element013]
  conduct = 2
  density = 1
  expand = 3
  formula = K
  name = G4_K
  specific = 4
FEATURE [App::DocumentObjectGroupPython] Ca_element014  label="Ca_element : 007"  # scripted group (container) (typed FeaturePython)
  n = 1
  ref = Ca_element
FEATURE [App::DocumentObjectGroupPython] G4_Ca  # scripted group (container) (typed FeaturePython)
  Dunit = g/cm3
  Dvalue = 1.55
  Group = -> [Ca_element014]
  conduct = 2
  density = 1
  expand = 3
  formula = Ca
  name = G4_Ca
  specific = 4
FEATURE [App::DocumentObjectGroupPython] Sc_element001  label="Sc_element : 1"  # scripted group (container) (typed FeaturePython)
  n = 1
  ref = Sc_element
FEATURE [App::DocumentObjectGroupPython] G4_Sc  # scripted group (container) (typed FeaturePython)
  Dunit = g/cm3
  Dvalue = 2.989
  Group = -> [Sc_element001]
  conduct = 2
  density = 1
  expand = 3
  formula = Sc
  name = G4_Sc
  specific = 4
FEATURE [App::DocumentObjectGroupPython] Ti_element004  label="Ti_element : 002"  # scripted group (container) (typed FeaturePython)
  n = 1
  ref = Ti_element
FEATURE [App::DocumentObjectGroupPython] G4_Ti  # scripted group (container) (typed FeaturePython)
  Dunit = g/cm3
  Dvalue = 4.54
  Group = -> [Ti_element004]
  conduct = 2
  density = 1
  expand = 3
  formula = Ti
  name = G4_Ti
  specific = 4
FEATURE [App::DocumentObjectGroupPython] V_element001  label="V_element : 1"  # scripted group (container) (typed FeaturePython)
  n = 1
  ref = V_element
FEATURE [App::DocumentObjectGroupPython] G4_V  # scripted group (container) (typed FeaturePython)
  Dunit = g/cm3
  Dvalue = 6.11
  Group = -> [V_element001]
  conduct = 2
  density = 1
  expand = 3
  formula = V
  name = G4_V
  specific = 4
FEATURE [App::DocumentObjectGroupPython] Cr_element001  label="Cr_element : 1"  # scripted group (container) (typed FeaturePython)
  n = 1
  ref = Cr_element
FEATURE [App::DocumentObjectGroupPython] G4_Cr  # scripted group (container) (typed FeaturePython)
  Dunit = g/cm3
  Dvalue = 7.18
  Group = -> [Cr_element001]
  conduct = 2
  density = 1
  expand = 3
  formula = Cr
  name = G4_Cr
  specific = 4
FEATURE [App::DocumentObjectGroupPython] Mn_element001  label="Mn_element : 1"  # scripted group (container) (typed FeaturePython)
  n = 1
  ref = Mn_element
FEATURE [App::DocumentObjectGroupPython] G4_Mn  # scripted group (container) (typed FeaturePython)
  Dunit = g/cm3
  Dvalue = 7.44
  Group = -> [Mn_element001]
  conduct = 2
  density = 1
  expand = 3
  formula = Mn
  name = G4_Mn
  specific = 4
FEATURE [App::DocumentObjectGroupPython] Fe_element007  label="Fe_element : 004"  # scripted group (container) (typed FeaturePython)
  n = 1
  ref = Fe_element
FEATURE [App::DocumentObjectGroupPython] G4_Fe  # scripted group (container) (typed FeaturePython)
  Dunit = g/cm3
  Dvalue = 7.874
  Group = -> [Fe_element007]
  conduct = 2
  density = 1
  expand = 3
  formula = Fe
  name = G4_Fe
  specific = 4
FEATURE [App::DocumentObjectGroupPython] Co_element001  label="Co_element : 1"  # scripted group (container) (typed FeaturePython)
  n = 1
  ref = Co_element
FEATURE [App::DocumentObjectGroupPython] G4_Co  # scripted group (container) (typed FeaturePython)
  Dunit = g/cm3
  Dvalue = 8.9
  Group = -> [Co_element001]
  conduct = 2
  density = 1
  expand = 3
  formula = Co
  name = G4_Co
  specific = 4
FEATURE [App::DocumentObjectGroupPython] Ni_element001  label="Ni_element : 1"  # scripted group (container) (typed FeaturePython)
  n = 1
  ref = Ni_element
FEATURE [App::DocumentObjectGroupPython] G4_Ni  # scripted group (container) (typed FeaturePython)
  Dunit = g/cm3
  Dvalue = 8.902
  Group = -> [Ni_element001]
  conduct = 2
  density = 1
  expand = 3
  formula = Ni
  name = G4_Ni
  specific = 4
FEATURE [App::DocumentObjectGroupPython] Cu_element001  label="Cu_element : 1"  # scripted group (container) (typed FeaturePython)
  n = 1
  ref = Cu_element
FEATURE [App::DocumentObjectGroupPython] G4_Cu  # scripted group (container) (typed FeaturePython)
  Dunit = g/cm3
  Dvalue = 8.96
  Group = -> [Cu_element001]
  conduct = 2
  density = 1
  expand = 3
  formula = Cu
  name = G4_Cu
  specific = 4
FEATURE [App::DocumentObjectGroupPython] Zn_element001  label="Zn_element : 1"  # scripted group (container) (typed FeaturePython)
  n = 1
  ref = Zn_element
FEATURE [App::DocumentObjectGroupPython] G4_Zn  # scripted group (container) (typed FeaturePython)
  Dunit = g/cm3
  Dvalue = 7.133
  Group = -> [Zn_element001]
  conduct = 2
  density = 1
  expand = 3
  formula = Zn
  name = G4_Zn
  specific = 4
FEATURE [App::DocumentObjectGroupPython] Ga_element002  label="Ga_element : 002"  # scripted group (container) (typed FeaturePython)
  n = 1
  ref = Ga_element
FEATURE [App::DocumentObjectGroupPython] G4_Ga  # scripted group (container) (typed FeaturePython)
  Dunit = g/cm3
  Dvalue = 5.904
  Group = -> [Ga_element002]
  conduct = 2
  density = 1
  expand = 3
  formula = Ga
  name = G4_Ga
  specific = 4
FEATURE [App::DocumentObjectGroupPython] Ge_element002  label="Ge_element : 1"  # scripted group (container) (typed FeaturePython)
  n = 1
  ref = Ge_element
FEATURE [App::DocumentObjectGroupPython] G4_Ge  # scripted group (container) (typed FeaturePython)
  Dunit = g/cm3
  Dvalue = 5.323
  Group = -> [Ge_element002]
  conduct = 2
  density = 1
  expand = 3
  formula = Ge
  name = G4_Ge
  specific = 4
FEATURE [App::DocumentObjectGroupPython] As_element003  label="As_element : 002"  # scripted group (container) (typed FeaturePython)
  n = 1
  ref = As_element
FEATURE [App::DocumentObjectGroupPython] G4_As  # scripted group (container) (typed FeaturePython)
  Dunit = g/cm3
  Dvalue = 5.73
  Group = -> [As_element003]
  conduct = 2
  density = 1
  expand = 3
  formula = As
  name = G4_As
  specific = 4
FEATURE [App::DocumentObjectGroupPython] Se_element001  label="Se_element : 1"  # scripted group (container) (typed FeaturePython)
  n = 1
  ref = Se_element
FEATURE [App::DocumentObjectGroupPython] G4_Se  # scripted group (container) (typed FeaturePython)
  Dunit = g/cm3
  Dvalue = 4.5
  Group = -> [Se_element001]
  conduct = 2
  density = 1
  expand = 3
  formula = Se
  name = G4_Se
  specific = 4
FEATURE [App::DocumentObjectGroupPython] Br_element007  label="Br_element : 004"  # scripted group (container) (typed FeaturePython)
  n = 1
  ref = Br_element
FEATURE [App::DocumentObjectGroupPython] G4_Br  # scripted group (container) (typed FeaturePython)
  Dunit = g/cm3
  Dvalue = 0.0070721
  Group = -> [Br_element007]
  conduct = 2
  density = 1
  expand = 3
  formula = Br
  name = G4_Br
  specific = 4
FEATURE [App::DocumentObjectGroupPython] Kr_element001  label="Kr_element : 1"  # scripted group (container) (typed FeaturePython)
  n = 1
  ref = Kr_element
FEATURE [App::DocumentObjectGroupPython] G4_Kr  # scripted group (container) (typed FeaturePython)
  Dunit = g/cm3
  Dvalue = 0.00347832
  Group = -> [Kr_element001]
  conduct = 2
  density = 1
  expand = 3
  formula = Kr
  name = G4_Kr
  specific = 4
FEATURE [App::DocumentObjectGroupPython] Rb_element001  label="Rb_element : 1"  # scripted group (container) (typed FeaturePython)
  n = 1
  ref = Rb_element
FEATURE [App::DocumentObjectGroupPython] G4_Rb  # scripted group (container) (typed FeaturePython)
  Dunit = g/cm3
  Dvalue = 1.532
  Group = -> [Rb_element001]
  conduct = 2
  density = 1
  expand = 3
  formula = Rb
  name = G4_Rb
  specific = 4
FEATURE [App::DocumentObjectGroupPython] Sr_element001  label="Sr_element : 1"  # scripted group (container) (typed FeaturePython)
  n = 1
  ref = Sr_element
FEATURE [App::DocumentObjectGroupPython] G4_Sr  # scripted group (container) (typed FeaturePython)
  Dunit = g/cm3
  Dvalue = 2.54
  Group = -> [Sr_element001]
  conduct = 2
  density = 1
  expand = 3
  formula = Sr
  name = G4_Sr
  specific = 4
FEATURE [App::DocumentObjectGroupPython] Y_element001  label="Y_element : 1"  # scripted group (container) (typed FeaturePython)
  n = 1
  ref = Y_element
FEATURE [App::DocumentObjectGroupPython] G4_Y  # scripted group (container) (typed FeaturePython)
  Dunit = g/cm3
  Dvalue = 4.469
  Group = -> [Y_element001]
  conduct = 2
  density = 1
  expand = 3
  formula = Y
  name = G4_Y
  specific = 4
FEATURE [App::DocumentObjectGroupPython] Zr_element001  label="Zr_element : 1"  # scripted group (container) (typed FeaturePython)
  n = 1
  ref = Zr_element
FEATURE [App::DocumentObjectGroupPython] G4_Zr  # scripted group (container) (typed FeaturePython)
  Dunit = g/cm3
  Dvalue = 6.506
  Group = -> [Zr_element001]
  conduct = 2
  density = 1
  expand = 3
  formula = Zr
  name = G4_Zr
  specific = 4
FEATURE [App::DocumentObjectGroupPython] Nb_element001  label="Nb_element : 1"  # scripted group (container) (typed FeaturePython)
  n = 1
  ref = Nb_element
FEATURE [App::DocumentObjectGroupPython] G4_Nb  # scripted group (container) (typed FeaturePython)
  Dunit = g/cm3
  Dvalue = 8.57
  Group = -> [Nb_element001]
  conduct = 2
  density = 1
  expand = 3
  formula = Nb
  name = G4_Nb
  specific = 4
FEATURE [App::DocumentObjectGroupPython] Mo_element001  label="Mo_element : 1"  # scripted group (container) (typed FeaturePython)
  n = 1
  ref = Mo_element
FEATURE [App::DocumentObjectGroupPython] G4_Mo  # scripted group (container) (typed FeaturePython)
  Dunit = g/cm3
  Dvalue = 10.22
  Group = -> [Mo_element001]
  conduct = 2
  density = 1
  expand = 3
  formula = Mo
  name = G4_Mo
  specific = 4
FEATURE [App::DocumentObjectGroupPython] Tc_element001  label="Tc_element : 1"  # scripted group (container) (typed FeaturePython)
  n = 1
  ref = Tc_element
FEATURE [App::DocumentObjectGroupPython] G4_Tc  # scripted group (container) (typed FeaturePython)
  Dunit = g/cm3
  Dvalue = 11.5
  Group = -> [Tc_element001]
  conduct = 2
  density = 1
  expand = 3
  formula = Tc
  name = G4_Tc
  specific = 4
FEATURE [App::DocumentObjectGroupPython] Ru_element001  label="Ru_element : 1"  # scripted group (container) (typed FeaturePython)
  n = 1
  ref = Ru_element
FEATURE [App::DocumentObjectGroupPython] G4_Ru  # scripted group (container) (typed FeaturePython)
  Dunit = g/cm3
  Dvalue = 12.41
  Group = -> [Ru_element001]
  conduct = 2
  density = 1
  expand = 3
  formula = Ru
  name = G4_Ru
  specific = 4
FEATURE [App::DocumentObjectGroupPython] Rh_element001  label="Rh_element : 1"  # scripted group (container) (typed FeaturePython)
  n = 1
  ref = Rh_element
FEATURE [App::DocumentObjectGroupPython] G4_Rh  # scripted group (container) (typed FeaturePython)
  Dunit = g/cm3
  Dvalue = 12.41
  Group = -> [Rh_element001]
  conduct = 2
  density = 1
  expand = 3
  formula = Rh
  name = G4_Rh
  specific = 4
FEATURE [App::DocumentObjectGroupPython] Pd_element001  label="Pd_element : 1"  # scripted group (container) (typed FeaturePython)
  n = 1
  ref = Pd_element
FEATURE [App::DocumentObjectGroupPython] G4_Pd  # scripted group (container) (typed FeaturePython)
  Dunit = g/cm3
  Dvalue = 12.02
  Group = -> [Pd_element001]
  conduct = 2
  density = 1
  expand = 3
  formula = Pd
  name = G4_Pd
  specific = 4
FEATURE [App::DocumentObjectGroupPython] Ag_element006  label="Ag_element : 004"  # scripted group (container) (typed FeaturePython)
  n = 1
  ref = Ag_element
FEATURE [App::DocumentObjectGroupPython] G4_Ag  # scripted group (container) (typed FeaturePython)
  Dunit = g/cm3
  Dvalue = 10.5
  Group = -> [Ag_element006]
  conduct = 2
  density = 1
  expand = 3
  formula = Ag
  name = G4_Ag
  specific = 4
FEATURE [App::DocumentObjectGroupPython] Cd_element003  label="Cd_element : 003"  # scripted group (container) (typed FeaturePython)
  n = 1
  ref = Cd_element
FEATURE [App::DocumentObjectGroupPython] G4_Cd  # scripted group (container) (typed FeaturePython)
  Dunit = g/cm3
  Dvalue = 8.65
  Group = -> [Cd_element003]
  conduct = 2
  density = 1
  expand = 3
  formula = Cd
  name = G4_Cd
  specific = 4
FEATURE [App::DocumentObjectGroupPython] In_element001  label="In_element : 1"  # scripted group (container) (typed FeaturePython)
  n = 1
  ref = In_element
FEATURE [App::DocumentObjectGroupPython] G4_In  # scripted group (container) (typed FeaturePython)
  Dunit = g/cm3
  Dvalue = 7.31
  Group = -> [In_element001]
  conduct = 2
  density = 1
  expand = 3
  formula = In
  name = G4_In
  specific = 4
FEATURE [App::DocumentObjectGroupPython] Sn_element001  label="Sn_element : 1"  # scripted group (container) (typed FeaturePython)
  n = 1
  ref = Sn_element
FEATURE [App::DocumentObjectGroupPython] G4_Sn  # scripted group (container) (typed FeaturePython)
  Dunit = g/cm3
  Dvalue = 7.31
  Group = -> [Sn_element001]
  conduct = 2
  density = 1
  expand = 3
  formula = Sn
  name = G4_Sn
  specific = 4
FEATURE [App::DocumentObjectGroupPython] Sb_element001  label="Sb_element : 1"  # scripted group (container) (typed FeaturePython)
  n = 1
  ref = Sb_element
FEATURE [App::DocumentObjectGroupPython] G4_Sb  # scripted group (container) (typed FeaturePython)
  Dunit = g/cm3
  Dvalue = 6.691
  Group = -> [Sb_element001]
  conduct = 2
  density = 1
  expand = 3
  formula = Sb
  name = G4_Sb
  specific = 4
FEATURE [App::DocumentObjectGroupPython] Te_element002  label="Te_element : 002"  # scripted group (container) (typed FeaturePython)
  n = 1
  ref = Te_element
FEATURE [App::DocumentObjectGroupPython] G4_Te  # scripted group (container) (typed FeaturePython)
  Dunit = g/cm3
  Dvalue = 6.24
  Group = -> [Te_element002]
  conduct = 2
  density = 1
  expand = 3
  formula = Te
  name = G4_Te
  specific = 4
FEATURE [App::DocumentObjectGroupPython] I_element010  label="I_element : 006"  # scripted group (container) (typed FeaturePython)
  n = 1
  ref = I_element
FEATURE [App::DocumentObjectGroupPython] G4_I  # scripted group (container) (typed FeaturePython)
  Dunit = g/cm3
  Dvalue = 4.93
  Group = -> [I_element010]
  conduct = 2
  density = 1
  expand = 3
  formula = I
  name = G4_I
  specific = 4
FEATURE [App::DocumentObjectGroupPython] Xe_element001  label="Xe_element : 1"  # scripted group (container) (typed FeaturePython)
  n = 1
  ref = Xe_element
FEATURE [App::DocumentObjectGroupPython] G4_Xe  # scripted group (container) (typed FeaturePython)
  Dunit = g/cm3
  Dvalue = 0.00548536
  Group = -> [Xe_element001]
  conduct = 2
  density = 1
  expand = 3
  formula = Xe
  name = G4_Xe
  specific = 4
FEATURE [App::DocumentObjectGroupPython] Cs_element003  label="Cs_element : 003"  # scripted group (container) (typed FeaturePython)
  n = 1
  ref = Cs_element
FEATURE [App::DocumentObjectGroupPython] G4_Cs  # scripted group (container) (typed FeaturePython)
  Dunit = g/cm3
  Dvalue = 1.873
  Group = -> [Cs_element003]
  conduct = 2
  density = 1
  expand = 3
  formula = Cs
  name = G4_Cs
  specific = 4
FEATURE [App::DocumentObjectGroupPython] Ba_element003  label="Ba_element : 003"  # scripted group (container) (typed FeaturePython)
  n = 1
  ref = Ba_element
FEATURE [App::DocumentObjectGroupPython] G4_Ba  # scripted group (container) (typed FeaturePython)
  Dunit = g/cm3
  Dvalue = 3.5
  Group = -> [Ba_element003]
  conduct = 2
  density = 1
  expand = 3
  formula = Ba
  name = G4_Ba
  specific = 4
FEATURE [App::DocumentObjectGroupPython] La_element003  label="La_element : 003"  # scripted group (container) (typed FeaturePython)
  n = 1
  ref = La_element
FEATURE [App::DocumentObjectGroupPython] G4_La  # scripted group (container) (typed FeaturePython)
  Dunit = g/cm3
  Dvalue = 6.154
  Group = -> [La_element003]
  conduct = 2
  density = 1
  expand = 3
  formula = La
  name = G4_La
  specific = 4
FEATURE [App::DocumentObjectGroupPython] Ce_element002  label="Ce_element : 1"  # scripted group (container) (typed FeaturePython)
  n = 1
  ref = Ce_element
FEATURE [App::DocumentObjectGroupPython] G4_Ce  # scripted group (container) (typed FeaturePython)
  Dunit = g/cm3
  Dvalue = 6.657
  Group = -> [Ce_element002]
  conduct = 2
  density = 1
  expand = 3
  formula = Ce
  name = G4_Ce
  specific = 4
FEATURE [App::DocumentObjectGroupPython] Pr_element001  label="Pr_element : 1"  # scripted group (container) (typed FeaturePython)
  n = 1
  ref = Pr_element
FEATURE [App::DocumentObjectGroupPython] G4_Pr  # scripted group (container) (typed FeaturePython)
  Dunit = g/cm3
  Dvalue = 6.71
  Group = -> [Pr_element001]
  conduct = 2
  density = 1
  expand = 3
  formula = Pr
  name = G4_Pr
  specific = 4
FEATURE [App::DocumentObjectGroupPython] Nd_element001  label="Nd_element : 1"  # scripted group (container) (typed FeaturePython)
  n = 1
  ref = Nd_element
FEATURE [App::DocumentObjectGroupPython] G4_Nd  # scripted group (container) (typed FeaturePython)
  Dunit = g/cm3
  Dvalue = 6.9
  Group = -> [Nd_element001]
  conduct = 2
  density = 1
  expand = 3
  formula = Nd
  name = G4_Nd
  specific = 4
FEATURE [App::DocumentObjectGroupPython] Pm_element001  label="Pm_element : 1"  # scripted group (container) (typed FeaturePython)
  n = 1
  ref = Pm_element
FEATURE [App::DocumentObjectGroupPython] G4_Pm  # scripted group (container) (typed FeaturePython)
  Dunit = g/cm3
  Dvalue = 7.22
  Group = -> [Pm_element001]
  conduct = 2
  density = 1
  expand = 3
  formula = Pm
  name = G4_Pm
  specific = 4
FEATURE [App::DocumentObjectGroupPython] Sm_element001  label="Sm_element : 1"  # scripted group (container) (typed FeaturePython)
  n = 1
  ref = Sm_element
FEATURE [App::DocumentObjectGroupPython] G4_Sm  # scripted group (container) (typed FeaturePython)
  Dunit = g/cm3
  Dvalue = 7.46
  Group = -> [Sm_element001]
  conduct = 2
  density = 1
  expand = 3
  formula = Sm
  name = G4_Sm
  specific = 4
FEATURE [App::DocumentObjectGroupPython] Eu_element001  label="Eu_element : 1"  # scripted group (container) (typed FeaturePython)
  n = 1
  ref = Eu_element
FEATURE [App::DocumentObjectGroupPython] G4_Eu  # scripted group (container) (typed FeaturePython)
  Dunit = g/cm3
  Dvalue = 5.243
  Group = -> [Eu_element001]
  conduct = 2
  density = 1
  expand = 3
  formula = Eu
  name = G4_Eu
  specific = 4
FEATURE [App::DocumentObjectGroupPython] Gd_element002  label="Gd_element : 1"  # scripted group (container) (typed FeaturePython)
  n = 1
  ref = Gd_element
FEATURE [App::DocumentObjectGroupPython] G4_Gd  # scripted group (container) (typed FeaturePython)
  Dunit = g/cm3
  Dvalue = 7.9004
  Group = -> [Gd_element002]
  conduct = 2
  density = 1
  expand = 3
  formula = Gd
  name = G4_Gd
  specific = 4
FEATURE [App::DocumentObjectGroupPython] Tb_element001  label="Tb_element : 1"  # scripted group (container) (typed FeaturePython)
  n = 1
  ref = Tb_element
FEATURE [App::DocumentObjectGroupPython] G4_Tb  # scripted group (container) (typed FeaturePython)
  Dunit = g/cm3
  Dvalue = 8.229
  Group = -> [Tb_element001]
  conduct = 2
  density = 1
  expand = 3
  formula = Tb
  name = G4_Tb
  specific = 4
FEATURE [App::DocumentObjectGroupPython] Dy_element001  label="Dy_element : 1"  # scripted group (container) (typed FeaturePython)
  n = 1
  ref = Dy_element
FEATURE [App::DocumentObjectGroupPython] G4_Dy  # scripted group (container) (typed FeaturePython)
  Dunit = g/cm3
  Dvalue = 8.55
  Group = -> [Dy_element001]
  conduct = 2
  density = 1
  expand = 3
  formula = Dy
  name = G4_Dy
  specific = 4
FEATURE [App::DocumentObjectGroupPython] Ho_element001  label="Ho_element : 1"  # scripted group (container) (typed FeaturePython)
  n = 1
  ref = Ho_element
FEATURE [App::DocumentObjectGroupPython] G4_Ho  # scripted group (container) (typed FeaturePython)
  Dunit = g/cm3
  Dvalue = 8.795
  Group = -> [Ho_element001]
  conduct = 2
  density = 1
  expand = 3
  formula = Ho
  name = G4_Ho
  specific = 4
FEATURE [App::DocumentObjectGroupPython] Er_element001  label="Er_element : 1"  # scripted group (container) (typed FeaturePython)
  n = 1
  ref = Er_element
FEATURE [App::DocumentObjectGroupPython] G4_Er  # scripted group (container) (typed FeaturePython)
  Dunit = g/cm3
  Dvalue = 9.066
  Group = -> [Er_element001]
  conduct = 2
  density = 1
  expand = 3
  formula = Er
  name = G4_Er
  specific = 4
FEATURE [App::DocumentObjectGroupPython] Tm_element001  label="Tm_element : 1"  # scripted group (container) (typed FeaturePython)
  n = 1
  ref = Tm_element
FEATURE [App::DocumentObjectGroupPython] G4_Tm  # scripted group (container) (typed FeaturePython)
  Dunit = g/cm3
  Dvalue = 9.321
  Group = -> [Tm_element001]
  conduct = 2
  density = 1
  expand = 3
  formula = Tm
  name = G4_Tm
  specific = 4
FEATURE [App::DocumentObjectGroupPython] Yb_element001  label="Yb_element : 1"  # scripted group (container) (typed FeaturePython)
  n = 1
  ref = Yb_element
FEATURE [App::DocumentObjectGroupPython] G4_Yb  # scripted group (container) (typed FeaturePython)
  Dunit = g/cm3
  Dvalue = 6.73
  Group = -> [Yb_element001]
  conduct = 2
  density = 1
  expand = 3
  formula = Yb
  name = G4_Yb
  specific = 4
FEATURE [App::DocumentObjectGroupPython] Lu_element001  label="Lu_element : 1"  # scripted group (container) (typed FeaturePython)
  n = 1
  ref = Lu_element
FEATURE [App::DocumentObjectGroupPython] G4_Lu  # scripted group (container) (typed FeaturePython)
  Dunit = g/cm3
  Dvalue = 9.84
  Group = -> [Lu_element001]
  conduct = 2
  density = 1
  expand = 3
  formula = Lu
  name = G4_Lu
  specific = 4
FEATURE [App::DocumentObjectGroupPython] Hf_element001  label="Hf_element : 1"  # scripted group (container) (typed FeaturePython)
  n = 1
  ref = Hf_element
FEATURE [App::DocumentObjectGroupPython] G4_Hf  # scripted group (container) (typed FeaturePython)
  Dunit = g/cm3
  Dvalue = 13.31
  Group = -> [Hf_element001]
  conduct = 2
  density = 1
  expand = 3
  formula = Hf
  name = G4_Hf
  specific = 4
FEATURE [App::DocumentObjectGroupPython] Ta_element001  label="Ta_element : 1"  # scripted group (container) (typed FeaturePython)
  n = 1
  ref = Ta_element
FEATURE [App::DocumentObjectGroupPython] G4_Ta  # scripted group (container) (typed FeaturePython)
  Dunit = g/cm3
  Dvalue = 16.654
  Group = -> [Ta_element001]
  conduct = 2
  density = 1
  expand = 3
  formula = Ta
  name = G4_Ta
  specific = 4
FEATURE [App::DocumentObjectGroupPython] W_element004  label="W_element : 004"  # scripted group (container) (typed FeaturePython)
  n = 1
  ref = W_element
FEATURE [App::DocumentObjectGroupPython] G4_W  # scripted group (container) (typed FeaturePython)
  Dunit = g/cm3
  Dvalue = 19.3
  Group = -> [W_element004]
  conduct = 2
  density = 1
  expand = 3
  formula = W
  name = G4_W
  specific = 4
FEATURE [App::DocumentObjectGroupPython] Re_element001  label="Re_element : 1"  # scripted group (container) (typed FeaturePython)
  n = 1
  ref = Re_element
FEATURE [App::DocumentObjectGroupPython] G4_Re  # scripted group (container) (typed FeaturePython)
  Dunit = g/cm3
  Dvalue = 21.02
  Group = -> [Re_element001]
  conduct = 2
  density = 1
  expand = 3
  formula = Re
  name = G4_Re
  specific = 4
FEATURE [App::DocumentObjectGroupPython] Os_element001  label="Os_element : 1"  # scripted group (container) (typed FeaturePython)
  n = 1
  ref = Os_element
FEATURE [App::DocumentObjectGroupPython] G4_Os  # scripted group (container) (typed FeaturePython)
  Dunit = g/cm3
  Dvalue = 22.57
  Group = -> [Os_element001]
  conduct = 2
  density = 1
  expand = 3
  formula = Os
  name = G4_Os
  specific = 4
FEATURE [App::DocumentObjectGroupPython] Ir_element001  label="Ir_element : 1"  # scripted group (container) (typed FeaturePython)
  n = 1
  ref = Ir_element
FEATURE [App::DocumentObjectGroupPython] G4_Ir  # scripted group (container) (typed FeaturePython)
  Dunit = g/cm3
  Dvalue = 22.42
  Group = -> [Ir_element001]
  conduct = 2
  density = 1
  expand = 3
  formula = Ir
  name = G4_Ir
  specific = 4
FEATURE [App::DocumentObjectGroupPython] Pt_element001  label="Pt_element : 1"  # scripted group (container) (typed FeaturePython)
  n = 1
  ref = Pt_element
FEATURE [App::DocumentObjectGroupPython] G4_Pt  # scripted group (container) (typed FeaturePython)
  Dunit = g/cm3
  Dvalue = 21.45
  Group = -> [Pt_element001]
  conduct = 2
  density = 1
  expand = 3
  formula = Pt
  name = G4_Pt
  specific = 4
FEATURE [App::DocumentObjectGroupPython] Au_element001  label="Au_element : 1"  # scripted group (container) (typed FeaturePython)
  n = 1
  ref = Au_element
FEATURE [App::DocumentObjectGroupPython] G4_Au  # scripted group (container) (typed FeaturePython)
  Dunit = g/cm3
  Dvalue = 19.32
  Group = -> [Au_element001]
  conduct = 2
  density = 1
  expand = 3
  formula = Au
  name = G4_Au
  specific = 4
FEATURE [App::DocumentObjectGroupPython] Hg_element002  label="Hg_element : 002"  # scripted group (container) (typed FeaturePython)
  n = 1
  ref = Hg_element
FEATURE [App::DocumentObjectGroupPython] G4_Hg  # scripted group (container) (typed FeaturePython)
  Dunit = g/cm3
  Dvalue = 13.546
  Group = -> [Hg_element002]
  conduct = 2
  density = 1
  expand = 3
  formula = Hg
  name = G4_Hg
  specific = 4
FEATURE [App::DocumentObjectGroupPython] Tl_element002  label="Tl_element : 002"  # scripted group (container) (typed FeaturePython)
  n = 1
  ref = Tl_element
FEATURE [App::DocumentObjectGroupPython] G4_Tl  # scripted group (container) (typed FeaturePython)
  Dunit = g/cm3
  Dvalue = 11.72
  Group = -> [Tl_element002]
  conduct = 2
  density = 1
  expand = 3
  formula = Tl
  name = G4_Tl
  specific = 4
FEATURE [App::DocumentObjectGroupPython] Pb_element003  label="Pb_element : 1"  # scripted group (container) (typed FeaturePython)
  n = 1
  ref = Pb_element
FEATURE [App::DocumentObjectGroupPython] G4_Pb  # scripted group (container) (typed FeaturePython)
  Dunit = g/cm3
  Dvalue = 11.35
  Group = -> [Pb_element003]
  conduct = 2
  density = 1
  expand = 3
  formula = Pb
  name = G4_Pb
  specific = 4
FEATURE [App::DocumentObjectGroupPython] Bi_element002  label="Bi_element : 1"  # scripted group (container) (typed FeaturePython)
  n = 1
  ref = Bi_element
FEATURE [App::DocumentObjectGroupPython] G4_Bi  # scripted group (container) (typed FeaturePython)
  Dunit = g/cm3
  Dvalue = 9.747
  Group = -> [Bi_element002]
  conduct = 2
  density = 1
  expand = 3
  formula = Bi
  name = G4_Bi
  specific = 4
FEATURE [App::DocumentObjectGroupPython] Po_element001  label="Po_element : 1"  # scripted group (container) (typed FeaturePython)
  n = 1
  ref = Po_element
FEATURE [App::DocumentObjectGroupPython] G4_Po  # scripted group (container) (typed FeaturePython)
  Dunit = g/cm3
  Dvalue = 9.32
  Group = -> [Po_element001]
  conduct = 2
  density = 1
  expand = 3
  formula = Po
  name = G4_Po
  specific = 4
FEATURE [App::DocumentObjectGroupPython] At_element001  label="At_element : 1"  # scripted group (container) (typed FeaturePython)
  n = 1
  ref = At_element
FEATURE [App::DocumentObjectGroupPython] G4_At  # scripted group (container) (typed FeaturePython)
  Dunit = g/cm3
  Dvalue = 9.32
  Group = -> [At_element001]
  conduct = 2
  density = 1
  expand = 3
  formula = At
  name = G4_At
  specific = 4
FEATURE [App::DocumentObjectGroupPython] Rn_element001  label="Rn_element : 1"  # scripted group (container) (typed FeaturePython)
  n = 1
  ref = Rn_element
FEATURE [App::DocumentObjectGroupPython] G4_Rn  # scripted group (container) (typed FeaturePython)
  Dunit = g/cm3
  Dvalue = 0.00900662
  Group = -> [Rn_element001]
  conduct = 2
  density = 1
  expand = 3
  formula = Rn
  name = G4_Rn
  specific = 4
FEATURE [App::DocumentObjectGroupPython] Fr_element001  label="Fr_element : 1"  # scripted group (container) (typed FeaturePython)
  n = 1
  ref = Fr_element
FEATURE [App::DocumentObjectGroupPython] G4_Fr  # scripted group (container) (typed FeaturePython)
  Dunit = g/cm3
  Dvalue = 1
  Group = -> [Fr_element001]
  conduct = 2
  density = 1
  expand = 3
  formula = Fr
  name = G4_Fr
  specific = 4
FEATURE [App::DocumentObjectGroupPython] Ra_element001  label="Ra_element : 1"  # scripted group (container) (typed FeaturePython)
  n = 1
  ref = Ra_element
FEATURE [App::DocumentObjectGroupPython] G4_Ra  # scripted group (container) (typed FeaturePython)
  Dunit = g/cm3
  Dvalue = 5
  Group = -> [Ra_element001]
  conduct = 2
  density = 1
  expand = 3
  formula = Ra
  name = G4_Ra
  specific = 4
FEATURE [App::DocumentObjectGroupPython] Ac_element001  label="Ac_element : 1"  # scripted group (container) (typed FeaturePython)
  n = 1
  ref = Ac_element
FEATURE [App::DocumentObjectGroupPython] G4_Ac  # scripted group (container) (typed FeaturePython)
  Dunit = g/cm3
  Dvalue = 10.07
  Group = -> [Ac_element001]
  conduct = 2
  density = 1
  expand = 3
  formula = Ac
  name = G4_Ac
  specific = 4
FEATURE [App::DocumentObjectGroupPython] Th_element001  label="Th_element : 1"  # scripted group (container) (typed FeaturePython)
  n = 1
  ref = Th_element
FEATURE [App::DocumentObjectGroupPython] G4_Th  # scripted group (container) (typed FeaturePython)
  Dunit = g/cm3
  Dvalue = 11.72
  Group = -> [Th_element001]
  conduct = 2
  density = 1
  expand = 3
  formula = Th
  name = G4_Th
  specific = 4
FEATURE [App::DocumentObjectGroupPython] Pa_element001  label="Pa_element : 1"  # scripted group (container) (typed FeaturePython)
  n = 1
  ref = Pa_element
FEATURE [App::DocumentObjectGroupPython] G4_Pa  # scripted group (container) (typed FeaturePython)
  Dunit = g/cm3
  Dvalue = 15.37
  Group = -> [Pa_element001]
  conduct = 2
  density = 1
  expand = 3
  formula = Pa
  name = G4_Pa
  specific = 4
FEATURE [App::DocumentObjectGroupPython] U_element004  label="U_element : 004"  # scripted group (container) (typed FeaturePython)
  n = 1
  ref = U_element
FEATURE [App::DocumentObjectGroupPython] G4_U  # scripted group (container) (typed FeaturePython)
  Dunit = g/cm3
  Dvalue = 18.95
  Group = -> [U_element004]
  conduct = 2
  density = 1
  expand = 3
  formula = U
  name = G4_U
  specific = 4
FEATURE [App::DocumentObjectGroupPython] Np_element001  label="Np_element : 1"  # scripted group (container) (typed FeaturePython)
  n = 1
  ref = Np_element
FEATURE [App::DocumentObjectGroupPython] G4_Np  # scripted group (container) (typed FeaturePython)
  Dunit = g/cm3
  Dvalue = 20.25
  Group = -> [Np_element001]
  conduct = 2
  density = 1
  expand = 3
  formula = Np
  name = G4_Np
  specific = 4
FEATURE [App::DocumentObjectGroupPython] Pu_element002  label="Pu_element : 002"  # scripted group (container) (typed FeaturePython)
  n = 1
  ref = Pu_element
FEATURE [App::DocumentObjectGroupPython] G4_Pu  # scripted group (container) (typed FeaturePython)
  Dunit = g/cm3
  Dvalue = 19.84
  Group = -> [Pu_element002]
  conduct = 2
  density = 1
  expand = 3
  formula = Pu
  name = G4_Pu
  specific = 4
FEATURE [App::DocumentObjectGroupPython] Am_element001  label="Am_element : 1"  # scripted group (container) (typed FeaturePython)
  n = 1
  ref = Am_element
FEATURE [App::DocumentObjectGroupPython] G4_Am  # scripted group (container) (typed FeaturePython)
  Dunit = g/cm3
  Dvalue = 13.67
  Group = -> [Am_element001]
  conduct = 2
  density = 1
  expand = 3
  formula = Am
  name = G4_Am
  specific = 4
FEATURE [App::DocumentObjectGroupPython] Cm_element001  label="Cm_element : 1"  # scripted group (container) (typed FeaturePython)
  n = 1
  ref = Cm_element
FEATURE [App::DocumentObjectGroupPython] G4_Cm  # scripted group (container) (typed FeaturePython)
  Dunit = g/cm3
  Dvalue = 13.51
  Group = -> [Cm_element001]
  conduct = 2
  density = 1
  expand = 3
  formula = Cm
  name = G4_Cm
  specific = 4
FEATURE [App::DocumentObjectGroupPython] Bk_element001  label="Bk_element : 1"  # scripted group (container) (typed FeaturePython)
  n = 1
  ref = Bk_element
FEATURE [App::DocumentObjectGroupPython] G4_Bk  # scripted group (container) (typed FeaturePython)
  Dunit = g/cm3
  Dvalue = 14
  Group = -> [Bk_element001]
  conduct = 2
  density = 1
  expand = 3
  formula = Bk
  name = G4_Bk
  specific = 4
FEATURE [App::DocumentObjectGroupPython] Cf_element001  label="Cf_element : 1"  # scripted group (container) (typed FeaturePython)
  n = 1
  ref = Cf_element
FEATURE [App::DocumentObjectGroupPython] G4_Cf  # scripted group (container) (typed FeaturePython)
  Dunit = g/cm3
  Dvalue = 10
  Group = -> [Cf_element001]
  conduct = 2
  density = 1
  expand = 3
  formula = Cf
  name = G4_Cf
  specific = 4
FEATURE [App::DocumentObjectGroupPython] Element  # scripted group (container) (typed FeaturePython)
  Group = -> [G4_H,G4_He,G4_Li,G4_Be,G4_B,G4_C,G4_N,G4_O,G4_F,G4_Ne,G4_Na,G4_Mg,G4_Al,G4_Si,G4_P,G4_S,G4_Cl,G4_Ar,G4_K,G4_Ca,G4_Sc,G4_Ti,G4_V,G4_Cr,G4_Mn,G4_Fe,G4_Co,G4_Ni,G4_Cu,G4_Zn,G4_Ga,G4_Ge,G4_As,G4_Se,G4_Br,G4_Kr,G4_Rb,G4_Sr,G4_Y,G4_Zr,G4_Nb,G4_Mo,G4_Tc,G4_Ru,G4_Rh,G4_Pd,G4_Ag,G4_Cd,G4_In,G4_Sn,G4_Sb,G4_Te,G4_I,G4_Xe,G4_Cs,G4_Ba,G4_La,G4_Ce,G4_Pr,G4_Nd,G4_Pm,G4_Sm,G4_Eu,G4_Gd,G4_Tb,G4_Dy,G4_Ho,G4_Er,+30 more]
FEATURE [App::DocumentObjectGroupPython] H_element114  label="H_element : 063"  # scripted group (container) (typed FeaturePython)
  n = 2
  ref = H_element
FEATURE [App::DocumentObjectGroupPython] G4_lH2  # scripted group (container) (typed FeaturePython)
  Dunit = g/cm3
  Dvalue = 0.0708
  Group = -> [H_element114]
  conduct = 2
  density = 1
  expand = 3
  formula = G4_lH2
  name = G4_lH2
  specific = 4
FEATURE [App::DocumentObjectGroupPython] N_element049  label="N_element : 022"  # scripted group (container) (typed FeaturePython)
  n = 2
  ref = N_element
FEATURE [App::DocumentObjectGroupPython] G4_lN2  # scripted group (container) (typed FeaturePython)
  Dunit = g/cm3
  Dvalue = 0.807
  Group = -> [N_element049]
  conduct = 2
  density = 1
  expand = 3
  formula = G4_lN2
  name = G4_lN2
  specific = 4
FEATURE [App::DocumentObjectGroupPython] O_element106  label="O_element : 060"  # scripted group (container) (typed FeaturePython)
  n = 2
  ref = O_element
FEATURE [App::DocumentObjectGroupPython] G4_lO2  # scripted group (container) (typed FeaturePython)
  Dunit = g/cm3
  Dvalue = 1.141
  Group = -> [O_element106]
  conduct = 2
  density = 1
  expand = 3
  formula = G4_lO2
  name = G4_lO2
  specific = 4
FEATURE [App::DocumentObjectGroupPython] Ar_element003  label="Ar_element : 002"  # scripted group (container) (typed FeaturePython)
  n = 1
  ref = Ar_element
FEATURE [App::DocumentObjectGroupPython] G4_lAr  # scripted group (container) (typed FeaturePython)
  Dunit = g/cm3
  Dvalue = 1.396
  Group = -> [Ar_element003]
  conduct = 2
  density = 1
  expand = 3
  formula = G4_lAr
  name = G4_lAr
  specific = 4
FEATURE [App::DocumentObjectGroupPython] Br_element008  label="Br_element : 005"  # scripted group (container) (typed FeaturePython)
  n = 1
  ref = Br_element
FEATURE [App::DocumentObjectGroupPython] G4_lBr  # scripted group (container) (typed FeaturePython)
  Dunit = g/cm3
  Dvalue = 3.1028
  Group = -> [Br_element008]
  conduct = 2
  density = 1
  expand = 3
  formula = G4_lBr
  name = G4_lBr
  specific = 4
FEATURE [App::DocumentObjectGroupPython] Kr_element002  label="Kr_element : 002"  # scripted group (container) (typed FeaturePython)
  n = 1
  ref = Kr_element
FEATURE [App::DocumentObjectGroupPython] G4_lKr  # scripted group (container) (typed FeaturePython)
  Dunit = g/cm3
  Dvalue = 2.418
  Group = -> [Kr_element002]
  conduct = 2
  density = 1
  expand = 3
  formula = G4_lKr
  name = G4_lKr
  specific = 4
FEATURE [App::DocumentObjectGroupPython] Xe_element002  label="Xe_element : 002"  # scripted group (container) (typed FeaturePython)
  n = 1
  ref = Xe_element
FEATURE [App::DocumentObjectGroupPython] G4_lXe  # scripted group (container) (typed FeaturePython)
  Dunit = g/cm3
  Dvalue = 2.953
  Group = -> [Xe_element002]
  conduct = 2
  density = 1
  expand = 3
  formula = G4_lXe
  name = G4_lXe
  specific = 4
FEATURE [App::DocumentObjectGroupPython] O_element107  label="O_element : 061"  # scripted group (container) (typed FeaturePython)
  n = 4
  ref = O_element
FEATURE [App::DocumentObjectGroupPython] Pb_element004  label="Pb_element : 002"  # scripted group (container) (typed FeaturePython)
  n = 1
  ref = Pb_element
FEATURE [App::DocumentObjectGroupPython] W_element005  label="W_element : 005"  # scripted group (container) (typed FeaturePython)
  n = 1
  ref = W_element
FEATURE [App::DocumentObjectGroupPython] G4_PbWO4  # scripted group (container) (typed FeaturePython)
  Dunit = g/cm3
  Dvalue = 8.28
  Group = -> [O_element107,Pb_element004,W_element005]
  conduct = 2
  density = 1
  expand = 3
  formula = G4_PbWO4
  name = G4_PbWO4
  specific = 4
FEATURE [App::DocumentObjectGroupPython] H_element115  label="H_element : 064"  # scripted group (container) (typed FeaturePython)
  n = 1
  ref = H_element
FEATURE [App::DocumentObjectGroupPython] G4_Galactic  # scripted group (container) (typed FeaturePython)
  Dunit = g/cm3
  Dvalue = 0
  Group = -> [H_element115]
  conduct = 2
  density = 1
  expand = 3
  formula = G4_Galactic
  name = G4_Galactic
  specific = 4
FEATURE [App::DocumentObjectGroupPython] C_element125  label="C_element : 071"  # scripted group (container) (typed FeaturePython)
  n = 1
  ref = C_element
FEATURE [App::DocumentObjectGroupPython] G4_GRAPHITE_POROUS  # scripted group (container) (typed FeaturePython)
  Dunit = g/cm3
  Dvalue = 1.7
  Group = -> [C_element125]
  conduct = 2
  density = 1
  expand = 3
  formula = G4_GRAPHITE_POROUS
  name = G4_GRAPHITE_POROUS
  specific = 4
FEATURE [App::DocumentObjectGroupPython] H_element116  label="H_element : 0.150"  # scripted group (container) (typed FeaturePython)
  n = 0.080538
FEATURE [App::DocumentObjectGroupPython] C_element126  label="C_element : 0.600"  # scripted group (container) (typed FeaturePython)
  n = 0.599848
FEATURE [App::DocumentObjectGroupPython] O_element108  label="O_element : 0.320"  # scripted group (container) (typed FeaturePython)
  n = 0.319614
FEATURE [App::DocumentObjectGroupPython] G4_LUCITE  # scripted group (container) (typed FeaturePython)
  Dunit = g/cm3
  Dvalue = 1.19
  Group = -> [H_element116,C_element126,O_element108]
  conduct = 2
  density = 1
  expand = 3
  formula = G4_LUCITE
  name = G4_LUCITE
  specific = 4
FEATURE [App::DocumentObjectGroupPython] Cu_element002  label="Cu_element : 62"  # scripted group (container) (typed FeaturePython)
  n = 62
  ref = Cu_element
FEATURE [App::DocumentObjectGroupPython] Zn_element002  label="Zn_element : 35"  # scripted group (container) (typed FeaturePython)
  n = 35
  ref = Zn_element
FEATURE [App::DocumentObjectGroupPython] Pb_element005  label="Pb_element : 3"  # scripted group (container) (typed FeaturePython)
  n = 3
  ref = Pb_element
FEATURE [App::DocumentObjectGroupPython] G4_BRASS  # scripted group (container) (typed FeaturePython)
  Dunit = g/cm3
  Dvalue = 8.52
  Group = -> [Cu_element002,Zn_element002,Pb_element005]
  conduct = 2
  density = 1
  expand = 3
  formula = G4_BRASS
  name = G4_BRASS
  specific = 4
FEATURE [App::DocumentObjectGroupPython] Cu_element003  label="Cu_element : 89"  # scripted group (container) (typed FeaturePython)
  n = 89
  ref = Cu_element
FEATURE [App::DocumentObjectGroupPython] Zn_element003  label="Zn_element : 9"  # scripted group (container) (typed FeaturePython)
  n = 9
  ref = Zn_element
FEATURE [App::DocumentObjectGroupPython] Pb_element006  label="Pb_element : 2"  # scripted group (container) (typed FeaturePython)
  n = 2
  ref = Pb_element
FEATURE [App::DocumentObjectGroupPython] G4_BRONZE  # scripted group (container) (typed FeaturePython)
  Dunit = g/cm3
  Dvalue = 8.82
  Group = -> [Cu_element003,Zn_element003,Pb_element006]
  conduct = 2
  density = 1
  expand = 3
  formula = G4_BRONZE
  name = G4_BRONZE
  specific = 4
FEATURE [App::DocumentObjectGroupPython] Fe_element008  label="Fe_element : 74"  # scripted group (container) (typed FeaturePython)
  n = 74
  ref = Fe_element
FEATURE [App::DocumentObjectGroupPython] Cr_element002  label="Cr_element : 18"  # scripted group (container) (typed FeaturePython)
  n = 18
  ref = Cr_element
FEATURE [App::DocumentObjectGroupPython] Ni_element002  label="Ni_element : 8"  # scripted group (container) (typed FeaturePython)
  n = 8
  ref = Ni_element
FEATURE [App::DocumentObjectGroupPython] G4_STAINLESS_STEEL  label="G4_STAINLESS-STEEL"  # scripted group (container) (typed FeaturePython)
  Dunit = g/cm3
  Dvalue = 8
  Group = -> [Fe_element008,Cr_element002,Ni_element002]
  conduct = 2
  density = 1
  expand = 3
  formula = G4_STAINLESS-STEEL
  name = G4_STAINLESS-STEEL
  specific = 4
FEATURE [App::DocumentObjectGroupPython] H_element117  label="H_element : 065"  # scripted group (container) (typed FeaturePython)
  n = 18
  ref = H_element
FEATURE [App::DocumentObjectGroupPython] C_element127  label="C_element : 072"  # scripted group (container) (typed FeaturePython)
  n = 12
  ref = C_element
FEATURE [App::DocumentObjectGroupPython] O_element109  label="O_element : 062"  # scripted group (container) (typed FeaturePython)
  n = 7
  ref = O_element
FEATURE [App::DocumentObjectGroupPython] G4_CR39  # scripted group (container) (typed FeaturePython)
  Dunit = g/cm3
  Dvalue = 1.32
  Group = -> [H_element117,C_element127,O_element109]
  conduct = 2
  density = 1
  expand = 3
  formula = G4_CR39
  name = G4_CR39
  specific = 4
FEATURE [App::DocumentObjectGroupPython] H_element118  label="H_element : 38"  # scripted group (container) (typed FeaturePython)
  n = 38
  ref = H_element
FEATURE [App::DocumentObjectGroupPython] C_element128  label="C_element : 073"  # scripted group (container) (typed FeaturePython)
  n = 18
  ref = C_element
FEATURE [App::DocumentObjectGroupPython] O_element110  label="O_element : 063"  # scripted group (container) (typed FeaturePython)
  n = 1
  ref = O_element
FEATURE [App::DocumentObjectGroupPython] G4_OCTADECANOL  # scripted group (container) (typed FeaturePython)
  Dunit = g/cm3
  Dvalue = 0.812
  Group = -> [H_element118,C_element128,O_element110]
  conduct = 2
  density = 1
  expand = 3
  formula = G4_OCTADECANOL
  name = G4_OCTADECANOL
  specific = 4
FEATURE [App::DocumentObjectGroupPython] HEP  # scripted group (container) (typed FeaturePython)
  Group = -> [G4_lH2,G4_lN2,G4_lO2,G4_lAr,G4_lBr,G4_lKr,G4_lXe,G4_PbWO4,G4_Galactic,G4_GRAPHITE_POROUS,G4_LUCITE,G4_BRASS,G4_BRONZE,G4_STAINLESS_STEEL,G4_CR39,G4_OCTADECANOL]
FEATURE [App::DocumentObjectGroupPython] C_element129  label="C_element : 074"  # scripted group (container) (typed FeaturePython)
  n = 14
  ref = C_element
FEATURE [App::DocumentObjectGroupPython] H_element119  label="H_element : 066"  # scripted group (container) (typed FeaturePython)
  n = 10
  ref = H_element
FEATURE [App::DocumentObjectGroupPython] O_element111  label="O_element : 064"  # scripted group (container) (typed FeaturePython)
  n = 2
  ref = O_element
FEATURE [App::DocumentObjectGroupPython] N_element050  label="N_element : 023"  # scripted group (container) (typed FeaturePython)
  n = 2
  ref = N_element
FEATURE [App::DocumentObjectGroupPython] G4_KEVLAR  # scripted group (container) (typed FeaturePython)
  Dunit = g/cm3
  Dvalue = 1.44
  Group = -> [C_element129,H_element119,O_element111,N_element050]
  conduct = 2
  density = 1
  expand = 3
  formula = G4_KEVLAR
  name = G4_KEVLAR
  specific = 4
FEATURE [App::DocumentObjectGroupPython] C_element130  label="C_element : 075"  # scripted group (container) (typed FeaturePython)
  n = 10
  ref = C_element
FEATURE [App::DocumentObjectGroupPython] H_element120  label="H_element : 067"  # scripted group (container) (typed FeaturePython)
  n = 8
  ref = H_element
FEATURE [App::DocumentObjectGroupPython] O_element112  label="O_element : 065"  # scripted group (container) (typed FeaturePython)
  n = 4
  ref = O_element
FEATURE [App::DocumentObjectGroupPython] G4_DACRON  # scripted group (container) (typed FeaturePython)
  Dunit = g/cm3
  Dvalue = 1.4
  Group = -> [C_element130,H_element120,O_element112]
  conduct = 2
  density = 1
  expand = 3
  formula = G4_DACRON
  name = G4_DACRON
  specific = 4
FEATURE [App::DocumentObjectGroupPython] C_element131  label="C_element : 076"  # scripted group (container) (typed FeaturePython)
  n = 4
  ref = C_element
FEATURE [App::DocumentObjectGroupPython] H_element121  label="H_element : 068"  # scripted group (container) (typed FeaturePython)
  n = 5
  ref = H_element
FEATURE [App::DocumentObjectGroupPython] Cl_element030  label="Cl_element : 016"  # scripted group (container) (typed FeaturePython)
  n = 1
  ref = Cl_element
FEATURE [App::DocumentObjectGroupPython] G4_NEOPRENE  # scripted group (container) (typed FeaturePython)
  Dunit = g/cm3
  Dvalue = 1.23
  Group = -> [C_element131,H_element121,Cl_element030]
  conduct = 2
  density = 1
  expand = 3
  formula = G4_NEOPRENE
  name = G4_NEOPRENE
  specific = 4
FEATURE [App::DocumentObjectGroupPython] Space  # scripted group (container) (typed FeaturePython)
  Group = -> [G4_KEVLAR,G4_DACRON,G4_NEOPRENE]
FEATURE [App::DocumentObjectGroupPython] H_element122  label="H_element : 069"  # scripted group (container) (typed FeaturePython)
  n = 5
  ref = H_element
FEATURE [App::DocumentObjectGroupPython] C_element132  label="C_element : 077"  # scripted group (container) (typed FeaturePython)
  n = 4
  ref = C_element
FEATURE [App::DocumentObjectGroupPython] N_element051  label="N_element : 3"  # scripted group (container) (typed FeaturePython)
  n = 3
  ref = N_element
FEATURE [App::DocumentObjectGroupPython] O_element113  label="O_element : 066"  # scripted group (container) (typed FeaturePython)
  n = 1
  ref = O_element
FEATURE [App::DocumentObjectGroupPython] G4_CYTOSINE  # scripted group (container) (typed FeaturePython)
  Dunit = g/cm3
  Dvalue = 1.55
  Group = -> [H_element122,C_element132,N_element051,O_element113]
  conduct = 2
  density = 1
  expand = 3
  formula = G4_CYTOSINE
  name = G4_CYTOSINE
  specific = 4
FEATURE [App::DocumentObjectGroupPython] H_element123  label="H_element : 070"  # scripted group (container) (typed FeaturePython)
  n = 6
  ref = H_element
FEATURE [App::DocumentObjectGroupPython] C_element133  label="C_element : 078"  # scripted group (container) (typed FeaturePython)
  n = 5
  ref = C_element
FEATURE [App::DocumentObjectGroupPython] N_element052  label="N_element : 024"  # scripted group (container) (typed FeaturePython)
  n = 2
  ref = N_element
FEATURE [App::DocumentObjectGroupPython] O_element114  label="O_element : 067"  # scripted group (container) (typed FeaturePython)
  n = 2
  ref = O_element
FEATURE [App::DocumentObjectGroupPython] G4_THYMINE  # scripted group (container) (typed FeaturePython)
  Dunit = g/cm3
  Dvalue = 1.23
  Group = -> [H_element123,C_element133,N_element052,O_element114]
  conduct = 2
  density = 1
  expand = 3
  formula = G4_THYMINE
  name = G4_THYMINE
  specific = 4
FEATURE [App::DocumentObjectGroupPython] H_element124  label="H_element : 071"  # scripted group (container) (typed FeaturePython)
  n = 4
  ref = H_element
FEATURE [App::DocumentObjectGroupPython] C_element134  label="C_element : 079"  # scripted group (container) (typed FeaturePython)
  n = 4
  ref = C_element
FEATURE [App::DocumentObjectGroupPython] N_element053  label="N_element : 025"  # scripted group (container) (typed FeaturePython)
  n = 2
  ref = N_element
FEATURE [App::DocumentObjectGroupPython] O_element115  label="O_element : 068"  # scripted group (container) (typed FeaturePython)
  n = 2
  ref = O_element
FEATURE [App::DocumentObjectGroupPython] G4_URACIL  # scripted group (container) (typed FeaturePython)
  Dunit = g/cm3
  Dvalue = 1.32
  Group = -> [H_element124,C_element134,N_element053,O_element115]
  conduct = 2
  density = 1
  expand = 3
  formula = G4_URACIL
  name = G4_URACIL
  specific = 4
FEATURE [App::DocumentObjectGroupPython] H_element125  label="H_element : 072"  # scripted group (container) (typed FeaturePython)
  n = 4
  ref = H_element
FEATURE [App::DocumentObjectGroupPython] C_element135  label="C_element : 080"  # scripted group (container) (typed FeaturePython)
  n = 5
  ref = C_element
FEATURE [App::DocumentObjectGroupPython] N_element054  label="N_element : 026"  # scripted group (container) (typed FeaturePython)
  n = 5
  ref = N_element
FEATURE [App::DocumentObjectGroupPython] G4_DNA_ADENINE  # scripted group (container) (typed FeaturePython)
  Dunit = g/cm3
  Dvalue = 1
  Group = -> [H_element125,C_element135,N_element054]
  conduct = 2
  density = 1
  expand = 3
  formula = G4_DNA_ADENINE
  name = G4_DNA_ADENINE
  specific = 4
FEATURE [App::DocumentObjectGroupPython] H_element126  label="H_element : 073"  # scripted group (container) (typed FeaturePython)
  n = 4
  ref = H_element
FEATURE [App::DocumentObjectGroupPython] C_element136  label="C_element : 081"  # scripted group (container) (typed FeaturePython)
  n = 5
  ref = C_element
FEATURE [App::DocumentObjectGroupPython] N_element055  label="N_element : 027"  # scripted group (container) (typed FeaturePython)
  n = 5
  ref = N_element
FEATURE [App::DocumentObjectGroupPython] O_element116  label="O_element : 069"  # scripted group (container) (typed FeaturePython)
  n = 1
  ref = O_element
FEATURE [App::DocumentObjectGroupPython] G4_DNA_GUANINE  # scripted group (container) (typed FeaturePython)
  Dunit = g/cm3
  Dvalue = 1
  Group = -> [H_element126,C_element136,N_element055,O_element116]
  conduct = 2
  density = 1
  expand = 3
  formula = G4_DNA_GUANINE
  name = G4_DNA_GUANINE
  specific = 4
FEATURE [App::DocumentObjectGroupPython] H_element127  label="H_element : 074"  # scripted group (container) (typed FeaturePython)
  n = 4
  ref = H_element
FEATURE [App::DocumentObjectGroupPython] C_element137  label="C_element : 082"  # scripted group (container) (typed FeaturePython)
  n = 4
  ref = C_element
FEATURE [App::DocumentObjectGroupPython] N_element056  label="N_element : 028"  # scripted group (container) (typed FeaturePython)
  n = 3
  ref = N_element
FEATURE [App::DocumentObjectGroupPython] O_element117  label="O_element : 070"  # scripted group (container) (typed FeaturePython)
  n = 1
  ref = O_element
FEATURE [App::DocumentObjectGroupPython] G4_DNA_CYTOSINE  # scripted group (container) (typed FeaturePython)
  Dunit = g/cm3
  Dvalue = 1
  Group = -> [H_element127,C_element137,N_element056,O_element117]
  conduct = 2
  density = 1
  expand = 3
  formula = G4_DNA_CYTOSINE
  name = G4_DNA_CYTOSINE
  specific = 4
FEATURE [App::DocumentObjectGroupPython] H_element128  label="H_element : 075"  # scripted group (container) (typed FeaturePython)
  n = 5
  ref = H_element
FEATURE [App::DocumentObjectGroupPython] C_element138  label="C_element : 083"  # scripted group (container) (typed FeaturePython)
  n = 5
  ref = C_element
FEATURE [App::DocumentObjectGroupPython] N_element057  label="N_element : 029"  # scripted group (container) (typed FeaturePython)
  n = 2
  ref = N_element
FEATURE [App::DocumentObjectGroupPython] O_element118  label="O_element : 071"  # scripted group (container) (typed FeaturePython)
  n = 2
  ref = O_element
FEATURE [App::DocumentObjectGroupPython] G4_DNA_THYMINE  # scripted group (container) (typed FeaturePython)
  Dunit = g/cm3
  Dvalue = 1
  Group = -> [H_element128,C_element138,N_element057,O_element118]
  conduct = 2
  density = 1
  expand = 3
  formula = G4_DNA_THYMINE
  name = G4_DNA_THYMINE
  specific = 4
FEATURE [App::DocumentObjectGroupPython] H_element129  label="H_element : 076"  # scripted group (container) (typed FeaturePython)
  n = 3
  ref = H_element
FEATURE [App::DocumentObjectGroupPython] C_element139  label="C_element : 084"  # scripted group (container) (typed FeaturePython)
  n = 4
  ref = C_element
FEATURE [App::DocumentObjectGroupPython] N_element058  label="N_element : 030"  # scripted group (container) (typed FeaturePython)
  n = 2
  ref = N_element
FEATURE [App::DocumentObjectGroupPython] O_element119  label="O_element : 072"  # scripted group (container) (typed FeaturePython)
  n = 2
  ref = O_element
FEATURE [App::DocumentObjectGroupPython] G4_DNA_URACIL  # scripted group (container) (typed FeaturePython)
  Dunit = g/cm3
  Dvalue = 1
  Group = -> [H_element129,C_element139,N_element058,O_element119]
  conduct = 2
  density = 1
  expand = 3
  formula = G4_DNA_URACIL
  name = G4_DNA_URACIL
  specific = 4
FEATURE [App::DocumentObjectGroupPython] H_element130  label="H_element : 077"  # scripted group (container) (typed FeaturePython)
  n = 10
  ref = H_element
FEATURE [App::DocumentObjectGroupPython] C_element140  label="C_element : 085"  # scripted group (container) (typed FeaturePython)
  n = 10
  ref = C_element
FEATURE [App::DocumentObjectGroupPython] N_element059  label="N_element : 031"  # scripted group (container) (typed FeaturePython)
  n = 5
  ref = N_element
FEATURE [App::DocumentObjectGroupPython] O_element120  label="O_element : 073"  # scripted group (container) (typed FeaturePython)
  n = 4
  ref = O_element
FEATURE [App::DocumentObjectGroupPython] G4_DNA_ADENOSINE  # scripted group (container) (typed FeaturePython)
  Dunit = g/cm3
  Dvalue = 1
  Group = -> [H_element130,C_element140,N_element059,O_element120]
  conduct = 2
  density = 1
  expand = 3
  formula = G4_DNA_ADENOSINE
  name = G4_DNA_ADENOSINE
  specific = 4
FEATURE [App::DocumentObjectGroupPython] H_element131  label="H_element : 078"  # scripted group (container) (typed FeaturePython)
  n = 10
  ref = H_element
FEATURE [App::DocumentObjectGroupPython] C_element141  label="C_element : 086"  # scripted group (container) (typed FeaturePython)
  n = 10
  ref = C_element
FEATURE [App::DocumentObjectGroupPython] N_element060  label="N_element : 032"  # scripted group (container) (typed FeaturePython)
  n = 5
  ref = N_element
FEATURE [App::DocumentObjectGroupPython] O_element121  label="O_element : 074"  # scripted group (container) (typed FeaturePython)
  n = 5
  ref = O_element
FEATURE [App::DocumentObjectGroupPython] G4_DNA_GUANOSINE  # scripted group (container) (typed FeaturePython)
  Dunit = g/cm3
  Dvalue = 1
  Group = -> [H_element131,C_element141,N_element060,O_element121]
  conduct = 2
  density = 1
  expand = 3
  formula = G4_DNA_GUANOSINE
  name = G4_DNA_GUANOSINE
  specific = 4
FEATURE [App::DocumentObjectGroupPython] H_element132  label="H_element : 079"  # scripted group (container) (typed FeaturePython)
  n = 10
  ref = H_element
FEATURE [App::DocumentObjectGroupPython] C_element142  label="C_element : 087"  # scripted group (container) (typed FeaturePython)
  n = 9
  ref = C_element
FEATURE [App::DocumentObjectGroupPython] N_element061  label="N_element : 033"  # scripted group (container) (typed FeaturePython)
  n = 3
  ref = N_element
FEATURE [App::DocumentObjectGroupPython] O_element122  label="O_element : 075"  # scripted group (container) (typed FeaturePython)
  n = 5
  ref = O_element
FEATURE [App::DocumentObjectGroupPython] G4_DNA_CYTIDINE  # scripted group (container) (typed FeaturePython)
  Dunit = g/cm3
  Dvalue = 1
  Group = -> [H_element132,C_element142,N_element061,O_element122]
  conduct = 2
  density = 1
  expand = 3
  formula = G4_DNA_CYTIDINE
  name = G4_DNA_CYTIDINE
  specific = 4
FEATURE [App::DocumentObjectGroupPython] H_element133  label="H_element : 080"  # scripted group (container) (typed FeaturePython)
  n = 9
  ref = H_element
FEATURE [App::DocumentObjectGroupPython] C_element143  label="C_element : 088"  # scripted group (container) (typed FeaturePython)
  n = 9
  ref = C_element
FEATURE [App::DocumentObjectGroupPython] N_element062  label="N_element : 034"  # scripted group (container) (typed FeaturePython)
  n = 2
  ref = N_element
FEATURE [App::DocumentObjectGroupPython] O_element123  label="O_element : 076"  # scripted group (container) (typed FeaturePython)
  n = 6
  ref = O_element
FEATURE [App::DocumentObjectGroupPython] G4_DNA_URIDINE  # scripted group (container) (typed FeaturePython)
  Dunit = g/cm3
  Dvalue = 1
  Group = -> [H_element133,C_element143,N_element062,O_element123]
  conduct = 2
  density = 1
  expand = 3
  formula = G4_DNA_URIDINE
  name = G4_DNA_URIDINE
  specific = 4
FEATURE [App::DocumentObjectGroupPython] H_element134  label="H_element : 081"  # scripted group (container) (typed FeaturePython)
  n = 11
  ref = H_element
FEATURE [App::DocumentObjectGroupPython] C_element144  label="C_element : 089"  # scripted group (container) (typed FeaturePython)
  n = 10
  ref = C_element
FEATURE [App::DocumentObjectGroupPython] N_element063  label="N_element : 035"  # scripted group (container) (typed FeaturePython)
  n = 2
  ref = N_element
FEATURE [App::DocumentObjectGroupPython] O_element124  label="O_element : 077"  # scripted group (container) (typed FeaturePython)
  n = 6
  ref = O_element
FEATURE [App::DocumentObjectGroupPython] G4_DNA_METHYLURIDINE  # scripted group (container) (typed FeaturePython)
  Dunit = g/cm3
  Dvalue = 1
  Group = -> [H_element134,C_element144,N_element063,O_element124]
  conduct = 2
  density = 1
  expand = 3
  formula = G4_DNA_METHYLURIDINE
  name = G4_DNA_METHYLURIDINE
  specific = 4
FEATURE [App::DocumentObjectGroupPython] P_element014  label="P_element : 003"  # scripted group (container) (typed FeaturePython)
  n = 1
  ref = P_element
FEATURE [App::DocumentObjectGroupPython] O_element125  label="O_element : 078"  # scripted group (container) (typed FeaturePython)
  n = 3
  ref = O_element
FEATURE [App::DocumentObjectGroupPython] G4_DNA_MONOPHOSPHATE  # scripted group (container) (typed FeaturePython)
  Dunit = g/cm3
  Dvalue = 1
  Group = -> [P_element014,O_element125]
  conduct = 2
  density = 1
  expand = 3
  formula = G4_DNA_MONOPHOSPHATE
  name = G4_DNA_MONOPHOSPHATE
  specific = 4
FEATURE [App::DocumentObjectGroupPython] H_element135  label="H_element : 082"  # scripted group (container) (typed FeaturePython)
  n = 10
  ref = H_element
FEATURE [App::DocumentObjectGroupPython] C_element145  label="C_element : 090"  # scripted group (container) (typed FeaturePython)
  n = 10
  ref = C_element
FEATURE [App::DocumentObjectGroupPython] N_element064  label="N_element : 036"  # scripted group (container) (typed FeaturePython)
  n = 5
  ref = N_element
FEATURE [App::DocumentObjectGroupPython] O_element126  label="O_element : 079"  # scripted group (container) (typed FeaturePython)
  n = 7
  ref = O_element
FEATURE [App::DocumentObjectGroupPython] P_element015  label="P_element : 004"  # scripted group (container) (typed FeaturePython)
  n = 1
  ref = P_element
FEATURE [App::DocumentObjectGroupPython] G4_DNA_A  # scripted group (container) (typed FeaturePython)
  Dunit = g/cm3
  Dvalue = 1
  Group = -> [H_element135,C_element145,N_element064,O_element126,P_element015]
  conduct = 2
  density = 1
  expand = 3
  formula = G4_DNA_A
  name = G4_DNA_A
  specific = 4
FEATURE [App::DocumentObjectGroupPython] H_element136  label="H_element : 083"  # scripted group (container) (typed FeaturePython)
  n = 10
  ref = H_element
FEATURE [App::DocumentObjectGroupPython] C_element146  label="C_element : 091"  # scripted group (container) (typed FeaturePython)
  n = 10
  ref = C_element
FEATURE [App::DocumentObjectGroupPython] N_element065  label="N_element : 037"  # scripted group (container) (typed FeaturePython)
  n = 5
  ref = N_element
FEATURE [App::DocumentObjectGroupPython] O_element127  label="O_element : 8"  # scripted group (container) (typed FeaturePython)
  n = 8
  ref = O_element
FEATURE [App::DocumentObjectGroupPython] P_element016  label="P_element : 005"  # scripted group (container) (typed FeaturePython)
  n = 1
  ref = P_element
FEATURE [App::DocumentObjectGroupPython] G4_DNA_G  # scripted group (container) (typed FeaturePython)
  Dunit = g/cm3
  Dvalue = 1
  Group = -> [H_element136,C_element146,N_element065,O_element127,P_element016]
  conduct = 2
  density = 1
  expand = 3
  formula = G4_DNA_G
  name = G4_DNA_G
  specific = 4
FEATURE [App::DocumentObjectGroupPython] H_element137  label="H_element : 084"  # scripted group (container) (typed FeaturePython)
  n = 10
  ref = H_element
FEATURE [App::DocumentObjectGroupPython] C_element147  label="C_element : 092"  # scripted group (container) (typed FeaturePython)
  n = 9
  ref = C_element
FEATURE [App::DocumentObjectGroupPython] N_element066  label="N_element : 038"  # scripted group (container) (typed FeaturePython)
  n = 3
  ref = N_element
FEATURE [App::DocumentObjectGroupPython] O_element128  label="O_element : 080"  # scripted group (container) (typed FeaturePython)
  n = 8
  ref = O_element
FEATURE [App::DocumentObjectGroupPython] P_element017  label="P_element : 006"  # scripted group (container) (typed FeaturePython)
  n = 1
  ref = P_element
FEATURE [App::DocumentObjectGroupPython] G4_DNA_C  # scripted group (container) (typed FeaturePython)
  Dunit = g/cm3
  Dvalue = 1
  Group = -> [H_element137,C_element147,N_element066,O_element128,P_element017]
  conduct = 2
  density = 1
  expand = 3
  formula = G4_DNA_C
  name = G4_DNA_C
  specific = 4
FEATURE [App::DocumentObjectGroupPython] H_element138  label="H_element : 085"  # scripted group (container) (typed FeaturePython)
  n = 9
  ref = H_element
FEATURE [App::DocumentObjectGroupPython] C_element148  label="C_element : 093"  # scripted group (container) (typed FeaturePython)
  n = 9
  ref = C_element
FEATURE [App::DocumentObjectGroupPython] N_element067  label="N_element : 039"  # scripted group (container) (typed FeaturePython)
  n = 2
  ref = N_element
FEATURE [App::DocumentObjectGroupPython] O_element129  label="O_element : 9"  # scripted group (container) (typed FeaturePython)
  n = 9
  ref = O_element
FEATURE [App::DocumentObjectGroupPython] P_element018  label="P_element : 007"  # scripted group (container) (typed FeaturePython)
  n = 1
  ref = P_element
FEATURE [App::DocumentObjectGroupPython] G4_DNA_U  # scripted group (container) (typed FeaturePython)
  Dunit = g/cm3
  Dvalue = 1
  Group = -> [H_element138,C_element148,N_element067,O_element129,P_element018]
  conduct = 2
  density = 1
  expand = 3
  formula = G4_DNA_U
  name = G4_DNA_U
  specific = 4
FEATURE [App::DocumentObjectGroupPython] H_element139  label="H_element : 086"  # scripted group (container) (typed FeaturePython)
  n = 11
  ref = H_element
FEATURE [App::DocumentObjectGroupPython] C_element149  label="C_element : 094"  # scripted group (container) (typed FeaturePython)
  n = 10
  ref = C_element
FEATURE [App::DocumentObjectGroupPython] N_element068  label="N_element : 040"  # scripted group (container) (typed FeaturePython)
  n = 2
  ref = N_element
FEATURE [App::DocumentObjectGroupPython] O_element130  label="O_element : 081"  # scripted group (container) (typed FeaturePython)
  n = 9
  ref = O_element
FEATURE [App::DocumentObjectGroupPython] P_element019  label="P_element : 008"  # scripted group (container) (typed FeaturePython)
  n = 1
  ref = P_element
FEATURE [App::DocumentObjectGroupPython] G4_DNA_MU  # scripted group (container) (typed FeaturePython)
  Dunit = g/cm3
  Dvalue = 1
  Group = -> [H_element139,C_element149,N_element068,O_element130,P_element019]
  conduct = 2
  density = 1
  expand = 3
  formula = G4_DNA_MU
  name = G4_DNA_MU
  specific = 4
FEATURE [App::DocumentObjectGroupPython] BioChemical  # scripted group (container) (typed FeaturePython)
  Group = -> [G4_CYTOSINE,G4_THYMINE,G4_URACIL,G4_DNA_ADENINE,G4_DNA_GUANINE,G4_DNA_CYTOSINE,G4_DNA_THYMINE,G4_DNA_URACIL,G4_DNA_ADENOSINE,G4_DNA_GUANOSINE,G4_DNA_CYTIDINE,G4_DNA_URIDINE,G4_DNA_METHYLURIDINE,G4_DNA_MONOPHOSPHATE,G4_DNA_A,G4_DNA_G,G4_DNA_C,G4_DNA_U,G4_DNA_MU]
FEATURE [App::DocumentObjectGroupPython] G4Materials  # scripted group (container) (typed FeaturePython)
  Group = -> [NIST,Element,HEP,Space,BioChemical]
  version = 1
FEATURE [App::DocumentObjectGroupPython] Geant4  # scripted group (container) (typed FeaturePython)
  Group = -> [G4Isotopes,G4Elements,G4Materials]
FEATURE [App::DocumentObjectGroupPython] Materials  # scripted group (container) (typed FeaturePython)
  Group = -> [Geant4]
FEATURE [Part::FeaturePython] GDMLBox_WorldBox  # WARN: FeaturePython — macro-defined, semantics opaque (R4)
  lunit = 2
  material = 5
  x = 200.2
  y = 130
  z = 130
FEATURE [Part::FeaturePython] GDMLBox_Box  # WARN: FeaturePython — macro-defined, semantics opaque (R4)
  Placement = pos=(30,0,0) rot=(0,0,1;0rad)
  lunit = 2
  material = 0
  x = 10
  y = 10
  z = 10
FEATURE [Part::FeaturePython] GDMLTorus  # WARN: FeaturePython — macro-defined, semantics opaque (R4)
  Placement = pos=(30,0,0) rot=(0,1,0;1.5708rad)
  aunit = deg
  deltaphi = 360
  lunit = 2
  material = 0
  rmax = 2
  rmin = 0
  rtor = 8
  startphi = 0
FEATURE [Part::MultiFuse] Fusion
  Shapes = -> [GDMLBox_Box,GDMLTorus]
FEATURE [Part::FeaturePython] Array  # Draft array (typed FeaturePython)
  AlwaysSyncPlacement = false
  Angle = 180
  ArrayType = 1
  Axis = (0,0,1)
  Base = -> Fusion
  Center = (0,0,0)
  Count = 5
  ExpandArray = false
  Fuse = false
  IntervalAxis = (0,0,0)
  IntervalX = (50,0,0)
  IntervalY = (0,50,0)
  IntervalZ = (0,0,50)
  NumberCircles = 3
  NumberPolar = 5
  NumberX = 2
  NumberY = 2
  NumberZ = 1
  Placement = pos=(42,0,0) rot=(0,0,1;0rad)
  PlacementList = 5 placements: [(0,0,0),(0,0,0),(0,0,0),(0,0,0),(0,0,0)]
  RadialDistance = 50
  ScaleList = (5) [(1,1,1),(1,1,1),(1,1,1),(1,1,1),(1,1,1)]
  Symmetry = 1
  TangentialDistance = 25
FEATURE [App::Part] Part001
  Group = -> [Array]
  Origin = -> Origin004
FEATURE [App::Part] worldVOL
  Group = -> [GDMLBox_WorldBox,Part001]
  Origin = -> Origin
